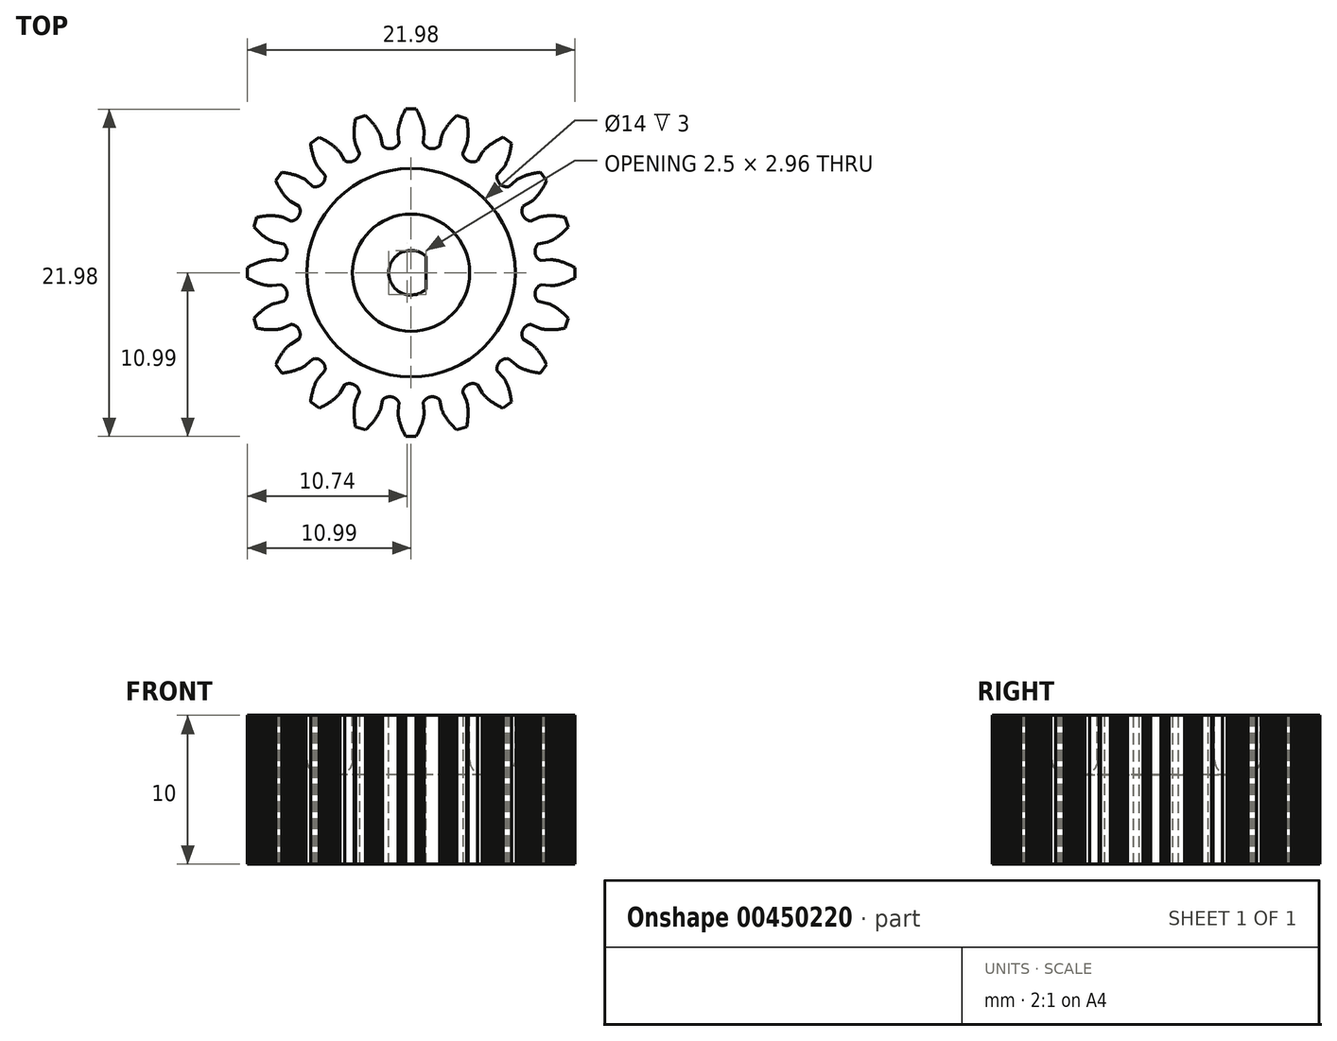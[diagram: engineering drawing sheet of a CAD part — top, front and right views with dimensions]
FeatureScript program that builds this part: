
annotation { "Feature Type Name" : "Feature", "Feature Type Description" : "" }
export const myFeature = defineFeature(function(context is Context, id is Id, definition is map)
    precondition{}
    {
        {
            var Q0;
            Q0=qCreatedBy(makeId("Top.planeOp"),FACE);
            var sketch = newSketch(context, id + "F0", { "sketchPlane" : qUnion([Q0])});
            skLineSegment(sketch, "E0", {"start": v(8.71, -0.82) * mm, "end": v(9.36, -0.88) * mm});
            skLineSegment(sketch, "E1", {"start": v(9.36, -0.88) * mm, "end": v(9.4, -0.88) * mm});
            skLineSegment(sketch, "E2", {"start": v(9.4, -0.88) * mm, "end": v(9.46, -0.88) * mm});
            skLineSegment(sketch, "E3", {"start": v(9.46, -0.88) * mm, "end": v(9.51, -0.87) * mm});
            skLineSegment(sketch, "E4", {"start": v(9.51, -0.87) * mm, "end": v(9.58, -0.87) * mm});
            skLineSegment(sketch, "E5", {"start": v(9.58, -0.87) * mm, "end": v(9.64, -0.86) * mm});
            skLineSegment(sketch, "E6", {"start": v(9.64, -0.86) * mm, "end": v(9.7, -0.85) * mm});
            skLineSegment(sketch, "E7", {"start": v(9.7, -0.85) * mm, "end": v(9.77, -0.83) * mm});
            skLineSegment(sketch, "E8", {"start": v(9.77, -0.83) * mm, "end": v(9.84, -0.82) * mm});
            skLineSegment(sketch, "E9", {"start": v(9.84, -0.82) * mm, "end": v(9.9, -0.8) * mm});
            skLineSegment(sketch, "E10", {"start": v(9.9, -0.8) * mm, "end": v(9.95, -0.8) * mm});
            skLineSegment(sketch, "E11", {"start": v(9.95, -0.8) * mm, "end": v(10, -0.77) * mm});
            skLineSegment(sketch, "E12", {"start": v(10, -0.77) * mm, "end": v(10.07, -0.76) * mm});
            skLineSegment(sketch, "E13", {"start": v(10.07, -0.76) * mm, "end": v(10.13, -0.74) * mm});
            skLineSegment(sketch, "E14", {"start": v(10.13, -0.74) * mm, "end": v(10.2, -0.71) * mm});
            skLineSegment(sketch, "E15", {"start": v(10.2, -0.71) * mm, "end": v(10.26, -0.7) * mm});
            skLineSegment(sketch, "E16", {"start": v(10.26, -0.7) * mm, "end": v(10.33, -0.66) * mm});
            skLineSegment(sketch, "E17", {"start": v(10.33, -0.66) * mm, "end": v(10.4, -0.64) * mm});
            skLineSegment(sketch, "E18", {"start": v(10.4, -0.64) * mm, "end": v(10.48, -0.6) * mm});
            skLineSegment(sketch, "E19", {"start": v(10.48, -0.6) * mm, "end": v(10.55, -0.57) * mm});
            skLineSegment(sketch, "E20", {"start": v(10.55, -0.57) * mm, "end": v(10.63, -0.54) * mm});
            skLineSegment(sketch, "E21", {"start": v(10.63, -0.54) * mm, "end": v(10.71, -0.5) * mm});
            skLineSegment(sketch, "E22", {"start": v(10.71, -0.5) * mm, "end": v(10.8, -0.46) * mm});
            skLineSegment(sketch, "E23", {"start": v(10.8, -0.46) * mm, "end": v(10.88, -0.41) * mm});
            skLineSegment(sketch, "E24", {"start": v(10.88, -0.41) * mm, "end": v(11, -0.35) * mm});
            skLineSegment(sketch, "E25", {"start": v(11, -0.35) * mm, "end": v(11, 0.35) * mm});
            skLineSegment(sketch, "E26", {"start": v(11, 0.35) * mm, "end": v(10.88, 0.41) * mm});
            skLineSegment(sketch, "E27", {"start": v(10.88, 0.41) * mm, "end": v(10.8, 0.46) * mm});
            skLineSegment(sketch, "E28", {"start": v(10.8, 0.46) * mm, "end": v(10.71, 0.5) * mm});
            skLineSegment(sketch, "E29", {"start": v(10.71, 0.5) * mm, "end": v(10.63, 0.54) * mm});
            skLineSegment(sketch, "E30", {"start": v(10.63, 0.54) * mm, "end": v(10.55, 0.57) * mm});
            skLineSegment(sketch, "E31", {"start": v(10.55, 0.57) * mm, "end": v(10.48, 0.6) * mm});
            skLineSegment(sketch, "E32", {"start": v(10.48, 0.6) * mm, "end": v(10.4, 0.64) * mm});
            skLineSegment(sketch, "E33", {"start": v(10.4, 0.64) * mm, "end": v(10.33, 0.66) * mm});
            skLineSegment(sketch, "E34", {"start": v(10.33, 0.66) * mm, "end": v(10.26, 0.7) * mm});
            skLineSegment(sketch, "E35", {"start": v(10.26, 0.7) * mm, "end": v(10.2, 0.71) * mm});
            skLineSegment(sketch, "E36", {"start": v(10.2, 0.71) * mm, "end": v(10.13, 0.74) * mm});
            skLineSegment(sketch, "E37", {"start": v(10.13, 0.74) * mm, "end": v(10.07, 0.76) * mm});
            skLineSegment(sketch, "E38", {"start": v(10.07, 0.76) * mm, "end": v(10, 0.77) * mm});
            skLineSegment(sketch, "E39", {"start": v(10, 0.77) * mm, "end": v(9.95, 0.8) * mm});
            skLineSegment(sketch, "E40", {"start": v(9.95, 0.8) * mm, "end": v(9.9, 0.8) * mm});
            skLineSegment(sketch, "E41", {"start": v(9.9, 0.8) * mm, "end": v(9.84, 0.82) * mm});
            skLineSegment(sketch, "E42", {"start": v(9.84, 0.82) * mm, "end": v(9.77, 0.83) * mm});
            skLineSegment(sketch, "E43", {"start": v(9.77, 0.83) * mm, "end": v(9.7, 0.85) * mm});
            skLineSegment(sketch, "E44", {"start": v(9.7, 0.85) * mm, "end": v(9.64, 0.86) * mm});
            skLineSegment(sketch, "E45", {"start": v(9.64, 0.86) * mm, "end": v(9.58, 0.87) * mm});
            skLineSegment(sketch, "E46", {"start": v(9.58, 0.87) * mm, "end": v(9.51, 0.87) * mm});
            skLineSegment(sketch, "E47", {"start": v(9.51, 0.87) * mm, "end": v(9.46, 0.88) * mm});
            skLineSegment(sketch, "E48", {"start": v(9.46, 0.88) * mm, "end": v(9.4, 0.88) * mm});
            skLineSegment(sketch, "E49", {"start": v(9.4, 0.88) * mm, "end": v(9.36, 0.88) * mm});
            skLineSegment(sketch, "E50", {"start": v(9.36, 0.88) * mm, "end": v(8.71, 0.82) * mm});
            skArc(sketch, "E51", {"start": v(8.71, 0.82) * mm, "mid": v(8.34, 1.32) * mm, "end": v(8.54, 1.92) * mm});
            skLineSegment(sketch, "E52", {"start": v(8.54, 1.92) * mm, "end": v(9.17, 2.06) * mm});
            skLineSegment(sketch, "E53", {"start": v(9.17, 2.06) * mm, "end": v(9.22, 2.07) * mm});
            skLineSegment(sketch, "E54", {"start": v(9.22, 2.07) * mm, "end": v(9.27, 2.09) * mm});
            skLineSegment(sketch, "E55", {"start": v(9.27, 2.09) * mm, "end": v(9.32, 2.11) * mm});
            skLineSegment(sketch, "E56", {"start": v(9.32, 2.11) * mm, "end": v(9.38, 2.14) * mm});
            skLineSegment(sketch, "E57", {"start": v(9.38, 2.14) * mm, "end": v(9.43, 2.16) * mm});
            skLineSegment(sketch, "E58", {"start": v(9.43, 2.16) * mm, "end": v(9.48, 2.2) * mm});
            skLineSegment(sketch, "E59", {"start": v(9.48, 2.2) * mm, "end": v(9.55, 2.22) * mm});
            skLineSegment(sketch, "E60", {"start": v(9.55, 2.22) * mm, "end": v(9.61, 2.26) * mm});
            skLineSegment(sketch, "E61", {"start": v(9.61, 2.26) * mm, "end": v(9.66, 2.3) * mm});
            skLineSegment(sketch, "E62", {"start": v(9.66, 2.3) * mm, "end": v(9.7, 2.32) * mm});
            skLineSegment(sketch, "E63", {"start": v(9.7, 2.32) * mm, "end": v(9.76, 2.36) * mm});
            skLineSegment(sketch, "E64", {"start": v(9.76, 2.36) * mm, "end": v(9.8, 2.4) * mm});
            skLineSegment(sketch, "E65", {"start": v(9.8, 2.4) * mm, "end": v(9.86, 2.43) * mm});
            skLineSegment(sketch, "E66", {"start": v(9.86, 2.43) * mm, "end": v(9.92, 2.47) * mm});
            skLineSegment(sketch, "E67", {"start": v(9.92, 2.47) * mm, "end": v(9.97, 2.52) * mm});
            skLineSegment(sketch, "E68", {"start": v(9.97, 2.52) * mm, "end": v(10.03, 2.56) * mm});
            skLineSegment(sketch, "E69", {"start": v(10.03, 2.56) * mm, "end": v(10.1, 2.61) * mm});
            skLineSegment(sketch, "E70", {"start": v(10.1, 2.61) * mm, "end": v(10.15, 2.66) * mm});
            skLineSegment(sketch, "E71", {"start": v(10.15, 2.66) * mm, "end": v(10.21, 2.72) * mm});
            skLineSegment(sketch, "E72", {"start": v(10.21, 2.72) * mm, "end": v(10.28, 2.78) * mm});
            skLineSegment(sketch, "E73", {"start": v(10.28, 2.78) * mm, "end": v(10.34, 2.84) * mm});
            skLineSegment(sketch, "E74", {"start": v(10.34, 2.84) * mm, "end": v(10.4, 2.9) * mm});
            skLineSegment(sketch, "E75", {"start": v(10.4, 2.9) * mm, "end": v(10.47, 2.97) * mm});
            skLineSegment(sketch, "E76", {"start": v(10.47, 2.97) * mm, "end": v(10.56, 3.07) * mm});
            skLineSegment(sketch, "E77", {"start": v(10.56, 3.07) * mm, "end": v(10.35, 3.73) * mm});
            skLineSegment(sketch, "E78", {"start": v(10.35, 3.73) * mm, "end": v(10.22, 3.75) * mm});
            skLineSegment(sketch, "E79", {"start": v(10.22, 3.75) * mm, "end": v(10.12, 3.77) * mm});
            skLineSegment(sketch, "E80", {"start": v(10.12, 3.77) * mm, "end": v(10.03, 3.78) * mm});
            skLineSegment(sketch, "E81", {"start": v(10.03, 3.78) * mm, "end": v(9.95, 3.8) * mm});
            skLineSegment(sketch, "E82", {"start": v(9.95, 3.8) * mm, "end": v(9.86, 3.8) * mm});
            skLineSegment(sketch, "E83", {"start": v(9.86, 3.8) * mm, "end": v(9.78, 3.81) * mm});
            skLineSegment(sketch, "E84", {"start": v(9.78, 3.81) * mm, "end": v(9.7, 3.82) * mm});
            skLineSegment(sketch, "E85", {"start": v(9.7, 3.82) * mm, "end": v(9.62, 3.82) * mm});
            skLineSegment(sketch, "E86", {"start": v(9.62, 3.82) * mm, "end": v(9.55, 3.83) * mm});
            skLineSegment(sketch, "E87", {"start": v(9.55, 3.83) * mm, "end": v(9.48, 3.83) * mm});
            skLineSegment(sketch, "E88", {"start": v(9.48, 3.83) * mm, "end": v(9.4, 3.83) * mm});
            skLineSegment(sketch, "E89", {"start": v(9.4, 3.83) * mm, "end": v(9.34, 3.83) * mm});
            skLineSegment(sketch, "E90", {"start": v(9.34, 3.83) * mm, "end": v(9.28, 3.83) * mm});
            skLineSegment(sketch, "E91", {"start": v(9.28, 3.83) * mm, "end": v(9.22, 3.83) * mm});
            skLineSegment(sketch, "E92", {"start": v(9.22, 3.83) * mm, "end": v(9.16, 3.82) * mm});
            skLineSegment(sketch, "E93", {"start": v(9.16, 3.82) * mm, "end": v(9.1, 3.82) * mm});
            skLineSegment(sketch, "E94", {"start": v(9.1, 3.82) * mm, "end": v(9.03, 3.81) * mm});
            skLineSegment(sketch, "E95", {"start": v(9.03, 3.81) * mm, "end": v(8.96, 3.8) * mm});
            skLineSegment(sketch, "E96", {"start": v(8.96, 3.8) * mm, "end": v(8.9, 3.8) * mm});
            skLineSegment(sketch, "E97", {"start": v(8.9, 3.8) * mm, "end": v(8.84, 3.78) * mm});
            skLineSegment(sketch, "E98", {"start": v(8.84, 3.78) * mm, "end": v(8.78, 3.77) * mm});
            skLineSegment(sketch, "E99", {"start": v(8.78, 3.77) * mm, "end": v(8.73, 3.76) * mm});
            skLineSegment(sketch, "E100", {"start": v(8.73, 3.76) * mm, "end": v(8.68, 3.74) * mm});
            skLineSegment(sketch, "E101", {"start": v(8.68, 3.74) * mm, "end": v(8.63, 3.73) * mm});
            skLineSegment(sketch, "E102", {"start": v(8.63, 3.73) * mm, "end": v(8.03, 3.47) * mm});
            skArc(sketch, "E103", {"start": v(8.03, 3.47) * mm, "mid": v(7.52, 3.83) * mm, "end": v(7.53, 4.46) * mm});
            skLineSegment(sketch, "E104", {"start": v(7.53, 4.46) * mm, "end": v(8.08, 4.79) * mm});
            skLineSegment(sketch, "E105", {"start": v(8.08, 4.79) * mm, "end": v(8.13, 4.82) * mm});
            skLineSegment(sketch, "E106", {"start": v(8.13, 4.82) * mm, "end": v(8.17, 4.85) * mm});
            skLineSegment(sketch, "E107", {"start": v(8.17, 4.85) * mm, "end": v(8.2, 4.89) * mm});
            skLineSegment(sketch, "E108", {"start": v(8.2, 4.89) * mm, "end": v(8.26, 4.93) * mm});
            skLineSegment(sketch, "E109", {"start": v(8.26, 4.93) * mm, "end": v(8.3, 4.97) * mm});
            skLineSegment(sketch, "E110", {"start": v(8.3, 4.97) * mm, "end": v(8.34, 5.01) * mm});
            skLineSegment(sketch, "E111", {"start": v(8.34, 5.01) * mm, "end": v(8.4, 5.07) * mm});
            skLineSegment(sketch, "E112", {"start": v(8.4, 5.07) * mm, "end": v(8.44, 5.12) * mm});
            skLineSegment(sketch, "E113", {"start": v(8.44, 5.12) * mm, "end": v(8.48, 5.16) * mm});
            skLineSegment(sketch, "E114", {"start": v(8.48, 5.16) * mm, "end": v(8.51, 5.2) * mm});
            skLineSegment(sketch, "E115", {"start": v(8.51, 5.2) * mm, "end": v(8.55, 5.26) * mm});
            skLineSegment(sketch, "E116", {"start": v(8.55, 5.26) * mm, "end": v(8.59, 5.3) * mm});
            skLineSegment(sketch, "E117", {"start": v(8.59, 5.3) * mm, "end": v(8.63, 5.36) * mm});
            skLineSegment(sketch, "E118", {"start": v(8.63, 5.36) * mm, "end": v(8.67, 5.41) * mm});
            skLineSegment(sketch, "E119", {"start": v(8.67, 5.41) * mm, "end": v(8.7, 5.47) * mm});
            skLineSegment(sketch, "E120", {"start": v(8.7, 5.47) * mm, "end": v(8.75, 5.54) * mm});
            skLineSegment(sketch, "E121", {"start": v(8.75, 5.54) * mm, "end": v(8.8, 5.6) * mm});
            skLineSegment(sketch, "E122", {"start": v(8.8, 5.6) * mm, "end": v(8.83, 5.67) * mm});
            skLineSegment(sketch, "E123", {"start": v(8.83, 5.67) * mm, "end": v(8.87, 5.74) * mm});
            skLineSegment(sketch, "E124", {"start": v(8.87, 5.74) * mm, "end": v(8.92, 5.82) * mm});
            skLineSegment(sketch, "E125", {"start": v(8.92, 5.82) * mm, "end": v(8.96, 5.9) * mm});
            skLineSegment(sketch, "E126", {"start": v(8.96, 5.9) * mm, "end": v(9, 5.98) * mm});
            skLineSegment(sketch, "E127", {"start": v(9, 5.98) * mm, "end": v(9.04, 6.06) * mm});
            skLineSegment(sketch, "E128", {"start": v(9.04, 6.06) * mm, "end": v(9.1, 6.18) * mm});
            skLineSegment(sketch, "E129", {"start": v(9.1, 6.18) * mm, "end": v(8.7, 6.74) * mm});
            skLineSegment(sketch, "E130", {"start": v(8.7, 6.74) * mm, "end": v(8.56, 6.73) * mm});
            skLineSegment(sketch, "E131", {"start": v(8.56, 6.73) * mm, "end": v(8.46, 6.71) * mm});
            skLineSegment(sketch, "E132", {"start": v(8.46, 6.71) * mm, "end": v(8.37, 6.7) * mm});
            skLineSegment(sketch, "E133", {"start": v(8.37, 6.7) * mm, "end": v(8.29, 6.68) * mm});
            skLineSegment(sketch, "E134", {"start": v(8.29, 6.68) * mm, "end": v(8.2, 6.67) * mm});
            skLineSegment(sketch, "E135", {"start": v(8.2, 6.67) * mm, "end": v(8.12, 6.65) * mm});
            skLineSegment(sketch, "E136", {"start": v(8.12, 6.65) * mm, "end": v(8.04, 6.63) * mm});
            skLineSegment(sketch, "E137", {"start": v(8.04, 6.63) * mm, "end": v(7.97, 6.61) * mm});
            skLineSegment(sketch, "E138", {"start": v(7.97, 6.61) * mm, "end": v(7.9, 6.6) * mm});
            skLineSegment(sketch, "E139", {"start": v(7.9, 6.6) * mm, "end": v(7.83, 6.57) * mm});
            skLineSegment(sketch, "E140", {"start": v(7.83, 6.57) * mm, "end": v(7.76, 6.55) * mm});
            skLineSegment(sketch, "E141", {"start": v(7.76, 6.55) * mm, "end": v(7.7, 6.53) * mm});
            skLineSegment(sketch, "E142", {"start": v(7.7, 6.53) * mm, "end": v(7.64, 6.5) * mm});
            skLineSegment(sketch, "E143", {"start": v(7.64, 6.5) * mm, "end": v(7.58, 6.49) * mm});
            skLineSegment(sketch, "E144", {"start": v(7.58, 6.49) * mm, "end": v(7.53, 6.47) * mm});
            skLineSegment(sketch, "E145", {"start": v(7.53, 6.47) * mm, "end": v(7.48, 6.45) * mm});
            skLineSegment(sketch, "E146", {"start": v(7.48, 6.45) * mm, "end": v(7.41, 6.42) * mm});
            skLineSegment(sketch, "E147", {"start": v(7.41, 6.42) * mm, "end": v(7.35, 6.39) * mm});
            skLineSegment(sketch, "E148", {"start": v(7.35, 6.39) * mm, "end": v(7.3, 6.36) * mm});
            skLineSegment(sketch, "E149", {"start": v(7.3, 6.36) * mm, "end": v(7.24, 6.33) * mm});
            skLineSegment(sketch, "E150", {"start": v(7.24, 6.33) * mm, "end": v(7.18, 6.3) * mm});
            skLineSegment(sketch, "E151", {"start": v(7.18, 6.3) * mm, "end": v(7.14, 6.27) * mm});
            skLineSegment(sketch, "E152", {"start": v(7.14, 6.27) * mm, "end": v(7.1, 6.24) * mm});
            skLineSegment(sketch, "E153", {"start": v(7.1, 6.24) * mm, "end": v(7.05, 6.2) * mm});
            skLineSegment(sketch, "E154", {"start": v(7.05, 6.2) * mm, "end": v(6.57, 5.78) * mm});
            skArc(sketch, "E155", {"start": v(6.57, 5.78) * mm, "mid": v(5.97, 5.97) * mm, "end": v(5.78, 6.57) * mm});
            skLineSegment(sketch, "E156", {"start": v(5.78, 6.57) * mm, "end": v(6.2, 7.05) * mm});
            skLineSegment(sketch, "E157", {"start": v(6.2, 7.05) * mm, "end": v(6.24, 7.1) * mm});
            skLineSegment(sketch, "E158", {"start": v(6.24, 7.1) * mm, "end": v(6.27, 7.14) * mm});
            skLineSegment(sketch, "E159", {"start": v(6.27, 7.14) * mm, "end": v(6.3, 7.18) * mm});
            skLineSegment(sketch, "E160", {"start": v(6.3, 7.18) * mm, "end": v(6.33, 7.24) * mm});
            skLineSegment(sketch, "E161", {"start": v(6.33, 7.24) * mm, "end": v(6.36, 7.3) * mm});
            skLineSegment(sketch, "E162", {"start": v(6.36, 7.3) * mm, "end": v(6.39, 7.35) * mm});
            skLineSegment(sketch, "E163", {"start": v(6.39, 7.35) * mm, "end": v(6.42, 7.41) * mm});
            skLineSegment(sketch, "E164", {"start": v(6.42, 7.41) * mm, "end": v(6.45, 7.48) * mm});
            skLineSegment(sketch, "E165", {"start": v(6.45, 7.48) * mm, "end": v(6.47, 7.53) * mm});
            skLineSegment(sketch, "E166", {"start": v(6.47, 7.53) * mm, "end": v(6.49, 7.58) * mm});
            skLineSegment(sketch, "E167", {"start": v(6.49, 7.58) * mm, "end": v(6.5, 7.64) * mm});
            skLineSegment(sketch, "E168", {"start": v(6.5, 7.64) * mm, "end": v(6.53, 7.7) * mm});
            skLineSegment(sketch, "E169", {"start": v(6.53, 7.7) * mm, "end": v(6.55, 7.76) * mm});
            skLineSegment(sketch, "E170", {"start": v(6.55, 7.76) * mm, "end": v(6.57, 7.83) * mm});
            skLineSegment(sketch, "E171", {"start": v(6.57, 7.83) * mm, "end": v(6.6, 7.9) * mm});
            skLineSegment(sketch, "E172", {"start": v(6.6, 7.9) * mm, "end": v(6.61, 7.97) * mm});
            skLineSegment(sketch, "E173", {"start": v(6.61, 7.97) * mm, "end": v(6.63, 8.04) * mm});
            skLineSegment(sketch, "E174", {"start": v(6.63, 8.04) * mm, "end": v(6.65, 8.12) * mm});
            skLineSegment(sketch, "E175", {"start": v(6.65, 8.12) * mm, "end": v(6.67, 8.2) * mm});
            skLineSegment(sketch, "E176", {"start": v(6.67, 8.2) * mm, "end": v(6.68, 8.29) * mm});
            skLineSegment(sketch, "E177", {"start": v(6.68, 8.29) * mm, "end": v(6.7, 8.37) * mm});
            skLineSegment(sketch, "E178", {"start": v(6.7, 8.37) * mm, "end": v(6.71, 8.46) * mm});
            skLineSegment(sketch, "E179", {"start": v(6.71, 8.46) * mm, "end": v(6.73, 8.56) * mm});
            skLineSegment(sketch, "E180", {"start": v(6.73, 8.56) * mm, "end": v(6.74, 8.7) * mm});
            skLineSegment(sketch, "E181", {"start": v(6.74, 8.7) * mm, "end": v(6.18, 9.1) * mm});
            skLineSegment(sketch, "E182", {"start": v(6.18, 9.1) * mm, "end": v(6.06, 9.04) * mm});
            skLineSegment(sketch, "E183", {"start": v(6.06, 9.04) * mm, "end": v(5.98, 9) * mm});
            skLineSegment(sketch, "E184", {"start": v(5.98, 9) * mm, "end": v(5.9, 8.96) * mm});
            skLineSegment(sketch, "E185", {"start": v(5.9, 8.96) * mm, "end": v(5.82, 8.92) * mm});
            skLineSegment(sketch, "E186", {"start": v(5.82, 8.92) * mm, "end": v(5.74, 8.87) * mm});
            skLineSegment(sketch, "E187", {"start": v(5.74, 8.87) * mm, "end": v(5.67, 8.83) * mm});
            skLineSegment(sketch, "E188", {"start": v(5.67, 8.83) * mm, "end": v(5.6, 8.8) * mm});
            skLineSegment(sketch, "E189", {"start": v(5.6, 8.8) * mm, "end": v(5.54, 8.75) * mm});
            skLineSegment(sketch, "E190", {"start": v(5.54, 8.75) * mm, "end": v(5.47, 8.7) * mm});
            skLineSegment(sketch, "E191", {"start": v(5.47, 8.7) * mm, "end": v(5.41, 8.67) * mm});
            skLineSegment(sketch, "E192", {"start": v(5.41, 8.67) * mm, "end": v(5.36, 8.63) * mm});
            skLineSegment(sketch, "E193", {"start": v(5.36, 8.63) * mm, "end": v(5.3, 8.59) * mm});
            skLineSegment(sketch, "E194", {"start": v(5.3, 8.59) * mm, "end": v(5.26, 8.55) * mm});
            skLineSegment(sketch, "E195", {"start": v(5.26, 8.55) * mm, "end": v(5.2, 8.51) * mm});
            skLineSegment(sketch, "E196", {"start": v(5.2, 8.51) * mm, "end": v(5.16, 8.48) * mm});
            skLineSegment(sketch, "E197", {"start": v(5.16, 8.48) * mm, "end": v(5.12, 8.44) * mm});
            skLineSegment(sketch, "E198", {"start": v(5.12, 8.44) * mm, "end": v(5.07, 8.4) * mm});
            skLineSegment(sketch, "E199", {"start": v(5.07, 8.4) * mm, "end": v(5.01, 8.34) * mm});
            skLineSegment(sketch, "E200", {"start": v(5.01, 8.34) * mm, "end": v(4.97, 8.3) * mm});
            skLineSegment(sketch, "E201", {"start": v(4.97, 8.3) * mm, "end": v(4.93, 8.26) * mm});
            skLineSegment(sketch, "E202", {"start": v(4.93, 8.26) * mm, "end": v(4.89, 8.2) * mm});
            skLineSegment(sketch, "E203", {"start": v(4.89, 8.2) * mm, "end": v(4.85, 8.17) * mm});
            skLineSegment(sketch, "E204", {"start": v(4.85, 8.17) * mm, "end": v(4.82, 8.13) * mm});
            skLineSegment(sketch, "E205", {"start": v(4.82, 8.13) * mm, "end": v(4.79, 8.08) * mm});
            skLineSegment(sketch, "E206", {"start": v(4.79, 8.08) * mm, "end": v(4.46, 7.53) * mm});
            skArc(sketch, "E207", {"start": v(4.46, 7.53) * mm, "mid": v(3.83, 7.52) * mm, "end": v(3.47, 8.03) * mm});
            skLineSegment(sketch, "E208", {"start": v(3.47, 8.03) * mm, "end": v(3.73, 8.63) * mm});
            skLineSegment(sketch, "E209", {"start": v(3.73, 8.63) * mm, "end": v(3.74, 8.68) * mm});
            skLineSegment(sketch, "E210", {"start": v(3.74, 8.68) * mm, "end": v(3.76, 8.73) * mm});
            skLineSegment(sketch, "E211", {"start": v(3.76, 8.73) * mm, "end": v(3.77, 8.78) * mm});
            skLineSegment(sketch, "E212", {"start": v(3.77, 8.78) * mm, "end": v(3.78, 8.84) * mm});
            skLineSegment(sketch, "E213", {"start": v(3.78, 8.84) * mm, "end": v(3.8, 8.9) * mm});
            skLineSegment(sketch, "E214", {"start": v(3.8, 8.9) * mm, "end": v(3.8, 8.96) * mm});
            skLineSegment(sketch, "E215", {"start": v(3.8, 8.96) * mm, "end": v(3.81, 9.03) * mm});
            skLineSegment(sketch, "E216", {"start": v(3.81, 9.03) * mm, "end": v(3.82, 9.1) * mm});
            skLineSegment(sketch, "E217", {"start": v(3.82, 9.1) * mm, "end": v(3.82, 9.16) * mm});
            skLineSegment(sketch, "E218", {"start": v(3.82, 9.16) * mm, "end": v(3.83, 9.22) * mm});
            skLineSegment(sketch, "E219", {"start": v(3.83, 9.22) * mm, "end": v(3.83, 9.28) * mm});
            skLineSegment(sketch, "E220", {"start": v(3.83, 9.28) * mm, "end": v(3.83, 9.34) * mm});
            skLineSegment(sketch, "E221", {"start": v(3.83, 9.34) * mm, "end": v(3.83, 9.4) * mm});
            skLineSegment(sketch, "E222", {"start": v(3.83, 9.4) * mm, "end": v(3.83, 9.48) * mm});
            skLineSegment(sketch, "E223", {"start": v(3.83, 9.48) * mm, "end": v(3.83, 9.55) * mm});
            skLineSegment(sketch, "E224", {"start": v(3.83, 9.55) * mm, "end": v(3.82, 9.62) * mm});
            skLineSegment(sketch, "E225", {"start": v(3.82, 9.62) * mm, "end": v(3.82, 9.7) * mm});
            skLineSegment(sketch, "E226", {"start": v(3.82, 9.7) * mm, "end": v(3.81, 9.78) * mm});
            skLineSegment(sketch, "E227", {"start": v(3.81, 9.78) * mm, "end": v(3.8, 9.86) * mm});
            skLineSegment(sketch, "E228", {"start": v(3.8, 9.86) * mm, "end": v(3.8, 9.95) * mm});
            skLineSegment(sketch, "E229", {"start": v(3.8, 9.95) * mm, "end": v(3.78, 10.03) * mm});
            skLineSegment(sketch, "E230", {"start": v(3.78, 10.03) * mm, "end": v(3.77, 10.12) * mm});
            skLineSegment(sketch, "E231", {"start": v(3.77, 10.12) * mm, "end": v(3.75, 10.22) * mm});
            skLineSegment(sketch, "E232", {"start": v(3.75, 10.22) * mm, "end": v(3.73, 10.35) * mm});
            skLineSegment(sketch, "E233", {"start": v(3.73, 10.35) * mm, "end": v(3.07, 10.56) * mm});
            skLineSegment(sketch, "E234", {"start": v(3.07, 10.56) * mm, "end": v(2.97, 10.47) * mm});
            skLineSegment(sketch, "E235", {"start": v(2.97, 10.47) * mm, "end": v(2.9, 10.4) * mm});
            skLineSegment(sketch, "E236", {"start": v(2.9, 10.4) * mm, "end": v(2.84, 10.34) * mm});
            skLineSegment(sketch, "E237", {"start": v(2.84, 10.34) * mm, "end": v(2.78, 10.28) * mm});
            skLineSegment(sketch, "E238", {"start": v(2.78, 10.28) * mm, "end": v(2.72, 10.21) * mm});
            skLineSegment(sketch, "E239", {"start": v(2.72, 10.21) * mm, "end": v(2.66, 10.15) * mm});
            skLineSegment(sketch, "E240", {"start": v(2.66, 10.15) * mm, "end": v(2.61, 10.1) * mm});
            skLineSegment(sketch, "E241", {"start": v(2.61, 10.1) * mm, "end": v(2.56, 10.03) * mm});
            skLineSegment(sketch, "E242", {"start": v(2.56, 10.03) * mm, "end": v(2.52, 9.97) * mm});
            skLineSegment(sketch, "E243", {"start": v(2.52, 9.97) * mm, "end": v(2.47, 9.92) * mm});
            skLineSegment(sketch, "E244", {"start": v(2.47, 9.92) * mm, "end": v(2.43, 9.86) * mm});
            skLineSegment(sketch, "E245", {"start": v(2.43, 9.86) * mm, "end": v(2.4, 9.8) * mm});
            skLineSegment(sketch, "E246", {"start": v(2.4, 9.8) * mm, "end": v(2.36, 9.76) * mm});
            skLineSegment(sketch, "E247", {"start": v(2.36, 9.76) * mm, "end": v(2.32, 9.7) * mm});
            skLineSegment(sketch, "E248", {"start": v(2.32, 9.7) * mm, "end": v(2.3, 9.66) * mm});
            skLineSegment(sketch, "E249", {"start": v(2.3, 9.66) * mm, "end": v(2.26, 9.61) * mm});
            skLineSegment(sketch, "E250", {"start": v(2.26, 9.61) * mm, "end": v(2.22, 9.55) * mm});
            skLineSegment(sketch, "E251", {"start": v(2.22, 9.55) * mm, "end": v(2.2, 9.48) * mm});
            skLineSegment(sketch, "E252", {"start": v(2.2, 9.48) * mm, "end": v(2.16, 9.43) * mm});
            skLineSegment(sketch, "E253", {"start": v(2.16, 9.43) * mm, "end": v(2.14, 9.38) * mm});
            skLineSegment(sketch, "E254", {"start": v(2.14, 9.38) * mm, "end": v(2.11, 9.32) * mm});
            skLineSegment(sketch, "E255", {"start": v(2.11, 9.32) * mm, "end": v(2.09, 9.27) * mm});
            skLineSegment(sketch, "E256", {"start": v(2.09, 9.27) * mm, "end": v(2.07, 9.22) * mm});
            skLineSegment(sketch, "E257", {"start": v(2.07, 9.22) * mm, "end": v(2.06, 9.17) * mm});
            skLineSegment(sketch, "E258", {"start": v(2.06, 9.17) * mm, "end": v(1.92, 8.54) * mm});
            skArc(sketch, "E259", {"start": v(1.92, 8.54) * mm, "mid": v(1.32, 8.34) * mm, "end": v(0.82, 8.71) * mm});
            skLineSegment(sketch, "E260", {"start": v(0.82, 8.71) * mm, "end": v(0.88, 9.36) * mm});
            skLineSegment(sketch, "E261", {"start": v(0.88, 9.36) * mm, "end": v(0.88, 9.4) * mm});
            skLineSegment(sketch, "E262", {"start": v(0.88, 9.4) * mm, "end": v(0.88, 9.46) * mm});
            skLineSegment(sketch, "E263", {"start": v(0.88, 9.46) * mm, "end": v(0.87, 9.51) * mm});
            skLineSegment(sketch, "E264", {"start": v(0.87, 9.51) * mm, "end": v(0.87, 9.58) * mm});
            skLineSegment(sketch, "E265", {"start": v(0.87, 9.58) * mm, "end": v(0.86, 9.64) * mm});
            skLineSegment(sketch, "E266", {"start": v(0.86, 9.64) * mm, "end": v(0.85, 9.7) * mm});
            skLineSegment(sketch, "E267", {"start": v(0.85, 9.7) * mm, "end": v(0.83, 9.77) * mm});
            skLineSegment(sketch, "E268", {"start": v(0.83, 9.77) * mm, "end": v(0.82, 9.84) * mm});
            skLineSegment(sketch, "E269", {"start": v(0.82, 9.84) * mm, "end": v(0.8, 9.9) * mm});
            skLineSegment(sketch, "E270", {"start": v(0.8, 9.9) * mm, "end": v(0.8, 9.95) * mm});
            skLineSegment(sketch, "E271", {"start": v(0.8, 9.95) * mm, "end": v(0.77, 10) * mm});
            skLineSegment(sketch, "E272", {"start": v(0.77, 10) * mm, "end": v(0.76, 10.07) * mm});
            skLineSegment(sketch, "E273", {"start": v(0.76, 10.07) * mm, "end": v(0.74, 10.13) * mm});
            skLineSegment(sketch, "E274", {"start": v(0.74, 10.13) * mm, "end": v(0.71, 10.2) * mm});
            skLineSegment(sketch, "E275", {"start": v(0.71, 10.2) * mm, "end": v(0.7, 10.26) * mm});
            skLineSegment(sketch, "E276", {"start": v(0.7, 10.26) * mm, "end": v(0.66, 10.33) * mm});
            skLineSegment(sketch, "E277", {"start": v(0.66, 10.33) * mm, "end": v(0.64, 10.4) * mm});
            skLineSegment(sketch, "E278", {"start": v(0.64, 10.4) * mm, "end": v(0.6, 10.48) * mm});
            skLineSegment(sketch, "E279", {"start": v(0.6, 10.48) * mm, "end": v(0.57, 10.55) * mm});
            skLineSegment(sketch, "E280", {"start": v(0.57, 10.55) * mm, "end": v(0.54, 10.63) * mm});
            skLineSegment(sketch, "E281", {"start": v(0.54, 10.63) * mm, "end": v(0.5, 10.71) * mm});
            skLineSegment(sketch, "E282", {"start": v(0.5, 10.71) * mm, "end": v(0.46, 10.8) * mm});
            skLineSegment(sketch, "E283", {"start": v(0.46, 10.8) * mm, "end": v(0.41, 10.88) * mm});
            skLineSegment(sketch, "E284", {"start": v(0.41, 10.88) * mm, "end": v(0.35, 11) * mm});
            skLineSegment(sketch, "E285", {"start": v(0.35, 11) * mm, "end": v(-0.35, 11) * mm});
            skLineSegment(sketch, "E286", {"start": v(-0.35, 11) * mm, "end": v(-0.41, 10.88) * mm});
            skLineSegment(sketch, "E287", {"start": v(-0.41, 10.88) * mm, "end": v(-0.46, 10.8) * mm});
            skLineSegment(sketch, "E288", {"start": v(-0.46, 10.8) * mm, "end": v(-0.5, 10.71) * mm});
            skLineSegment(sketch, "E289", {"start": v(-0.5, 10.71) * mm, "end": v(-0.54, 10.63) * mm});
            skLineSegment(sketch, "E290", {"start": v(-0.54, 10.63) * mm, "end": v(-0.57, 10.55) * mm});
            skLineSegment(sketch, "E291", {"start": v(-0.57, 10.55) * mm, "end": v(-0.6, 10.48) * mm});
            skLineSegment(sketch, "E292", {"start": v(-0.6, 10.48) * mm, "end": v(-0.64, 10.4) * mm});
            skLineSegment(sketch, "E293", {"start": v(-0.64, 10.4) * mm, "end": v(-0.66, 10.33) * mm});
            skLineSegment(sketch, "E294", {"start": v(-0.66, 10.33) * mm, "end": v(-0.7, 10.26) * mm});
            skLineSegment(sketch, "E295", {"start": v(-0.7, 10.26) * mm, "end": v(-0.71, 10.2) * mm});
            skLineSegment(sketch, "E296", {"start": v(-0.71, 10.2) * mm, "end": v(-0.74, 10.13) * mm});
            skLineSegment(sketch, "E297", {"start": v(-0.74, 10.13) * mm, "end": v(-0.76, 10.07) * mm});
            skLineSegment(sketch, "E298", {"start": v(-0.76, 10.07) * mm, "end": v(-0.77, 10) * mm});
            skLineSegment(sketch, "E299", {"start": v(-0.77, 10) * mm, "end": v(-0.8, 9.95) * mm});
            skLineSegment(sketch, "E300", {"start": v(-0.8, 9.95) * mm, "end": v(-0.8, 9.9) * mm});
            skLineSegment(sketch, "E301", {"start": v(-0.8, 9.9) * mm, "end": v(-0.82, 9.84) * mm});
            skLineSegment(sketch, "E302", {"start": v(-0.82, 9.84) * mm, "end": v(-0.83, 9.77) * mm});
            skLineSegment(sketch, "E303", {"start": v(-0.83, 9.77) * mm, "end": v(-0.85, 9.7) * mm});
            skLineSegment(sketch, "E304", {"start": v(-0.85, 9.7) * mm, "end": v(-0.86, 9.64) * mm});
            skLineSegment(sketch, "E305", {"start": v(-0.86, 9.64) * mm, "end": v(-0.87, 9.58) * mm});
            skLineSegment(sketch, "E306", {"start": v(-0.87, 9.58) * mm, "end": v(-0.87, 9.51) * mm});
            skLineSegment(sketch, "E307", {"start": v(-0.87, 9.51) * mm, "end": v(-0.88, 9.46) * mm});
            skLineSegment(sketch, "E308", {"start": v(-0.88, 9.46) * mm, "end": v(-0.88, 9.4) * mm});
            skLineSegment(sketch, "E309", {"start": v(-0.88, 9.4) * mm, "end": v(-0.88, 9.36) * mm});
            skLineSegment(sketch, "E310", {"start": v(-0.88, 9.36) * mm, "end": v(-0.82, 8.71) * mm});
            skArc(sketch, "E311", {"start": v(-0.82, 8.71) * mm, "mid": v(-1.32, 8.34) * mm, "end": v(-1.92, 8.54) * mm});
            skLineSegment(sketch, "E312", {"start": v(-1.92, 8.54) * mm, "end": v(-2.06, 9.17) * mm});
            skLineSegment(sketch, "E313", {"start": v(-2.06, 9.17) * mm, "end": v(-2.07, 9.22) * mm});
            skLineSegment(sketch, "E314", {"start": v(-2.07, 9.22) * mm, "end": v(-2.09, 9.27) * mm});
            skLineSegment(sketch, "E315", {"start": v(-2.09, 9.27) * mm, "end": v(-2.11, 9.32) * mm});
            skLineSegment(sketch, "E316", {"start": v(-2.11, 9.32) * mm, "end": v(-2.14, 9.38) * mm});
            skLineSegment(sketch, "E317", {"start": v(-2.14, 9.38) * mm, "end": v(-2.16, 9.43) * mm});
            skLineSegment(sketch, "E318", {"start": v(-2.16, 9.43) * mm, "end": v(-2.2, 9.48) * mm});
            skLineSegment(sketch, "E319", {"start": v(-2.2, 9.48) * mm, "end": v(-2.22, 9.55) * mm});
            skLineSegment(sketch, "E320", {"start": v(-2.22, 9.55) * mm, "end": v(-2.26, 9.61) * mm});
            skLineSegment(sketch, "E321", {"start": v(-2.26, 9.61) * mm, "end": v(-2.3, 9.66) * mm});
            skLineSegment(sketch, "E322", {"start": v(-2.3, 9.66) * mm, "end": v(-2.32, 9.7) * mm});
            skLineSegment(sketch, "E323", {"start": v(-2.32, 9.7) * mm, "end": v(-2.36, 9.76) * mm});
            skLineSegment(sketch, "E324", {"start": v(-2.36, 9.76) * mm, "end": v(-2.4, 9.8) * mm});
            skLineSegment(sketch, "E325", {"start": v(-2.4, 9.8) * mm, "end": v(-2.43, 9.86) * mm});
            skLineSegment(sketch, "E326", {"start": v(-2.43, 9.86) * mm, "end": v(-2.47, 9.92) * mm});
            skLineSegment(sketch, "E327", {"start": v(-2.47, 9.92) * mm, "end": v(-2.52, 9.97) * mm});
            skLineSegment(sketch, "E328", {"start": v(-2.52, 9.97) * mm, "end": v(-2.56, 10.03) * mm});
            skLineSegment(sketch, "E329", {"start": v(-2.56, 10.03) * mm, "end": v(-2.61, 10.1) * mm});
            skLineSegment(sketch, "E330", {"start": v(-2.61, 10.1) * mm, "end": v(-2.66, 10.15) * mm});
            skLineSegment(sketch, "E331", {"start": v(-2.66, 10.15) * mm, "end": v(-2.72, 10.21) * mm});
            skLineSegment(sketch, "E332", {"start": v(-2.72, 10.21) * mm, "end": v(-2.78, 10.28) * mm});
            skLineSegment(sketch, "E333", {"start": v(-2.78, 10.28) * mm, "end": v(-2.84, 10.34) * mm});
            skLineSegment(sketch, "E334", {"start": v(-2.84, 10.34) * mm, "end": v(-2.9, 10.4) * mm});
            skLineSegment(sketch, "E335", {"start": v(-2.9, 10.4) * mm, "end": v(-2.97, 10.47) * mm});
            skLineSegment(sketch, "E336", {"start": v(-2.97, 10.47) * mm, "end": v(-3.07, 10.56) * mm});
            skLineSegment(sketch, "E337", {"start": v(-3.07, 10.56) * mm, "end": v(-3.73, 10.35) * mm});
            skLineSegment(sketch, "E338", {"start": v(-3.73, 10.35) * mm, "end": v(-3.75, 10.22) * mm});
            skLineSegment(sketch, "E339", {"start": v(-3.75, 10.22) * mm, "end": v(-3.77, 10.12) * mm});
            skLineSegment(sketch, "E340", {"start": v(-3.77, 10.12) * mm, "end": v(-3.78, 10.03) * mm});
            skLineSegment(sketch, "E341", {"start": v(-3.78, 10.03) * mm, "end": v(-3.8, 9.95) * mm});
            skLineSegment(sketch, "E342", {"start": v(-3.8, 9.95) * mm, "end": v(-3.8, 9.86) * mm});
            skLineSegment(sketch, "E343", {"start": v(-3.8, 9.86) * mm, "end": v(-3.81, 9.78) * mm});
            skLineSegment(sketch, "E344", {"start": v(-3.81, 9.78) * mm, "end": v(-3.82, 9.7) * mm});
            skLineSegment(sketch, "E345", {"start": v(-3.82, 9.7) * mm, "end": v(-3.82, 9.62) * mm});
            skLineSegment(sketch, "E346", {"start": v(-3.82, 9.62) * mm, "end": v(-3.83, 9.55) * mm});
            skLineSegment(sketch, "E347", {"start": v(-3.83, 9.55) * mm, "end": v(-3.83, 9.48) * mm});
            skLineSegment(sketch, "E348", {"start": v(-3.83, 9.48) * mm, "end": v(-3.83, 9.4) * mm});
            skLineSegment(sketch, "E349", {"start": v(-3.83, 9.4) * mm, "end": v(-3.83, 9.34) * mm});
            skLineSegment(sketch, "E350", {"start": v(-3.83, 9.34) * mm, "end": v(-3.83, 9.28) * mm});
            skLineSegment(sketch, "E351", {"start": v(-3.83, 9.28) * mm, "end": v(-3.83, 9.22) * mm});
            skLineSegment(sketch, "E352", {"start": v(-3.83, 9.22) * mm, "end": v(-3.82, 9.16) * mm});
            skLineSegment(sketch, "E353", {"start": v(-3.82, 9.16) * mm, "end": v(-3.82, 9.1) * mm});
            skLineSegment(sketch, "E354", {"start": v(-3.82, 9.1) * mm, "end": v(-3.81, 9.03) * mm});
            skLineSegment(sketch, "E355", {"start": v(-3.81, 9.03) * mm, "end": v(-3.8, 8.96) * mm});
            skLineSegment(sketch, "E356", {"start": v(-3.8, 8.96) * mm, "end": v(-3.8, 8.9) * mm});
            skLineSegment(sketch, "E357", {"start": v(-3.8, 8.9) * mm, "end": v(-3.78, 8.84) * mm});
            skLineSegment(sketch, "E358", {"start": v(-3.78, 8.84) * mm, "end": v(-3.77, 8.78) * mm});
            skLineSegment(sketch, "E359", {"start": v(-3.77, 8.78) * mm, "end": v(-3.76, 8.73) * mm});
            skLineSegment(sketch, "E360", {"start": v(-3.76, 8.73) * mm, "end": v(-3.74, 8.68) * mm});
            skLineSegment(sketch, "E361", {"start": v(-3.74, 8.68) * mm, "end": v(-3.73, 8.63) * mm});
            skLineSegment(sketch, "E362", {"start": v(-3.73, 8.63) * mm, "end": v(-3.47, 8.03) * mm});
            skArc(sketch, "E363", {"start": v(-3.47, 8.03) * mm, "mid": v(-3.83, 7.52) * mm, "end": v(-4.46, 7.53) * mm});
            skLineSegment(sketch, "E364", {"start": v(-4.46, 7.53) * mm, "end": v(-4.79, 8.08) * mm});
            skLineSegment(sketch, "E365", {"start": v(-4.79, 8.08) * mm, "end": v(-4.82, 8.13) * mm});
            skLineSegment(sketch, "E366", {"start": v(-4.82, 8.13) * mm, "end": v(-4.85, 8.17) * mm});
            skLineSegment(sketch, "E367", {"start": v(-4.85, 8.17) * mm, "end": v(-4.89, 8.2) * mm});
            skLineSegment(sketch, "E368", {"start": v(-4.89, 8.2) * mm, "end": v(-4.93, 8.26) * mm});
            skLineSegment(sketch, "E369", {"start": v(-4.93, 8.26) * mm, "end": v(-4.97, 8.3) * mm});
            skLineSegment(sketch, "E370", {"start": v(-4.97, 8.3) * mm, "end": v(-5.01, 8.34) * mm});
            skLineSegment(sketch, "E371", {"start": v(-5.01, 8.34) * mm, "end": v(-5.07, 8.4) * mm});
            skLineSegment(sketch, "E372", {"start": v(-5.07, 8.4) * mm, "end": v(-5.12, 8.44) * mm});
            skLineSegment(sketch, "E373", {"start": v(-5.12, 8.44) * mm, "end": v(-5.16, 8.48) * mm});
            skLineSegment(sketch, "E374", {"start": v(-5.16, 8.48) * mm, "end": v(-5.2, 8.51) * mm});
            skLineSegment(sketch, "E375", {"start": v(-5.2, 8.51) * mm, "end": v(-5.26, 8.55) * mm});
            skLineSegment(sketch, "E376", {"start": v(-5.26, 8.55) * mm, "end": v(-5.3, 8.59) * mm});
            skLineSegment(sketch, "E377", {"start": v(-5.3, 8.59) * mm, "end": v(-5.36, 8.63) * mm});
            skLineSegment(sketch, "E378", {"start": v(-5.36, 8.63) * mm, "end": v(-5.41, 8.67) * mm});
            skLineSegment(sketch, "E379", {"start": v(-5.41, 8.67) * mm, "end": v(-5.47, 8.7) * mm});
            skLineSegment(sketch, "E380", {"start": v(-5.47, 8.7) * mm, "end": v(-5.54, 8.75) * mm});
            skLineSegment(sketch, "E381", {"start": v(-5.54, 8.75) * mm, "end": v(-5.6, 8.8) * mm});
            skLineSegment(sketch, "E382", {"start": v(-5.6, 8.8) * mm, "end": v(-5.67, 8.83) * mm});
            skLineSegment(sketch, "E383", {"start": v(-5.67, 8.83) * mm, "end": v(-5.74, 8.87) * mm});
            skLineSegment(sketch, "E384", {"start": v(-5.74, 8.87) * mm, "end": v(-5.82, 8.92) * mm});
            skLineSegment(sketch, "E385", {"start": v(-5.82, 8.92) * mm, "end": v(-5.9, 8.96) * mm});
            skLineSegment(sketch, "E386", {"start": v(-5.9, 8.96) * mm, "end": v(-5.98, 9) * mm});
            skLineSegment(sketch, "E387", {"start": v(-5.98, 9) * mm, "end": v(-6.06, 9.04) * mm});
            skLineSegment(sketch, "E388", {"start": v(-6.06, 9.04) * mm, "end": v(-6.18, 9.1) * mm});
            skLineSegment(sketch, "E389", {"start": v(-6.18, 9.1) * mm, "end": v(-6.74, 8.7) * mm});
            skLineSegment(sketch, "E390", {"start": v(-6.74, 8.7) * mm, "end": v(-6.73, 8.56) * mm});
            skLineSegment(sketch, "E391", {"start": v(-6.73, 8.56) * mm, "end": v(-6.71, 8.46) * mm});
            skLineSegment(sketch, "E392", {"start": v(-6.71, 8.46) * mm, "end": v(-6.7, 8.37) * mm});
            skLineSegment(sketch, "E393", {"start": v(-6.7, 8.37) * mm, "end": v(-6.68, 8.29) * mm});
            skLineSegment(sketch, "E394", {"start": v(-6.68, 8.29) * mm, "end": v(-6.67, 8.2) * mm});
            skLineSegment(sketch, "E395", {"start": v(-6.67, 8.2) * mm, "end": v(-6.65, 8.12) * mm});
            skLineSegment(sketch, "E396", {"start": v(-6.65, 8.12) * mm, "end": v(-6.63, 8.04) * mm});
            skLineSegment(sketch, "E397", {"start": v(-6.63, 8.04) * mm, "end": v(-6.61, 7.97) * mm});
            skLineSegment(sketch, "E398", {"start": v(-6.61, 7.97) * mm, "end": v(-6.6, 7.9) * mm});
            skLineSegment(sketch, "E399", {"start": v(-6.6, 7.9) * mm, "end": v(-6.57, 7.83) * mm});
            skLineSegment(sketch, "E400", {"start": v(-6.57, 7.83) * mm, "end": v(-6.55, 7.76) * mm});
            skLineSegment(sketch, "E401", {"start": v(-6.55, 7.76) * mm, "end": v(-6.53, 7.7) * mm});
            skLineSegment(sketch, "E402", {"start": v(-6.53, 7.7) * mm, "end": v(-6.5, 7.64) * mm});
            skLineSegment(sketch, "E403", {"start": v(-6.5, 7.64) * mm, "end": v(-6.49, 7.58) * mm});
            skLineSegment(sketch, "E404", {"start": v(-6.49, 7.58) * mm, "end": v(-6.47, 7.53) * mm});
            skLineSegment(sketch, "E405", {"start": v(-6.47, 7.53) * mm, "end": v(-6.45, 7.48) * mm});
            skLineSegment(sketch, "E406", {"start": v(-6.45, 7.48) * mm, "end": v(-6.42, 7.41) * mm});
            skLineSegment(sketch, "E407", {"start": v(-6.42, 7.41) * mm, "end": v(-6.39, 7.35) * mm});
            skLineSegment(sketch, "E408", {"start": v(-6.39, 7.35) * mm, "end": v(-6.36, 7.3) * mm});
            skLineSegment(sketch, "E409", {"start": v(-6.36, 7.3) * mm, "end": v(-6.33, 7.24) * mm});
            skLineSegment(sketch, "E410", {"start": v(-6.33, 7.24) * mm, "end": v(-6.3, 7.18) * mm});
            skLineSegment(sketch, "E411", {"start": v(-6.3, 7.18) * mm, "end": v(-6.27, 7.14) * mm});
            skLineSegment(sketch, "E412", {"start": v(-6.27, 7.14) * mm, "end": v(-6.24, 7.1) * mm});
            skLineSegment(sketch, "E413", {"start": v(-6.24, 7.1) * mm, "end": v(-6.2, 7.05) * mm});
            skLineSegment(sketch, "E414", {"start": v(-6.2, 7.05) * mm, "end": v(-5.78, 6.57) * mm});
            skArc(sketch, "E415", {"start": v(-5.78, 6.57) * mm, "mid": v(-5.97, 5.97) * mm, "end": v(-6.57, 5.78) * mm});
            skLineSegment(sketch, "E416", {"start": v(-6.57, 5.78) * mm, "end": v(-7.05, 6.2) * mm});
            skLineSegment(sketch, "E417", {"start": v(-7.05, 6.2) * mm, "end": v(-7.1, 6.24) * mm});
            skLineSegment(sketch, "E418", {"start": v(-7.1, 6.24) * mm, "end": v(-7.14, 6.27) * mm});
            skLineSegment(sketch, "E419", {"start": v(-7.14, 6.27) * mm, "end": v(-7.18, 6.3) * mm});
            skLineSegment(sketch, "E420", {"start": v(-7.18, 6.3) * mm, "end": v(-7.24, 6.33) * mm});
            skLineSegment(sketch, "E421", {"start": v(-7.24, 6.33) * mm, "end": v(-7.3, 6.36) * mm});
            skLineSegment(sketch, "E422", {"start": v(-7.3, 6.36) * mm, "end": v(-7.35, 6.39) * mm});
            skLineSegment(sketch, "E423", {"start": v(-7.35, 6.39) * mm, "end": v(-7.41, 6.42) * mm});
            skLineSegment(sketch, "E424", {"start": v(-7.41, 6.42) * mm, "end": v(-7.48, 6.45) * mm});
            skLineSegment(sketch, "E425", {"start": v(-7.48, 6.45) * mm, "end": v(-7.53, 6.47) * mm});
            skLineSegment(sketch, "E426", {"start": v(-7.53, 6.47) * mm, "end": v(-7.58, 6.49) * mm});
            skLineSegment(sketch, "E427", {"start": v(-7.58, 6.49) * mm, "end": v(-7.64, 6.5) * mm});
            skLineSegment(sketch, "E428", {"start": v(-7.64, 6.5) * mm, "end": v(-7.7, 6.53) * mm});
            skLineSegment(sketch, "E429", {"start": v(-7.7, 6.53) * mm, "end": v(-7.76, 6.55) * mm});
            skLineSegment(sketch, "E430", {"start": v(-7.76, 6.55) * mm, "end": v(-7.83, 6.57) * mm});
            skLineSegment(sketch, "E431", {"start": v(-7.83, 6.57) * mm, "end": v(-7.9, 6.6) * mm});
            skLineSegment(sketch, "E432", {"start": v(-7.9, 6.6) * mm, "end": v(-7.97, 6.61) * mm});
            skLineSegment(sketch, "E433", {"start": v(-7.97, 6.61) * mm, "end": v(-8.04, 6.63) * mm});
            skLineSegment(sketch, "E434", {"start": v(-8.04, 6.63) * mm, "end": v(-8.12, 6.65) * mm});
            skLineSegment(sketch, "E435", {"start": v(-8.12, 6.65) * mm, "end": v(-8.2, 6.67) * mm});
            skLineSegment(sketch, "E436", {"start": v(-8.2, 6.67) * mm, "end": v(-8.29, 6.68) * mm});
            skLineSegment(sketch, "E437", {"start": v(-8.29, 6.68) * mm, "end": v(-8.37, 6.7) * mm});
            skLineSegment(sketch, "E438", {"start": v(-8.37, 6.7) * mm, "end": v(-8.46, 6.71) * mm});
            skLineSegment(sketch, "E439", {"start": v(-8.46, 6.71) * mm, "end": v(-8.56, 6.73) * mm});
            skLineSegment(sketch, "E440", {"start": v(-8.56, 6.73) * mm, "end": v(-8.7, 6.74) * mm});
            skLineSegment(sketch, "E441", {"start": v(-8.7, 6.74) * mm, "end": v(-9.1, 6.18) * mm});
            skLineSegment(sketch, "E442", {"start": v(-9.1, 6.18) * mm, "end": v(-9.04, 6.06) * mm});
            skLineSegment(sketch, "E443", {"start": v(-9.04, 6.06) * mm, "end": v(-9, 5.98) * mm});
            skLineSegment(sketch, "E444", {"start": v(-9, 5.98) * mm, "end": v(-8.96, 5.9) * mm});
            skLineSegment(sketch, "E445", {"start": v(-8.96, 5.9) * mm, "end": v(-8.92, 5.82) * mm});
            skLineSegment(sketch, "E446", {"start": v(-8.92, 5.82) * mm, "end": v(-8.87, 5.74) * mm});
            skLineSegment(sketch, "E447", {"start": v(-8.87, 5.74) * mm, "end": v(-8.83, 5.67) * mm});
            skLineSegment(sketch, "E448", {"start": v(-8.83, 5.67) * mm, "end": v(-8.8, 5.6) * mm});
            skLineSegment(sketch, "E449", {"start": v(-8.8, 5.6) * mm, "end": v(-8.75, 5.54) * mm});
            skLineSegment(sketch, "E450", {"start": v(-8.75, 5.54) * mm, "end": v(-8.7, 5.47) * mm});
            skLineSegment(sketch, "E451", {"start": v(-8.7, 5.47) * mm, "end": v(-8.67, 5.41) * mm});
            skLineSegment(sketch, "E452", {"start": v(-8.67, 5.41) * mm, "end": v(-8.63, 5.36) * mm});
            skLineSegment(sketch, "E453", {"start": v(-8.63, 5.36) * mm, "end": v(-8.59, 5.3) * mm});
            skLineSegment(sketch, "E454", {"start": v(-8.59, 5.3) * mm, "end": v(-8.55, 5.26) * mm});
            skLineSegment(sketch, "E455", {"start": v(-8.55, 5.26) * mm, "end": v(-8.51, 5.2) * mm});
            skLineSegment(sketch, "E456", {"start": v(-8.51, 5.2) * mm, "end": v(-8.48, 5.16) * mm});
            skLineSegment(sketch, "E457", {"start": v(-8.48, 5.16) * mm, "end": v(-8.44, 5.12) * mm});
            skLineSegment(sketch, "E458", {"start": v(-8.44, 5.12) * mm, "end": v(-8.4, 5.07) * mm});
            skLineSegment(sketch, "E459", {"start": v(-8.4, 5.07) * mm, "end": v(-8.34, 5.01) * mm});
            skLineSegment(sketch, "E460", {"start": v(-8.34, 5.01) * mm, "end": v(-8.3, 4.97) * mm});
            skLineSegment(sketch, "E461", {"start": v(-8.3, 4.97) * mm, "end": v(-8.26, 4.93) * mm});
            skLineSegment(sketch, "E462", {"start": v(-8.26, 4.93) * mm, "end": v(-8.2, 4.89) * mm});
            skLineSegment(sketch, "E463", {"start": v(-8.2, 4.89) * mm, "end": v(-8.17, 4.85) * mm});
            skLineSegment(sketch, "E464", {"start": v(-8.17, 4.85) * mm, "end": v(-8.13, 4.82) * mm});
            skLineSegment(sketch, "E465", {"start": v(-8.13, 4.82) * mm, "end": v(-8.08, 4.79) * mm});
            skLineSegment(sketch, "E466", {"start": v(-8.08, 4.79) * mm, "end": v(-7.53, 4.46) * mm});
            skArc(sketch, "E467", {"start": v(-7.53, 4.46) * mm, "mid": v(-7.52, 3.83) * mm, "end": v(-8.03, 3.47) * mm});
            skLineSegment(sketch, "E468", {"start": v(-8.03, 3.47) * mm, "end": v(-8.63, 3.73) * mm});
            skLineSegment(sketch, "E469", {"start": v(-8.63, 3.73) * mm, "end": v(-8.68, 3.74) * mm});
            skLineSegment(sketch, "E470", {"start": v(-8.68, 3.74) * mm, "end": v(-8.73, 3.76) * mm});
            skLineSegment(sketch, "E471", {"start": v(-8.73, 3.76) * mm, "end": v(-8.78, 3.77) * mm});
            skLineSegment(sketch, "E472", {"start": v(-8.78, 3.77) * mm, "end": v(-8.84, 3.78) * mm});
            skLineSegment(sketch, "E473", {"start": v(-8.84, 3.78) * mm, "end": v(-8.9, 3.8) * mm});
            skLineSegment(sketch, "E474", {"start": v(-8.9, 3.8) * mm, "end": v(-8.96, 3.8) * mm});
            skLineSegment(sketch, "E475", {"start": v(-8.96, 3.8) * mm, "end": v(-9.03, 3.81) * mm});
            skLineSegment(sketch, "E476", {"start": v(-9.03, 3.81) * mm, "end": v(-9.1, 3.82) * mm});
            skLineSegment(sketch, "E477", {"start": v(-9.1, 3.82) * mm, "end": v(-9.16, 3.82) * mm});
            skLineSegment(sketch, "E478", {"start": v(-9.16, 3.82) * mm, "end": v(-9.22, 3.83) * mm});
            skLineSegment(sketch, "E479", {"start": v(-9.22, 3.83) * mm, "end": v(-9.28, 3.83) * mm});
            skLineSegment(sketch, "E480", {"start": v(-9.28, 3.83) * mm, "end": v(-9.34, 3.83) * mm});
            skLineSegment(sketch, "E481", {"start": v(-9.34, 3.83) * mm, "end": v(-9.4, 3.83) * mm});
            skLineSegment(sketch, "E482", {"start": v(-9.4, 3.83) * mm, "end": v(-9.48, 3.83) * mm});
            skLineSegment(sketch, "E483", {"start": v(-9.48, 3.83) * mm, "end": v(-9.55, 3.83) * mm});
            skLineSegment(sketch, "E484", {"start": v(-9.55, 3.83) * mm, "end": v(-9.62, 3.82) * mm});
            skLineSegment(sketch, "E485", {"start": v(-9.62, 3.82) * mm, "end": v(-9.7, 3.82) * mm});
            skLineSegment(sketch, "E486", {"start": v(-9.7, 3.82) * mm, "end": v(-9.78, 3.81) * mm});
            skLineSegment(sketch, "E487", {"start": v(-9.78, 3.81) * mm, "end": v(-9.86, 3.8) * mm});
            skLineSegment(sketch, "E488", {"start": v(-9.86, 3.8) * mm, "end": v(-9.95, 3.8) * mm});
            skLineSegment(sketch, "E489", {"start": v(-9.95, 3.8) * mm, "end": v(-10.03, 3.78) * mm});
            skLineSegment(sketch, "E490", {"start": v(-10.03, 3.78) * mm, "end": v(-10.12, 3.77) * mm});
            skLineSegment(sketch, "E491", {"start": v(-10.12, 3.77) * mm, "end": v(-10.22, 3.75) * mm});
            skLineSegment(sketch, "E492", {"start": v(-10.22, 3.75) * mm, "end": v(-10.35, 3.73) * mm});
            skLineSegment(sketch, "E493", {"start": v(-10.35, 3.73) * mm, "end": v(-10.56, 3.07) * mm});
            skLineSegment(sketch, "E494", {"start": v(-10.56, 3.07) * mm, "end": v(-10.47, 2.97) * mm});
            skLineSegment(sketch, "E495", {"start": v(-10.47, 2.97) * mm, "end": v(-10.4, 2.9) * mm});
            skLineSegment(sketch, "E496", {"start": v(-10.4, 2.9) * mm, "end": v(-10.34, 2.84) * mm});
            skLineSegment(sketch, "E497", {"start": v(-10.34, 2.84) * mm, "end": v(-10.28, 2.78) * mm});
            skLineSegment(sketch, "E498", {"start": v(-10.28, 2.78) * mm, "end": v(-10.21, 2.72) * mm});
            skLineSegment(sketch, "E499", {"start": v(-10.21, 2.72) * mm, "end": v(-10.15, 2.66) * mm});
            skLineSegment(sketch, "E500", {"start": v(-10.15, 2.66) * mm, "end": v(-10.1, 2.61) * mm});
            skLineSegment(sketch, "E501", {"start": v(-10.1, 2.61) * mm, "end": v(-10.03, 2.56) * mm});
            skLineSegment(sketch, "E502", {"start": v(-10.03, 2.56) * mm, "end": v(-9.97, 2.52) * mm});
            skLineSegment(sketch, "E503", {"start": v(-9.97, 2.52) * mm, "end": v(-9.92, 2.47) * mm});
            skLineSegment(sketch, "E504", {"start": v(-9.92, 2.47) * mm, "end": v(-9.86, 2.43) * mm});
            skLineSegment(sketch, "E505", {"start": v(-9.86, 2.43) * mm, "end": v(-9.8, 2.4) * mm});
            skLineSegment(sketch, "E506", {"start": v(-9.8, 2.4) * mm, "end": v(-9.76, 2.36) * mm});
            skLineSegment(sketch, "E507", {"start": v(-9.76, 2.36) * mm, "end": v(-9.7, 2.32) * mm});
            skLineSegment(sketch, "E508", {"start": v(-9.7, 2.32) * mm, "end": v(-9.66, 2.3) * mm});
            skLineSegment(sketch, "E509", {"start": v(-9.66, 2.3) * mm, "end": v(-9.61, 2.26) * mm});
            skLineSegment(sketch, "E510", {"start": v(-9.61, 2.26) * mm, "end": v(-9.55, 2.22) * mm});
            skLineSegment(sketch, "E511", {"start": v(-9.55, 2.22) * mm, "end": v(-9.48, 2.2) * mm});
            skLineSegment(sketch, "E512", {"start": v(-9.48, 2.2) * mm, "end": v(-9.43, 2.16) * mm});
            skLineSegment(sketch, "E513", {"start": v(-9.43, 2.16) * mm, "end": v(-9.38, 2.14) * mm});
            skLineSegment(sketch, "E514", {"start": v(-9.38, 2.14) * mm, "end": v(-9.32, 2.11) * mm});
            skLineSegment(sketch, "E515", {"start": v(-9.32, 2.11) * mm, "end": v(-9.27, 2.09) * mm});
            skLineSegment(sketch, "E516", {"start": v(-9.27, 2.09) * mm, "end": v(-9.22, 2.07) * mm});
            skLineSegment(sketch, "E517", {"start": v(-9.22, 2.07) * mm, "end": v(-9.17, 2.06) * mm});
            skLineSegment(sketch, "E518", {"start": v(-9.17, 2.06) * mm, "end": v(-8.54, 1.92) * mm});
            skArc(sketch, "E519", {"start": v(-8.54, 1.92) * mm, "mid": v(-8.34, 1.32) * mm, "end": v(-8.71, 0.82) * mm});
            skLineSegment(sketch, "E520", {"start": v(-8.71, 0.82) * mm, "end": v(-9.36, 0.88) * mm});
            skLineSegment(sketch, "E521", {"start": v(-9.36, 0.88) * mm, "end": v(-9.4, 0.88) * mm});
            skLineSegment(sketch, "E522", {"start": v(-9.4, 0.88) * mm, "end": v(-9.46, 0.88) * mm});
            skLineSegment(sketch, "E523", {"start": v(-9.46, 0.88) * mm, "end": v(-9.51, 0.87) * mm});
            skLineSegment(sketch, "E524", {"start": v(-9.51, 0.87) * mm, "end": v(-9.58, 0.87) * mm});
            skLineSegment(sketch, "E525", {"start": v(-9.58, 0.87) * mm, "end": v(-9.64, 0.86) * mm});
            skLineSegment(sketch, "E526", {"start": v(-9.64, 0.86) * mm, "end": v(-9.7, 0.85) * mm});
            skLineSegment(sketch, "E527", {"start": v(-9.7, 0.85) * mm, "end": v(-9.77, 0.83) * mm});
            skLineSegment(sketch, "E528", {"start": v(-9.77, 0.83) * mm, "end": v(-9.84, 0.82) * mm});
            skLineSegment(sketch, "E529", {"start": v(-9.84, 0.82) * mm, "end": v(-9.9, 0.8) * mm});
            skLineSegment(sketch, "E530", {"start": v(-9.9, 0.8) * mm, "end": v(-9.95, 0.8) * mm});
            skLineSegment(sketch, "E531", {"start": v(-9.95, 0.8) * mm, "end": v(-10, 0.77) * mm});
            skLineSegment(sketch, "E532", {"start": v(-10, 0.77) * mm, "end": v(-10.07, 0.76) * mm});
            skLineSegment(sketch, "E533", {"start": v(-10.07, 0.76) * mm, "end": v(-10.13, 0.74) * mm});
            skLineSegment(sketch, "E534", {"start": v(-10.13, 0.74) * mm, "end": v(-10.2, 0.71) * mm});
            skLineSegment(sketch, "E535", {"start": v(-10.2, 0.71) * mm, "end": v(-10.26, 0.7) * mm});
            skLineSegment(sketch, "E536", {"start": v(-10.26, 0.7) * mm, "end": v(-10.33, 0.66) * mm});
            skLineSegment(sketch, "E537", {"start": v(-10.33, 0.66) * mm, "end": v(-10.4, 0.64) * mm});
            skLineSegment(sketch, "E538", {"start": v(-10.4, 0.64) * mm, "end": v(-10.48, 0.6) * mm});
            skLineSegment(sketch, "E539", {"start": v(-10.48, 0.6) * mm, "end": v(-10.55, 0.57) * mm});
            skLineSegment(sketch, "E540", {"start": v(-10.55, 0.57) * mm, "end": v(-10.63, 0.54) * mm});
            skLineSegment(sketch, "E541", {"start": v(-10.63, 0.54) * mm, "end": v(-10.71, 0.5) * mm});
            skLineSegment(sketch, "E542", {"start": v(-10.71, 0.5) * mm, "end": v(-10.8, 0.46) * mm});
            skLineSegment(sketch, "E543", {"start": v(-10.8, 0.46) * mm, "end": v(-10.88, 0.41) * mm});
            skLineSegment(sketch, "E544", {"start": v(-10.88, 0.41) * mm, "end": v(-11, 0.35) * mm});
            skLineSegment(sketch, "E545", {"start": v(-11, 0.35) * mm, "end": v(-11, -0.35) * mm});
            skLineSegment(sketch, "E546", {"start": v(-11, -0.35) * mm, "end": v(-10.88, -0.41) * mm});
            skLineSegment(sketch, "E547", {"start": v(-10.88, -0.41) * mm, "end": v(-10.8, -0.46) * mm});
            skLineSegment(sketch, "E548", {"start": v(-10.8, -0.46) * mm, "end": v(-10.71, -0.5) * mm});
            skLineSegment(sketch, "E549", {"start": v(-10.71, -0.5) * mm, "end": v(-10.63, -0.54) * mm});
            skLineSegment(sketch, "E550", {"start": v(-10.63, -0.54) * mm, "end": v(-10.55, -0.57) * mm});
            skLineSegment(sketch, "E551", {"start": v(-10.55, -0.57) * mm, "end": v(-10.48, -0.6) * mm});
            skLineSegment(sketch, "E552", {"start": v(-10.48, -0.6) * mm, "end": v(-10.4, -0.64) * mm});
            skLineSegment(sketch, "E553", {"start": v(-10.4, -0.64) * mm, "end": v(-10.33, -0.66) * mm});
            skLineSegment(sketch, "E554", {"start": v(-10.33, -0.66) * mm, "end": v(-10.26, -0.7) * mm});
            skLineSegment(sketch, "E555", {"start": v(-10.26, -0.7) * mm, "end": v(-10.2, -0.71) * mm});
            skLineSegment(sketch, "E556", {"start": v(-10.2, -0.71) * mm, "end": v(-10.13, -0.74) * mm});
            skLineSegment(sketch, "E557", {"start": v(-10.13, -0.74) * mm, "end": v(-10.07, -0.76) * mm});
            skLineSegment(sketch, "E558", {"start": v(-10.07, -0.76) * mm, "end": v(-10, -0.77) * mm});
            skLineSegment(sketch, "E559", {"start": v(-10, -0.77) * mm, "end": v(-9.95, -0.8) * mm});
            skLineSegment(sketch, "E560", {"start": v(-9.95, -0.8) * mm, "end": v(-9.9, -0.8) * mm});
            skLineSegment(sketch, "E561", {"start": v(-9.9, -0.8) * mm, "end": v(-9.84, -0.82) * mm});
            skLineSegment(sketch, "E562", {"start": v(-9.84, -0.82) * mm, "end": v(-9.77, -0.83) * mm});
            skLineSegment(sketch, "E563", {"start": v(-9.77, -0.83) * mm, "end": v(-9.7, -0.85) * mm});
            skLineSegment(sketch, "E564", {"start": v(-9.7, -0.85) * mm, "end": v(-9.64, -0.86) * mm});
            skLineSegment(sketch, "E565", {"start": v(-9.64, -0.86) * mm, "end": v(-9.58, -0.87) * mm});
            skLineSegment(sketch, "E566", {"start": v(-9.58, -0.87) * mm, "end": v(-9.51, -0.87) * mm});
            skLineSegment(sketch, "E567", {"start": v(-9.51, -0.87) * mm, "end": v(-9.46, -0.88) * mm});
            skLineSegment(sketch, "E568", {"start": v(-9.46, -0.88) * mm, "end": v(-9.4, -0.88) * mm});
            skLineSegment(sketch, "E569", {"start": v(-9.4, -0.88) * mm, "end": v(-9.36, -0.88) * mm});
            skLineSegment(sketch, "E570", {"start": v(-9.36, -0.88) * mm, "end": v(-8.71, -0.82) * mm});
            skArc(sketch, "E571", {"start": v(-8.71, -0.82) * mm, "mid": v(-8.34, -1.32) * mm, "end": v(-8.54, -1.92) * mm});
            skLineSegment(sketch, "E572", {"start": v(-8.54, -1.92) * mm, "end": v(-9.17, -2.06) * mm});
            skLineSegment(sketch, "E573", {"start": v(-9.17, -2.06) * mm, "end": v(-9.22, -2.07) * mm});
            skLineSegment(sketch, "E574", {"start": v(-9.22, -2.07) * mm, "end": v(-9.27, -2.09) * mm});
            skLineSegment(sketch, "E575", {"start": v(-9.27, -2.09) * mm, "end": v(-9.32, -2.11) * mm});
            skLineSegment(sketch, "E576", {"start": v(-9.32, -2.11) * mm, "end": v(-9.38, -2.14) * mm});
            skLineSegment(sketch, "E577", {"start": v(-9.38, -2.14) * mm, "end": v(-9.43, -2.16) * mm});
            skLineSegment(sketch, "E578", {"start": v(-9.43, -2.16) * mm, "end": v(-9.48, -2.2) * mm});
            skLineSegment(sketch, "E579", {"start": v(-9.48, -2.2) * mm, "end": v(-9.55, -2.22) * mm});
            skLineSegment(sketch, "E580", {"start": v(-9.55, -2.22) * mm, "end": v(-9.61, -2.26) * mm});
            skLineSegment(sketch, "E581", {"start": v(-9.61, -2.26) * mm, "end": v(-9.66, -2.3) * mm});
            skLineSegment(sketch, "E582", {"start": v(-9.66, -2.3) * mm, "end": v(-9.7, -2.32) * mm});
            skLineSegment(sketch, "E583", {"start": v(-9.7, -2.32) * mm, "end": v(-9.76, -2.36) * mm});
            skLineSegment(sketch, "E584", {"start": v(-9.76, -2.36) * mm, "end": v(-9.8, -2.4) * mm});
            skLineSegment(sketch, "E585", {"start": v(-9.8, -2.4) * mm, "end": v(-9.86, -2.43) * mm});
            skLineSegment(sketch, "E586", {"start": v(-9.86, -2.43) * mm, "end": v(-9.92, -2.47) * mm});
            skLineSegment(sketch, "E587", {"start": v(-9.92, -2.47) * mm, "end": v(-9.97, -2.52) * mm});
            skLineSegment(sketch, "E588", {"start": v(-9.97, -2.52) * mm, "end": v(-10.03, -2.56) * mm});
            skLineSegment(sketch, "E589", {"start": v(-10.03, -2.56) * mm, "end": v(-10.1, -2.61) * mm});
            skLineSegment(sketch, "E590", {"start": v(-10.1, -2.61) * mm, "end": v(-10.15, -2.66) * mm});
            skLineSegment(sketch, "E591", {"start": v(-10.15, -2.66) * mm, "end": v(-10.21, -2.72) * mm});
            skLineSegment(sketch, "E592", {"start": v(-10.21, -2.72) * mm, "end": v(-10.28, -2.78) * mm});
            skLineSegment(sketch, "E593", {"start": v(-10.28, -2.78) * mm, "end": v(-10.34, -2.84) * mm});
            skLineSegment(sketch, "E594", {"start": v(-10.34, -2.84) * mm, "end": v(-10.4, -2.9) * mm});
            skLineSegment(sketch, "E595", {"start": v(-10.4, -2.9) * mm, "end": v(-10.47, -2.97) * mm});
            skLineSegment(sketch, "E596", {"start": v(-10.47, -2.97) * mm, "end": v(-10.56, -3.07) * mm});
            skLineSegment(sketch, "E597", {"start": v(-10.56, -3.07) * mm, "end": v(-10.35, -3.73) * mm});
            skLineSegment(sketch, "E598", {"start": v(-10.35, -3.73) * mm, "end": v(-10.22, -3.75) * mm});
            skLineSegment(sketch, "E599", {"start": v(-10.22, -3.75) * mm, "end": v(-10.12, -3.77) * mm});
            skLineSegment(sketch, "E600", {"start": v(-10.12, -3.77) * mm, "end": v(-10.03, -3.78) * mm});
            skLineSegment(sketch, "E601", {"start": v(-10.03, -3.78) * mm, "end": v(-9.95, -3.8) * mm});
            skLineSegment(sketch, "E602", {"start": v(-9.95, -3.8) * mm, "end": v(-9.86, -3.8) * mm});
            skLineSegment(sketch, "E603", {"start": v(-9.86, -3.8) * mm, "end": v(-9.78, -3.81) * mm});
            skLineSegment(sketch, "E604", {"start": v(-9.78, -3.81) * mm, "end": v(-9.7, -3.82) * mm});
            skLineSegment(sketch, "E605", {"start": v(-9.7, -3.82) * mm, "end": v(-9.62, -3.82) * mm});
            skLineSegment(sketch, "E606", {"start": v(-9.62, -3.82) * mm, "end": v(-9.55, -3.83) * mm});
            skLineSegment(sketch, "E607", {"start": v(-9.55, -3.83) * mm, "end": v(-9.48, -3.83) * mm});
            skLineSegment(sketch, "E608", {"start": v(-9.48, -3.83) * mm, "end": v(-9.4, -3.83) * mm});
            skLineSegment(sketch, "E609", {"start": v(-9.4, -3.83) * mm, "end": v(-9.34, -3.83) * mm});
            skLineSegment(sketch, "E610", {"start": v(-9.34, -3.83) * mm, "end": v(-9.28, -3.83) * mm});
            skLineSegment(sketch, "E611", {"start": v(-9.28, -3.83) * mm, "end": v(-9.22, -3.83) * mm});
            skLineSegment(sketch, "E612", {"start": v(-9.22, -3.83) * mm, "end": v(-9.16, -3.82) * mm});
            skLineSegment(sketch, "E613", {"start": v(-9.16, -3.82) * mm, "end": v(-9.1, -3.82) * mm});
            skLineSegment(sketch, "E614", {"start": v(-9.1, -3.82) * mm, "end": v(-9.03, -3.81) * mm});
            skLineSegment(sketch, "E615", {"start": v(-9.03, -3.81) * mm, "end": v(-8.96, -3.8) * mm});
            skLineSegment(sketch, "E616", {"start": v(-8.96, -3.8) * mm, "end": v(-8.9, -3.8) * mm});
            skLineSegment(sketch, "E617", {"start": v(-8.9, -3.8) * mm, "end": v(-8.84, -3.78) * mm});
            skLineSegment(sketch, "E618", {"start": v(-8.84, -3.78) * mm, "end": v(-8.78, -3.77) * mm});
            skLineSegment(sketch, "E619", {"start": v(-8.78, -3.77) * mm, "end": v(-8.73, -3.76) * mm});
            skLineSegment(sketch, "E620", {"start": v(-8.73, -3.76) * mm, "end": v(-8.68, -3.74) * mm});
            skLineSegment(sketch, "E621", {"start": v(-8.68, -3.74) * mm, "end": v(-8.63, -3.73) * mm});
            skLineSegment(sketch, "E622", {"start": v(-8.63, -3.73) * mm, "end": v(-8.03, -3.47) * mm});
            skArc(sketch, "E623", {"start": v(-8.03, -3.47) * mm, "mid": v(-7.52, -3.83) * mm, "end": v(-7.53, -4.46) * mm});
            skLineSegment(sketch, "E624", {"start": v(-7.53, -4.46) * mm, "end": v(-8.08, -4.79) * mm});
            skLineSegment(sketch, "E625", {"start": v(-8.08, -4.79) * mm, "end": v(-8.13, -4.82) * mm});
            skLineSegment(sketch, "E626", {"start": v(-8.13, -4.82) * mm, "end": v(-8.17, -4.85) * mm});
            skLineSegment(sketch, "E627", {"start": v(-8.17, -4.85) * mm, "end": v(-8.2, -4.89) * mm});
            skLineSegment(sketch, "E628", {"start": v(-8.2, -4.89) * mm, "end": v(-8.26, -4.93) * mm});
            skLineSegment(sketch, "E629", {"start": v(-8.26, -4.93) * mm, "end": v(-8.3, -4.97) * mm});
            skLineSegment(sketch, "E630", {"start": v(-8.3, -4.97) * mm, "end": v(-8.34, -5.01) * mm});
            skLineSegment(sketch, "E631", {"start": v(-8.34, -5.01) * mm, "end": v(-8.4, -5.07) * mm});
            skLineSegment(sketch, "E632", {"start": v(-8.4, -5.07) * mm, "end": v(-8.44, -5.12) * mm});
            skLineSegment(sketch, "E633", {"start": v(-8.44, -5.12) * mm, "end": v(-8.48, -5.16) * mm});
            skLineSegment(sketch, "E634", {"start": v(-8.48, -5.16) * mm, "end": v(-8.51, -5.2) * mm});
            skLineSegment(sketch, "E635", {"start": v(-8.51, -5.2) * mm, "end": v(-8.55, -5.26) * mm});
            skLineSegment(sketch, "E636", {"start": v(-8.55, -5.26) * mm, "end": v(-8.59, -5.3) * mm});
            skLineSegment(sketch, "E637", {"start": v(-8.59, -5.3) * mm, "end": v(-8.63, -5.36) * mm});
            skLineSegment(sketch, "E638", {"start": v(-8.63, -5.36) * mm, "end": v(-8.67, -5.41) * mm});
            skLineSegment(sketch, "E639", {"start": v(-8.67, -5.41) * mm, "end": v(-8.7, -5.47) * mm});
            skLineSegment(sketch, "E640", {"start": v(-8.7, -5.47) * mm, "end": v(-8.75, -5.54) * mm});
            skLineSegment(sketch, "E641", {"start": v(-8.75, -5.54) * mm, "end": v(-8.8, -5.6) * mm});
            skLineSegment(sketch, "E642", {"start": v(-8.8, -5.6) * mm, "end": v(-8.83, -5.67) * mm});
            skLineSegment(sketch, "E643", {"start": v(-8.83, -5.67) * mm, "end": v(-8.87, -5.74) * mm});
            skLineSegment(sketch, "E644", {"start": v(-8.87, -5.74) * mm, "end": v(-8.92, -5.82) * mm});
            skLineSegment(sketch, "E645", {"start": v(-8.92, -5.82) * mm, "end": v(-8.96, -5.9) * mm});
            skLineSegment(sketch, "E646", {"start": v(-8.96, -5.9) * mm, "end": v(-9, -5.98) * mm});
            skLineSegment(sketch, "E647", {"start": v(-9, -5.98) * mm, "end": v(-9.04, -6.06) * mm});
            skLineSegment(sketch, "E648", {"start": v(-9.04, -6.06) * mm, "end": v(-9.1, -6.18) * mm});
            skLineSegment(sketch, "E649", {"start": v(-9.1, -6.18) * mm, "end": v(-8.7, -6.74) * mm});
            skLineSegment(sketch, "E650", {"start": v(-8.7, -6.74) * mm, "end": v(-8.56, -6.73) * mm});
            skLineSegment(sketch, "E651", {"start": v(-8.56, -6.73) * mm, "end": v(-8.46, -6.71) * mm});
            skLineSegment(sketch, "E652", {"start": v(-8.46, -6.71) * mm, "end": v(-8.37, -6.7) * mm});
            skLineSegment(sketch, "E653", {"start": v(-8.37, -6.7) * mm, "end": v(-8.29, -6.68) * mm});
            skLineSegment(sketch, "E654", {"start": v(-8.29, -6.68) * mm, "end": v(-8.2, -6.67) * mm});
            skLineSegment(sketch, "E655", {"start": v(-8.2, -6.67) * mm, "end": v(-8.12, -6.65) * mm});
            skLineSegment(sketch, "E656", {"start": v(-8.12, -6.65) * mm, "end": v(-8.04, -6.63) * mm});
            skLineSegment(sketch, "E657", {"start": v(-8.04, -6.63) * mm, "end": v(-7.97, -6.61) * mm});
            skLineSegment(sketch, "E658", {"start": v(-7.97, -6.61) * mm, "end": v(-7.9, -6.6) * mm});
            skLineSegment(sketch, "E659", {"start": v(-7.9, -6.6) * mm, "end": v(-7.83, -6.57) * mm});
            skLineSegment(sketch, "E660", {"start": v(-7.83, -6.57) * mm, "end": v(-7.76, -6.55) * mm});
            skLineSegment(sketch, "E661", {"start": v(-7.76, -6.55) * mm, "end": v(-7.7, -6.53) * mm});
            skLineSegment(sketch, "E662", {"start": v(-7.7, -6.53) * mm, "end": v(-7.64, -6.5) * mm});
            skLineSegment(sketch, "E663", {"start": v(-7.64, -6.5) * mm, "end": v(-7.58, -6.49) * mm});
            skLineSegment(sketch, "E664", {"start": v(-7.58, -6.49) * mm, "end": v(-7.53, -6.47) * mm});
            skLineSegment(sketch, "E665", {"start": v(-7.53, -6.47) * mm, "end": v(-7.48, -6.45) * mm});
            skLineSegment(sketch, "E666", {"start": v(-7.48, -6.45) * mm, "end": v(-7.41, -6.42) * mm});
            skLineSegment(sketch, "E667", {"start": v(-7.41, -6.42) * mm, "end": v(-7.35, -6.39) * mm});
            skLineSegment(sketch, "E668", {"start": v(-7.35, -6.39) * mm, "end": v(-7.3, -6.36) * mm});
            skLineSegment(sketch, "E669", {"start": v(-7.3, -6.36) * mm, "end": v(-7.24, -6.33) * mm});
            skLineSegment(sketch, "E670", {"start": v(-7.24, -6.33) * mm, "end": v(-7.18, -6.3) * mm});
            skLineSegment(sketch, "E671", {"start": v(-7.18, -6.3) * mm, "end": v(-7.14, -6.27) * mm});
            skLineSegment(sketch, "E672", {"start": v(-7.14, -6.27) * mm, "end": v(-7.1, -6.24) * mm});
            skLineSegment(sketch, "E673", {"start": v(-7.1, -6.24) * mm, "end": v(-7.05, -6.2) * mm});
            skLineSegment(sketch, "E674", {"start": v(-7.05, -6.2) * mm, "end": v(-6.57, -5.78) * mm});
            skArc(sketch, "E675", {"start": v(-6.57, -5.78) * mm, "mid": v(-5.97, -5.97) * mm, "end": v(-5.78, -6.57) * mm});
            skLineSegment(sketch, "E676", {"start": v(-5.78, -6.57) * mm, "end": v(-6.2, -7.05) * mm});
            skLineSegment(sketch, "E677", {"start": v(-6.2, -7.05) * mm, "end": v(-6.24, -7.1) * mm});
            skLineSegment(sketch, "E678", {"start": v(-6.24, -7.1) * mm, "end": v(-6.27, -7.14) * mm});
            skLineSegment(sketch, "E679", {"start": v(-6.27, -7.14) * mm, "end": v(-6.3, -7.18) * mm});
            skLineSegment(sketch, "E680", {"start": v(-6.3, -7.18) * mm, "end": v(-6.33, -7.24) * mm});
            skLineSegment(sketch, "E681", {"start": v(-6.33, -7.24) * mm, "end": v(-6.36, -7.3) * mm});
            skLineSegment(sketch, "E682", {"start": v(-6.36, -7.3) * mm, "end": v(-6.39, -7.35) * mm});
            skLineSegment(sketch, "E683", {"start": v(-6.39, -7.35) * mm, "end": v(-6.42, -7.41) * mm});
            skLineSegment(sketch, "E684", {"start": v(-6.42, -7.41) * mm, "end": v(-6.45, -7.48) * mm});
            skLineSegment(sketch, "E685", {"start": v(-6.45, -7.48) * mm, "end": v(-6.47, -7.53) * mm});
            skLineSegment(sketch, "E686", {"start": v(-6.47, -7.53) * mm, "end": v(-6.49, -7.58) * mm});
            skLineSegment(sketch, "E687", {"start": v(-6.49, -7.58) * mm, "end": v(-6.5, -7.64) * mm});
            skLineSegment(sketch, "E688", {"start": v(-6.5, -7.64) * mm, "end": v(-6.53, -7.7) * mm});
            skLineSegment(sketch, "E689", {"start": v(-6.53, -7.7) * mm, "end": v(-6.55, -7.76) * mm});
            skLineSegment(sketch, "E690", {"start": v(-6.55, -7.76) * mm, "end": v(-6.57, -7.83) * mm});
            skLineSegment(sketch, "E691", {"start": v(-6.57, -7.83) * mm, "end": v(-6.6, -7.9) * mm});
            skLineSegment(sketch, "E692", {"start": v(-6.6, -7.9) * mm, "end": v(-6.61, -7.97) * mm});
            skLineSegment(sketch, "E693", {"start": v(-6.61, -7.97) * mm, "end": v(-6.63, -8.04) * mm});
            skLineSegment(sketch, "E694", {"start": v(-6.63, -8.04) * mm, "end": v(-6.65, -8.12) * mm});
            skLineSegment(sketch, "E695", {"start": v(-6.65, -8.12) * mm, "end": v(-6.67, -8.2) * mm});
            skLineSegment(sketch, "E696", {"start": v(-6.67, -8.2) * mm, "end": v(-6.68, -8.29) * mm});
            skLineSegment(sketch, "E697", {"start": v(-6.68, -8.29) * mm, "end": v(-6.7, -8.37) * mm});
            skLineSegment(sketch, "E698", {"start": v(-6.7, -8.37) * mm, "end": v(-6.71, -8.46) * mm});
            skLineSegment(sketch, "E699", {"start": v(-6.71, -8.46) * mm, "end": v(-6.73, -8.56) * mm});
            skLineSegment(sketch, "E700", {"start": v(-6.73, -8.56) * mm, "end": v(-6.74, -8.7) * mm});
            skLineSegment(sketch, "E701", {"start": v(-6.74, -8.7) * mm, "end": v(-6.18, -9.1) * mm});
            skLineSegment(sketch, "E702", {"start": v(-6.18, -9.1) * mm, "end": v(-6.06, -9.04) * mm});
            skLineSegment(sketch, "E703", {"start": v(-6.06, -9.04) * mm, "end": v(-5.98, -9) * mm});
            skLineSegment(sketch, "E704", {"start": v(-5.98, -9) * mm, "end": v(-5.9, -8.96) * mm});
            skLineSegment(sketch, "E705", {"start": v(-5.9, -8.96) * mm, "end": v(-5.82, -8.92) * mm});
            skLineSegment(sketch, "E706", {"start": v(-5.82, -8.92) * mm, "end": v(-5.74, -8.87) * mm});
            skLineSegment(sketch, "E707", {"start": v(-5.74, -8.87) * mm, "end": v(-5.67, -8.83) * mm});
            skLineSegment(sketch, "E708", {"start": v(-5.67, -8.83) * mm, "end": v(-5.6, -8.8) * mm});
            skLineSegment(sketch, "E709", {"start": v(-5.6, -8.8) * mm, "end": v(-5.54, -8.75) * mm});
            skLineSegment(sketch, "E710", {"start": v(-5.54, -8.75) * mm, "end": v(-5.47, -8.7) * mm});
            skLineSegment(sketch, "E711", {"start": v(-5.47, -8.7) * mm, "end": v(-5.41, -8.67) * mm});
            skLineSegment(sketch, "E712", {"start": v(-5.41, -8.67) * mm, "end": v(-5.36, -8.63) * mm});
            skLineSegment(sketch, "E713", {"start": v(-5.36, -8.63) * mm, "end": v(-5.3, -8.59) * mm});
            skLineSegment(sketch, "E714", {"start": v(-5.3, -8.59) * mm, "end": v(-5.26, -8.55) * mm});
            skLineSegment(sketch, "E715", {"start": v(-5.26, -8.55) * mm, "end": v(-5.2, -8.51) * mm});
            skLineSegment(sketch, "E716", {"start": v(-5.2, -8.51) * mm, "end": v(-5.16, -8.48) * mm});
            skLineSegment(sketch, "E717", {"start": v(-5.16, -8.48) * mm, "end": v(-5.12, -8.44) * mm});
            skLineSegment(sketch, "E718", {"start": v(-5.12, -8.44) * mm, "end": v(-5.07, -8.4) * mm});
            skLineSegment(sketch, "E719", {"start": v(-5.07, -8.4) * mm, "end": v(-5.01, -8.34) * mm});
            skLineSegment(sketch, "E720", {"start": v(-5.01, -8.34) * mm, "end": v(-4.97, -8.3) * mm});
            skLineSegment(sketch, "E721", {"start": v(-4.97, -8.3) * mm, "end": v(-4.93, -8.26) * mm});
            skLineSegment(sketch, "E722", {"start": v(-4.93, -8.26) * mm, "end": v(-4.89, -8.2) * mm});
            skLineSegment(sketch, "E723", {"start": v(-4.89, -8.2) * mm, "end": v(-4.85, -8.17) * mm});
            skLineSegment(sketch, "E724", {"start": v(-4.85, -8.17) * mm, "end": v(-4.82, -8.13) * mm});
            skLineSegment(sketch, "E725", {"start": v(-4.82, -8.13) * mm, "end": v(-4.79, -8.08) * mm});
            skLineSegment(sketch, "E726", {"start": v(-4.79, -8.08) * mm, "end": v(-4.46, -7.53) * mm});
            skArc(sketch, "E727", {"start": v(-4.46, -7.53) * mm, "mid": v(-3.83, -7.52) * mm, "end": v(-3.47, -8.03) * mm});
            skLineSegment(sketch, "E728", {"start": v(-3.47, -8.03) * mm, "end": v(-3.73, -8.63) * mm});
            skLineSegment(sketch, "E729", {"start": v(-3.73, -8.63) * mm, "end": v(-3.74, -8.68) * mm});
            skLineSegment(sketch, "E730", {"start": v(-3.74, -8.68) * mm, "end": v(-3.76, -8.73) * mm});
            skLineSegment(sketch, "E731", {"start": v(-3.76, -8.73) * mm, "end": v(-3.77, -8.78) * mm});
            skLineSegment(sketch, "E732", {"start": v(-3.77, -8.78) * mm, "end": v(-3.78, -8.84) * mm});
            skLineSegment(sketch, "E733", {"start": v(-3.78, -8.84) * mm, "end": v(-3.8, -8.9) * mm});
            skLineSegment(sketch, "E734", {"start": v(-3.8, -8.9) * mm, "end": v(-3.8, -8.96) * mm});
            skLineSegment(sketch, "E735", {"start": v(-3.8, -8.96) * mm, "end": v(-3.81, -9.03) * mm});
            skLineSegment(sketch, "E736", {"start": v(-3.81, -9.03) * mm, "end": v(-3.82, -9.1) * mm});
            skLineSegment(sketch, "E737", {"start": v(-3.82, -9.1) * mm, "end": v(-3.82, -9.16) * mm});
            skLineSegment(sketch, "E738", {"start": v(-3.82, -9.16) * mm, "end": v(-3.83, -9.22) * mm});
            skLineSegment(sketch, "E739", {"start": v(-3.83, -9.22) * mm, "end": v(-3.83, -9.28) * mm});
            skLineSegment(sketch, "E740", {"start": v(-3.83, -9.28) * mm, "end": v(-3.83, -9.34) * mm});
            skLineSegment(sketch, "E741", {"start": v(-3.83, -9.34) * mm, "end": v(-3.83, -9.4) * mm});
            skLineSegment(sketch, "E742", {"start": v(-3.83, -9.4) * mm, "end": v(-3.83, -9.48) * mm});
            skLineSegment(sketch, "E743", {"start": v(-3.83, -9.48) * mm, "end": v(-3.83, -9.55) * mm});
            skLineSegment(sketch, "E744", {"start": v(-3.83, -9.55) * mm, "end": v(-3.82, -9.62) * mm});
            skLineSegment(sketch, "E745", {"start": v(-3.82, -9.62) * mm, "end": v(-3.82, -9.7) * mm});
            skLineSegment(sketch, "E746", {"start": v(-3.82, -9.7) * mm, "end": v(-3.81, -9.78) * mm});
            skLineSegment(sketch, "E747", {"start": v(-3.81, -9.78) * mm, "end": v(-3.8, -9.86) * mm});
            skLineSegment(sketch, "E748", {"start": v(-3.8, -9.86) * mm, "end": v(-3.8, -9.95) * mm});
            skLineSegment(sketch, "E749", {"start": v(-3.8, -9.95) * mm, "end": v(-3.78, -10.03) * mm});
            skLineSegment(sketch, "E750", {"start": v(-3.78, -10.03) * mm, "end": v(-3.77, -10.12) * mm});
            skLineSegment(sketch, "E751", {"start": v(-3.77, -10.12) * mm, "end": v(-3.75, -10.22) * mm});
            skLineSegment(sketch, "E752", {"start": v(-3.75, -10.22) * mm, "end": v(-3.73, -10.35) * mm});
            skLineSegment(sketch, "E753", {"start": v(-3.73, -10.35) * mm, "end": v(-3.07, -10.56) * mm});
            skLineSegment(sketch, "E754", {"start": v(-3.07, -10.56) * mm, "end": v(-2.97, -10.47) * mm});
            skLineSegment(sketch, "E755", {"start": v(-2.97, -10.47) * mm, "end": v(-2.9, -10.4) * mm});
            skLineSegment(sketch, "E756", {"start": v(-2.9, -10.4) * mm, "end": v(-2.84, -10.34) * mm});
            skLineSegment(sketch, "E757", {"start": v(-2.84, -10.34) * mm, "end": v(-2.78, -10.28) * mm});
            skLineSegment(sketch, "E758", {"start": v(-2.78, -10.28) * mm, "end": v(-2.72, -10.21) * mm});
            skLineSegment(sketch, "E759", {"start": v(-2.72, -10.21) * mm, "end": v(-2.66, -10.15) * mm});
            skLineSegment(sketch, "E760", {"start": v(-2.66, -10.15) * mm, "end": v(-2.61, -10.1) * mm});
            skLineSegment(sketch, "E761", {"start": v(-2.61, -10.1) * mm, "end": v(-2.56, -10.03) * mm});
            skLineSegment(sketch, "E762", {"start": v(-2.56, -10.03) * mm, "end": v(-2.52, -9.97) * mm});
            skLineSegment(sketch, "E763", {"start": v(-2.52, -9.97) * mm, "end": v(-2.47, -9.92) * mm});
            skLineSegment(sketch, "E764", {"start": v(-2.47, -9.92) * mm, "end": v(-2.43, -9.86) * mm});
            skLineSegment(sketch, "E765", {"start": v(-2.43, -9.86) * mm, "end": v(-2.4, -9.8) * mm});
            skLineSegment(sketch, "E766", {"start": v(-2.4, -9.8) * mm, "end": v(-2.36, -9.76) * mm});
            skLineSegment(sketch, "E767", {"start": v(-2.36, -9.76) * mm, "end": v(-2.32, -9.7) * mm});
            skLineSegment(sketch, "E768", {"start": v(-2.32, -9.7) * mm, "end": v(-2.3, -9.66) * mm});
            skLineSegment(sketch, "E769", {"start": v(-2.3, -9.66) * mm, "end": v(-2.26, -9.61) * mm});
            skLineSegment(sketch, "E770", {"start": v(-2.26, -9.61) * mm, "end": v(-2.22, -9.55) * mm});
            skLineSegment(sketch, "E771", {"start": v(-2.22, -9.55) * mm, "end": v(-2.2, -9.48) * mm});
            skLineSegment(sketch, "E772", {"start": v(-2.2, -9.48) * mm, "end": v(-2.16, -9.43) * mm});
            skLineSegment(sketch, "E773", {"start": v(-2.16, -9.43) * mm, "end": v(-2.14, -9.38) * mm});
            skLineSegment(sketch, "E774", {"start": v(-2.14, -9.38) * mm, "end": v(-2.11, -9.32) * mm});
            skLineSegment(sketch, "E775", {"start": v(-2.11, -9.32) * mm, "end": v(-2.09, -9.27) * mm});
            skLineSegment(sketch, "E776", {"start": v(-2.09, -9.27) * mm, "end": v(-2.07, -9.22) * mm});
            skLineSegment(sketch, "E777", {"start": v(-2.07, -9.22) * mm, "end": v(-2.06, -9.17) * mm});
            skLineSegment(sketch, "E778", {"start": v(-2.06, -9.17) * mm, "end": v(-1.92, -8.54) * mm});
            skArc(sketch, "E779", {"start": v(-1.92, -8.54) * mm, "mid": v(-1.32, -8.34) * mm, "end": v(-0.82, -8.71) * mm});
            skLineSegment(sketch, "E780", {"start": v(-0.82, -8.71) * mm, "end": v(-0.88, -9.36) * mm});
            skLineSegment(sketch, "E781", {"start": v(-0.88, -9.36) * mm, "end": v(-0.88, -9.4) * mm});
            skLineSegment(sketch, "E782", {"start": v(-0.88, -9.4) * mm, "end": v(-0.88, -9.46) * mm});
            skLineSegment(sketch, "E783", {"start": v(-0.88, -9.46) * mm, "end": v(-0.87, -9.51) * mm});
            skLineSegment(sketch, "E784", {"start": v(-0.87, -9.51) * mm, "end": v(-0.87, -9.58) * mm});
            skLineSegment(sketch, "E785", {"start": v(-0.87, -9.58) * mm, "end": v(-0.86, -9.64) * mm});
            skLineSegment(sketch, "E786", {"start": v(-0.86, -9.64) * mm, "end": v(-0.85, -9.7) * mm});
            skLineSegment(sketch, "E787", {"start": v(-0.85, -9.7) * mm, "end": v(-0.83, -9.77) * mm});
            skLineSegment(sketch, "E788", {"start": v(-0.83, -9.77) * mm, "end": v(-0.82, -9.84) * mm});
            skLineSegment(sketch, "E789", {"start": v(-0.82, -9.84) * mm, "end": v(-0.8, -9.9) * mm});
            skLineSegment(sketch, "E790", {"start": v(-0.8, -9.9) * mm, "end": v(-0.8, -9.95) * mm});
            skLineSegment(sketch, "E791", {"start": v(-0.8, -9.95) * mm, "end": v(-0.77, -10) * mm});
            skLineSegment(sketch, "E792", {"start": v(-0.77, -10) * mm, "end": v(-0.76, -10.07) * mm});
            skLineSegment(sketch, "E793", {"start": v(-0.76, -10.07) * mm, "end": v(-0.74, -10.13) * mm});
            skLineSegment(sketch, "E794", {"start": v(-0.74, -10.13) * mm, "end": v(-0.71, -10.2) * mm});
            skLineSegment(sketch, "E795", {"start": v(-0.71, -10.2) * mm, "end": v(-0.7, -10.26) * mm});
            skLineSegment(sketch, "E796", {"start": v(-0.7, -10.26) * mm, "end": v(-0.66, -10.33) * mm});
            skLineSegment(sketch, "E797", {"start": v(-0.66, -10.33) * mm, "end": v(-0.64, -10.4) * mm});
            skLineSegment(sketch, "E798", {"start": v(-0.64, -10.4) * mm, "end": v(-0.6, -10.48) * mm});
            skLineSegment(sketch, "E799", {"start": v(-0.6, -10.48) * mm, "end": v(-0.57, -10.55) * mm});
            skLineSegment(sketch, "E800", {"start": v(-0.57, -10.55) * mm, "end": v(-0.54, -10.63) * mm});
            skLineSegment(sketch, "E801", {"start": v(-0.54, -10.63) * mm, "end": v(-0.5, -10.71) * mm});
            skLineSegment(sketch, "E802", {"start": v(-0.5, -10.71) * mm, "end": v(-0.46, -10.8) * mm});
            skLineSegment(sketch, "E803", {"start": v(-0.46, -10.8) * mm, "end": v(-0.41, -10.88) * mm});
            skLineSegment(sketch, "E804", {"start": v(-0.41, -10.88) * mm, "end": v(-0.35, -11) * mm});
            skLineSegment(sketch, "E805", {"start": v(-0.35, -11) * mm, "end": v(0.35, -11) * mm});
            skLineSegment(sketch, "E806", {"start": v(0.35, -11) * mm, "end": v(0.41, -10.88) * mm});
            skLineSegment(sketch, "E807", {"start": v(0.41, -10.88) * mm, "end": v(0.46, -10.8) * mm});
            skLineSegment(sketch, "E808", {"start": v(0.46, -10.8) * mm, "end": v(0.5, -10.71) * mm});
            skLineSegment(sketch, "E809", {"start": v(0.5, -10.71) * mm, "end": v(0.54, -10.63) * mm});
            skLineSegment(sketch, "E810", {"start": v(0.54, -10.63) * mm, "end": v(0.57, -10.55) * mm});
            skLineSegment(sketch, "E811", {"start": v(0.57, -10.55) * mm, "end": v(0.6, -10.48) * mm});
            skLineSegment(sketch, "E812", {"start": v(0.6, -10.48) * mm, "end": v(0.64, -10.4) * mm});
            skLineSegment(sketch, "E813", {"start": v(0.64, -10.4) * mm, "end": v(0.66, -10.33) * mm});
            skLineSegment(sketch, "E814", {"start": v(0.66, -10.33) * mm, "end": v(0.7, -10.26) * mm});
            skLineSegment(sketch, "E815", {"start": v(0.7, -10.26) * mm, "end": v(0.71, -10.2) * mm});
            skLineSegment(sketch, "E816", {"start": v(0.71, -10.2) * mm, "end": v(0.74, -10.13) * mm});
            skLineSegment(sketch, "E817", {"start": v(0.74, -10.13) * mm, "end": v(0.76, -10.07) * mm});
            skLineSegment(sketch, "E818", {"start": v(0.76, -10.07) * mm, "end": v(0.77, -10) * mm});
            skLineSegment(sketch, "E819", {"start": v(0.77, -10) * mm, "end": v(0.8, -9.95) * mm});
            skLineSegment(sketch, "E820", {"start": v(0.8, -9.95) * mm, "end": v(0.8, -9.9) * mm});
            skLineSegment(sketch, "E821", {"start": v(0.8, -9.9) * mm, "end": v(0.82, -9.84) * mm});
            skLineSegment(sketch, "E822", {"start": v(0.82, -9.84) * mm, "end": v(0.83, -9.77) * mm});
            skLineSegment(sketch, "E823", {"start": v(0.83, -9.77) * mm, "end": v(0.85, -9.7) * mm});
            skLineSegment(sketch, "E824", {"start": v(0.85, -9.7) * mm, "end": v(0.86, -9.64) * mm});
            skLineSegment(sketch, "E825", {"start": v(0.86, -9.64) * mm, "end": v(0.87, -9.58) * mm});
            skLineSegment(sketch, "E826", {"start": v(0.87, -9.58) * mm, "end": v(0.87, -9.51) * mm});
            skLineSegment(sketch, "E827", {"start": v(0.87, -9.51) * mm, "end": v(0.88, -9.46) * mm});
            skLineSegment(sketch, "E828", {"start": v(0.88, -9.46) * mm, "end": v(0.88, -9.4) * mm});
            skLineSegment(sketch, "E829", {"start": v(0.88, -9.4) * mm, "end": v(0.88, -9.36) * mm});
            skLineSegment(sketch, "E830", {"start": v(0.88, -9.36) * mm, "end": v(0.82, -8.71) * mm});
            skArc(sketch, "E831", {"start": v(0.82, -8.71) * mm, "mid": v(1.32, -8.34) * mm, "end": v(1.92, -8.54) * mm});
            skLineSegment(sketch, "E832", {"start": v(1.92, -8.54) * mm, "end": v(2.06, -9.17) * mm});
            skLineSegment(sketch, "E833", {"start": v(2.06, -9.17) * mm, "end": v(2.07, -9.22) * mm});
            skLineSegment(sketch, "E834", {"start": v(2.07, -9.22) * mm, "end": v(2.09, -9.27) * mm});
            skLineSegment(sketch, "E835", {"start": v(2.09, -9.27) * mm, "end": v(2.11, -9.32) * mm});
            skLineSegment(sketch, "E836", {"start": v(2.11, -9.32) * mm, "end": v(2.14, -9.38) * mm});
            skLineSegment(sketch, "E837", {"start": v(2.14, -9.38) * mm, "end": v(2.16, -9.43) * mm});
            skLineSegment(sketch, "E838", {"start": v(2.16, -9.43) * mm, "end": v(2.2, -9.48) * mm});
            skLineSegment(sketch, "E839", {"start": v(2.2, -9.48) * mm, "end": v(2.22, -9.55) * mm});
            skLineSegment(sketch, "E840", {"start": v(2.22, -9.55) * mm, "end": v(2.26, -9.61) * mm});
            skLineSegment(sketch, "E841", {"start": v(2.26, -9.61) * mm, "end": v(2.3, -9.66) * mm});
            skLineSegment(sketch, "E842", {"start": v(2.3, -9.66) * mm, "end": v(2.32, -9.7) * mm});
            skLineSegment(sketch, "E843", {"start": v(2.32, -9.7) * mm, "end": v(2.36, -9.76) * mm});
            skLineSegment(sketch, "E844", {"start": v(2.36, -9.76) * mm, "end": v(2.4, -9.8) * mm});
            skLineSegment(sketch, "E845", {"start": v(2.4, -9.8) * mm, "end": v(2.43, -9.86) * mm});
            skLineSegment(sketch, "E846", {"start": v(2.43, -9.86) * mm, "end": v(2.47, -9.92) * mm});
            skLineSegment(sketch, "E847", {"start": v(2.47, -9.92) * mm, "end": v(2.52, -9.97) * mm});
            skLineSegment(sketch, "E848", {"start": v(2.52, -9.97) * mm, "end": v(2.56, -10.03) * mm});
            skLineSegment(sketch, "E849", {"start": v(2.56, -10.03) * mm, "end": v(2.61, -10.1) * mm});
            skLineSegment(sketch, "E850", {"start": v(2.61, -10.1) * mm, "end": v(2.66, -10.15) * mm});
            skLineSegment(sketch, "E851", {"start": v(2.66, -10.15) * mm, "end": v(2.72, -10.21) * mm});
            skLineSegment(sketch, "E852", {"start": v(2.72, -10.21) * mm, "end": v(2.78, -10.28) * mm});
            skLineSegment(sketch, "E853", {"start": v(2.78, -10.28) * mm, "end": v(2.84, -10.34) * mm});
            skLineSegment(sketch, "E854", {"start": v(2.84, -10.34) * mm, "end": v(2.9, -10.4) * mm});
            skLineSegment(sketch, "E855", {"start": v(2.9, -10.4) * mm, "end": v(2.97, -10.47) * mm});
            skLineSegment(sketch, "E856", {"start": v(2.97, -10.47) * mm, "end": v(3.07, -10.56) * mm});
            skLineSegment(sketch, "E857", {"start": v(3.07, -10.56) * mm, "end": v(3.73, -10.35) * mm});
            skLineSegment(sketch, "E858", {"start": v(3.73, -10.35) * mm, "end": v(3.75, -10.22) * mm});
            skLineSegment(sketch, "E859", {"start": v(3.75, -10.22) * mm, "end": v(3.77, -10.12) * mm});
            skLineSegment(sketch, "E860", {"start": v(3.77, -10.12) * mm, "end": v(3.78, -10.03) * mm});
            skLineSegment(sketch, "E861", {"start": v(3.78, -10.03) * mm, "end": v(3.8, -9.95) * mm});
            skLineSegment(sketch, "E862", {"start": v(3.8, -9.95) * mm, "end": v(3.8, -9.86) * mm});
            skLineSegment(sketch, "E863", {"start": v(3.8, -9.86) * mm, "end": v(3.81, -9.78) * mm});
            skLineSegment(sketch, "E864", {"start": v(3.81, -9.78) * mm, "end": v(3.82, -9.7) * mm});
            skLineSegment(sketch, "E865", {"start": v(3.82, -9.7) * mm, "end": v(3.82, -9.62) * mm});
            skLineSegment(sketch, "E866", {"start": v(3.82, -9.62) * mm, "end": v(3.83, -9.55) * mm});
            skLineSegment(sketch, "E867", {"start": v(3.83, -9.55) * mm, "end": v(3.83, -9.48) * mm});
            skLineSegment(sketch, "E868", {"start": v(3.83, -9.48) * mm, "end": v(3.83, -9.4) * mm});
            skLineSegment(sketch, "E869", {"start": v(3.83, -9.4) * mm, "end": v(3.83, -9.34) * mm});
            skLineSegment(sketch, "E870", {"start": v(3.83, -9.34) * mm, "end": v(3.83, -9.28) * mm});
            skLineSegment(sketch, "E871", {"start": v(3.83, -9.28) * mm, "end": v(3.83, -9.22) * mm});
            skLineSegment(sketch, "E872", {"start": v(3.83, -9.22) * mm, "end": v(3.82, -9.16) * mm});
            skLineSegment(sketch, "E873", {"start": v(3.82, -9.16) * mm, "end": v(3.82, -9.1) * mm});
            skLineSegment(sketch, "E874", {"start": v(3.82, -9.1) * mm, "end": v(3.81, -9.03) * mm});
            skLineSegment(sketch, "E875", {"start": v(3.81, -9.03) * mm, "end": v(3.8, -8.96) * mm});
            skLineSegment(sketch, "E876", {"start": v(3.8, -8.96) * mm, "end": v(3.8, -8.9) * mm});
            skLineSegment(sketch, "E877", {"start": v(3.8, -8.9) * mm, "end": v(3.78, -8.84) * mm});
            skLineSegment(sketch, "E878", {"start": v(3.78, -8.84) * mm, "end": v(3.77, -8.78) * mm});
            skLineSegment(sketch, "E879", {"start": v(3.77, -8.78) * mm, "end": v(3.76, -8.73) * mm});
            skLineSegment(sketch, "E880", {"start": v(3.76, -8.73) * mm, "end": v(3.74, -8.68) * mm});
            skLineSegment(sketch, "E881", {"start": v(3.74, -8.68) * mm, "end": v(3.73, -8.63) * mm});
            skLineSegment(sketch, "E882", {"start": v(3.73, -8.63) * mm, "end": v(3.47, -8.03) * mm});
            skArc(sketch, "E883", {"start": v(3.47, -8.03) * mm, "mid": v(3.83, -7.52) * mm, "end": v(4.46, -7.53) * mm});
            skLineSegment(sketch, "E884", {"start": v(4.46, -7.53) * mm, "end": v(4.79, -8.08) * mm});
            skLineSegment(sketch, "E885", {"start": v(4.79, -8.08) * mm, "end": v(4.82, -8.13) * mm});
            skLineSegment(sketch, "E886", {"start": v(4.82, -8.13) * mm, "end": v(4.85, -8.17) * mm});
            skLineSegment(sketch, "E887", {"start": v(4.85, -8.17) * mm, "end": v(4.89, -8.2) * mm});
            skLineSegment(sketch, "E888", {"start": v(4.89, -8.2) * mm, "end": v(4.93, -8.26) * mm});
            skLineSegment(sketch, "E889", {"start": v(4.93, -8.26) * mm, "end": v(4.97, -8.3) * mm});
            skLineSegment(sketch, "E890", {"start": v(4.97, -8.3) * mm, "end": v(5.01, -8.34) * mm});
            skLineSegment(sketch, "E891", {"start": v(5.01, -8.34) * mm, "end": v(5.07, -8.4) * mm});
            skLineSegment(sketch, "E892", {"start": v(5.07, -8.4) * mm, "end": v(5.12, -8.44) * mm});
            skLineSegment(sketch, "E893", {"start": v(5.12, -8.44) * mm, "end": v(5.16, -8.48) * mm});
            skLineSegment(sketch, "E894", {"start": v(5.16, -8.48) * mm, "end": v(5.2, -8.51) * mm});
            skLineSegment(sketch, "E895", {"start": v(5.2, -8.51) * mm, "end": v(5.26, -8.55) * mm});
            skLineSegment(sketch, "E896", {"start": v(5.26, -8.55) * mm, "end": v(5.3, -8.59) * mm});
            skLineSegment(sketch, "E897", {"start": v(5.3, -8.59) * mm, "end": v(5.36, -8.63) * mm});
            skLineSegment(sketch, "E898", {"start": v(5.36, -8.63) * mm, "end": v(5.41, -8.67) * mm});
            skLineSegment(sketch, "E899", {"start": v(5.41, -8.67) * mm, "end": v(5.47, -8.7) * mm});
            skLineSegment(sketch, "E900", {"start": v(5.47, -8.7) * mm, "end": v(5.54, -8.75) * mm});
            skLineSegment(sketch, "E901", {"start": v(5.54, -8.75) * mm, "end": v(5.6, -8.8) * mm});
            skLineSegment(sketch, "E902", {"start": v(5.6, -8.8) * mm, "end": v(5.67, -8.83) * mm});
            skLineSegment(sketch, "E903", {"start": v(5.67, -8.83) * mm, "end": v(5.74, -8.87) * mm});
            skLineSegment(sketch, "E904", {"start": v(5.74, -8.87) * mm, "end": v(5.82, -8.92) * mm});
            skLineSegment(sketch, "E905", {"start": v(5.82, -8.92) * mm, "end": v(5.9, -8.96) * mm});
            skLineSegment(sketch, "E906", {"start": v(5.9, -8.96) * mm, "end": v(5.98, -9) * mm});
            skLineSegment(sketch, "E907", {"start": v(5.98, -9) * mm, "end": v(6.06, -9.04) * mm});
            skLineSegment(sketch, "E908", {"start": v(6.06, -9.04) * mm, "end": v(6.18, -9.1) * mm});
            skLineSegment(sketch, "E909", {"start": v(6.18, -9.1) * mm, "end": v(6.74, -8.7) * mm});
            skLineSegment(sketch, "E910", {"start": v(6.74, -8.7) * mm, "end": v(6.73, -8.56) * mm});
            skLineSegment(sketch, "E911", {"start": v(6.73, -8.56) * mm, "end": v(6.71, -8.46) * mm});
            skLineSegment(sketch, "E912", {"start": v(6.71, -8.46) * mm, "end": v(6.7, -8.37) * mm});
            skLineSegment(sketch, "E913", {"start": v(6.7, -8.37) * mm, "end": v(6.68, -8.29) * mm});
            skLineSegment(sketch, "E914", {"start": v(6.68, -8.29) * mm, "end": v(6.67, -8.2) * mm});
            skLineSegment(sketch, "E915", {"start": v(6.67, -8.2) * mm, "end": v(6.65, -8.12) * mm});
            skLineSegment(sketch, "E916", {"start": v(6.65, -8.12) * mm, "end": v(6.63, -8.04) * mm});
            skLineSegment(sketch, "E917", {"start": v(6.63, -8.04) * mm, "end": v(6.61, -7.97) * mm});
            skLineSegment(sketch, "E918", {"start": v(6.61, -7.97) * mm, "end": v(6.6, -7.9) * mm});
            skLineSegment(sketch, "E919", {"start": v(6.6, -7.9) * mm, "end": v(6.57, -7.83) * mm});
            skLineSegment(sketch, "E920", {"start": v(6.57, -7.83) * mm, "end": v(6.55, -7.76) * mm});
            skLineSegment(sketch, "E921", {"start": v(6.55, -7.76) * mm, "end": v(6.53, -7.7) * mm});
            skLineSegment(sketch, "E922", {"start": v(6.53, -7.7) * mm, "end": v(6.5, -7.64) * mm});
            skLineSegment(sketch, "E923", {"start": v(6.5, -7.64) * mm, "end": v(6.49, -7.58) * mm});
            skLineSegment(sketch, "E924", {"start": v(6.49, -7.58) * mm, "end": v(6.47, -7.53) * mm});
            skLineSegment(sketch, "E925", {"start": v(6.47, -7.53) * mm, "end": v(6.45, -7.48) * mm});
            skLineSegment(sketch, "E926", {"start": v(6.45, -7.48) * mm, "end": v(6.42, -7.41) * mm});
            skLineSegment(sketch, "E927", {"start": v(6.42, -7.41) * mm, "end": v(6.39, -7.35) * mm});
            skLineSegment(sketch, "E928", {"start": v(6.39, -7.35) * mm, "end": v(6.36, -7.3) * mm});
            skLineSegment(sketch, "E929", {"start": v(6.36, -7.3) * mm, "end": v(6.33, -7.24) * mm});
            skLineSegment(sketch, "E930", {"start": v(6.33, -7.24) * mm, "end": v(6.3, -7.18) * mm});
            skLineSegment(sketch, "E931", {"start": v(6.3, -7.18) * mm, "end": v(6.27, -7.14) * mm});
            skLineSegment(sketch, "E932", {"start": v(6.27, -7.14) * mm, "end": v(6.24, -7.1) * mm});
            skLineSegment(sketch, "E933", {"start": v(6.24, -7.1) * mm, "end": v(6.2, -7.05) * mm});
            skLineSegment(sketch, "E934", {"start": v(6.2, -7.05) * mm, "end": v(5.78, -6.57) * mm});
            skArc(sketch, "E935", {"start": v(5.78, -6.57) * mm, "mid": v(5.97, -5.97) * mm, "end": v(6.57, -5.78) * mm});
            skLineSegment(sketch, "E936", {"start": v(6.57, -5.78) * mm, "end": v(7.05, -6.2) * mm});
            skLineSegment(sketch, "E937", {"start": v(7.05, -6.2) * mm, "end": v(7.1, -6.24) * mm});
            skLineSegment(sketch, "E938", {"start": v(7.1, -6.24) * mm, "end": v(7.14, -6.27) * mm});
            skLineSegment(sketch, "E939", {"start": v(7.14, -6.27) * mm, "end": v(7.18, -6.3) * mm});
            skLineSegment(sketch, "E940", {"start": v(7.18, -6.3) * mm, "end": v(7.24, -6.33) * mm});
            skLineSegment(sketch, "E941", {"start": v(7.24, -6.33) * mm, "end": v(7.3, -6.36) * mm});
            skLineSegment(sketch, "E942", {"start": v(7.3, -6.36) * mm, "end": v(7.35, -6.39) * mm});
            skLineSegment(sketch, "E943", {"start": v(7.35, -6.39) * mm, "end": v(7.41, -6.42) * mm});
            skLineSegment(sketch, "E944", {"start": v(7.41, -6.42) * mm, "end": v(7.48, -6.45) * mm});
            skLineSegment(sketch, "E945", {"start": v(7.48, -6.45) * mm, "end": v(7.53, -6.47) * mm});
            skLineSegment(sketch, "E946", {"start": v(7.53, -6.47) * mm, "end": v(7.58, -6.49) * mm});
            skLineSegment(sketch, "E947", {"start": v(7.58, -6.49) * mm, "end": v(7.64, -6.5) * mm});
            skLineSegment(sketch, "E948", {"start": v(7.64, -6.5) * mm, "end": v(7.7, -6.53) * mm});
            skLineSegment(sketch, "E949", {"start": v(7.7, -6.53) * mm, "end": v(7.76, -6.55) * mm});
            skLineSegment(sketch, "E950", {"start": v(7.76, -6.55) * mm, "end": v(7.83, -6.57) * mm});
            skLineSegment(sketch, "E951", {"start": v(7.83, -6.57) * mm, "end": v(7.9, -6.6) * mm});
            skLineSegment(sketch, "E952", {"start": v(7.9, -6.6) * mm, "end": v(7.97, -6.61) * mm});
            skLineSegment(sketch, "E953", {"start": v(7.97, -6.61) * mm, "end": v(8.04, -6.63) * mm});
            skLineSegment(sketch, "E954", {"start": v(8.04, -6.63) * mm, "end": v(8.12, -6.65) * mm});
            skLineSegment(sketch, "E955", {"start": v(8.12, -6.65) * mm, "end": v(8.2, -6.67) * mm});
            skLineSegment(sketch, "E956", {"start": v(8.2, -6.67) * mm, "end": v(8.29, -6.68) * mm});
            skLineSegment(sketch, "E957", {"start": v(8.29, -6.68) * mm, "end": v(8.37, -6.7) * mm});
            skLineSegment(sketch, "E958", {"start": v(8.37, -6.7) * mm, "end": v(8.46, -6.71) * mm});
            skLineSegment(sketch, "E959", {"start": v(8.46, -6.71) * mm, "end": v(8.56, -6.73) * mm});
            skLineSegment(sketch, "E960", {"start": v(8.56, -6.73) * mm, "end": v(8.7, -6.74) * mm});
            skLineSegment(sketch, "E961", {"start": v(8.7, -6.74) * mm, "end": v(9.1, -6.18) * mm});
            skLineSegment(sketch, "E962", {"start": v(9.1, -6.18) * mm, "end": v(9.04, -6.06) * mm});
            skLineSegment(sketch, "E963", {"start": v(9.04, -6.06) * mm, "end": v(9, -5.98) * mm});
            skLineSegment(sketch, "E964", {"start": v(9, -5.98) * mm, "end": v(8.96, -5.9) * mm});
            skLineSegment(sketch, "E965", {"start": v(8.96, -5.9) * mm, "end": v(8.92, -5.82) * mm});
            skLineSegment(sketch, "E966", {"start": v(8.92, -5.82) * mm, "end": v(8.87, -5.74) * mm});
            skLineSegment(sketch, "E967", {"start": v(8.87, -5.74) * mm, "end": v(8.83, -5.67) * mm});
            skLineSegment(sketch, "E968", {"start": v(8.83, -5.67) * mm, "end": v(8.8, -5.6) * mm});
            skLineSegment(sketch, "E969", {"start": v(8.8, -5.6) * mm, "end": v(8.75, -5.54) * mm});
            skLineSegment(sketch, "E970", {"start": v(8.75, -5.54) * mm, "end": v(8.7, -5.47) * mm});
            skLineSegment(sketch, "E971", {"start": v(8.7, -5.47) * mm, "end": v(8.67, -5.41) * mm});
            skLineSegment(sketch, "E972", {"start": v(8.67, -5.41) * mm, "end": v(8.63, -5.36) * mm});
            skLineSegment(sketch, "E973", {"start": v(8.63, -5.36) * mm, "end": v(8.59, -5.3) * mm});
            skLineSegment(sketch, "E974", {"start": v(8.59, -5.3) * mm, "end": v(8.55, -5.26) * mm});
            skLineSegment(sketch, "E975", {"start": v(8.55, -5.26) * mm, "end": v(8.51, -5.2) * mm});
            skLineSegment(sketch, "E976", {"start": v(8.51, -5.2) * mm, "end": v(8.48, -5.16) * mm});
            skLineSegment(sketch, "E977", {"start": v(8.48, -5.16) * mm, "end": v(8.44, -5.12) * mm});
            skLineSegment(sketch, "E978", {"start": v(8.44, -5.12) * mm, "end": v(8.4, -5.07) * mm});
            skLineSegment(sketch, "E979", {"start": v(8.4, -5.07) * mm, "end": v(8.34, -5.01) * mm});
            skLineSegment(sketch, "E980", {"start": v(8.34, -5.01) * mm, "end": v(8.3, -4.97) * mm});
            skLineSegment(sketch, "E981", {"start": v(8.3, -4.97) * mm, "end": v(8.26, -4.93) * mm});
            skLineSegment(sketch, "E982", {"start": v(8.26, -4.93) * mm, "end": v(8.2, -4.89) * mm});
            skLineSegment(sketch, "E983", {"start": v(8.2, -4.89) * mm, "end": v(8.17, -4.85) * mm});
            skLineSegment(sketch, "E984", {"start": v(8.17, -4.85) * mm, "end": v(8.13, -4.82) * mm});
            skLineSegment(sketch, "E985", {"start": v(8.13, -4.82) * mm, "end": v(8.08, -4.79) * mm});
            skLineSegment(sketch, "E986", {"start": v(8.08, -4.79) * mm, "end": v(7.53, -4.46) * mm});
            skArc(sketch, "E987", {"start": v(7.53, -4.46) * mm, "mid": v(7.52, -3.83) * mm, "end": v(8.03, -3.47) * mm});
            skLineSegment(sketch, "E988", {"start": v(8.03, -3.47) * mm, "end": v(8.63, -3.73) * mm});
            skLineSegment(sketch, "E989", {"start": v(8.63, -3.73) * mm, "end": v(8.68, -3.74) * mm});
            skLineSegment(sketch, "E990", {"start": v(8.68, -3.74) * mm, "end": v(8.73, -3.76) * mm});
            skLineSegment(sketch, "E991", {"start": v(8.73, -3.76) * mm, "end": v(8.78, -3.77) * mm});
            skLineSegment(sketch, "E992", {"start": v(8.78, -3.77) * mm, "end": v(8.84, -3.78) * mm});
            skLineSegment(sketch, "E993", {"start": v(8.84, -3.78) * mm, "end": v(8.9, -3.8) * mm});
            skLineSegment(sketch, "E994", {"start": v(8.9, -3.8) * mm, "end": v(8.96, -3.8) * mm});
            skLineSegment(sketch, "E995", {"start": v(8.96, -3.8) * mm, "end": v(9.03, -3.81) * mm});
            skLineSegment(sketch, "E996", {"start": v(9.03, -3.81) * mm, "end": v(9.1, -3.82) * mm});
            skLineSegment(sketch, "E997", {"start": v(9.1, -3.82) * mm, "end": v(9.16, -3.82) * mm});
            skLineSegment(sketch, "E998", {"start": v(9.16, -3.82) * mm, "end": v(9.22, -3.83) * mm});
            skLineSegment(sketch, "E999", {"start": v(9.22, -3.83) * mm, "end": v(9.28, -3.83) * mm});
            skLineSegment(sketch, "E1000", {"start": v(9.28, -3.83) * mm, "end": v(9.34, -3.83) * mm});
            skLineSegment(sketch, "E1001", {"start": v(9.34, -3.83) * mm, "end": v(9.4, -3.83) * mm});
            skLineSegment(sketch, "E1002", {"start": v(9.4, -3.83) * mm, "end": v(9.48, -3.83) * mm});
            skLineSegment(sketch, "E1003", {"start": v(9.48, -3.83) * mm, "end": v(9.55, -3.83) * mm});
            skLineSegment(sketch, "E1004", {"start": v(9.55, -3.83) * mm, "end": v(9.62, -3.82) * mm});
            skLineSegment(sketch, "E1005", {"start": v(9.62, -3.82) * mm, "end": v(9.7, -3.82) * mm});
            skLineSegment(sketch, "E1006", {"start": v(9.7, -3.82) * mm, "end": v(9.78, -3.81) * mm});
            skLineSegment(sketch, "E1007", {"start": v(9.78, -3.81) * mm, "end": v(9.86, -3.8) * mm});
            skLineSegment(sketch, "E1008", {"start": v(9.86, -3.8) * mm, "end": v(9.95, -3.8) * mm});
            skLineSegment(sketch, "E1009", {"start": v(9.95, -3.8) * mm, "end": v(10.03, -3.78) * mm});
            skLineSegment(sketch, "E1010", {"start": v(10.03, -3.78) * mm, "end": v(10.12, -3.77) * mm});
            skLineSegment(sketch, "E1011", {"start": v(10.12, -3.77) * mm, "end": v(10.22, -3.75) * mm});
            skLineSegment(sketch, "E1012", {"start": v(10.22, -3.75) * mm, "end": v(10.35, -3.73) * mm});
            skLineSegment(sketch, "E1013", {"start": v(10.35, -3.73) * mm, "end": v(10.56, -3.07) * mm});
            skLineSegment(sketch, "E1014", {"start": v(10.56, -3.07) * mm, "end": v(10.47, -2.97) * mm});
            skLineSegment(sketch, "E1015", {"start": v(10.47, -2.97) * mm, "end": v(10.4, -2.9) * mm});
            skLineSegment(sketch, "E1016", {"start": v(10.4, -2.9) * mm, "end": v(10.34, -2.84) * mm});
            skLineSegment(sketch, "E1017", {"start": v(10.34, -2.84) * mm, "end": v(10.28, -2.78) * mm});
            skLineSegment(sketch, "E1018", {"start": v(10.28, -2.78) * mm, "end": v(10.21, -2.72) * mm});
            skLineSegment(sketch, "E1019", {"start": v(10.21, -2.72) * mm, "end": v(10.15, -2.66) * mm});
            skLineSegment(sketch, "E1020", {"start": v(10.15, -2.66) * mm, "end": v(10.1, -2.61) * mm});
            skLineSegment(sketch, "E1021", {"start": v(10.1, -2.61) * mm, "end": v(10.03, -2.56) * mm});
            skLineSegment(sketch, "E1022", {"start": v(10.03, -2.56) * mm, "end": v(9.97, -2.52) * mm});
            skLineSegment(sketch, "E1023", {"start": v(9.97, -2.52) * mm, "end": v(9.92, -2.47) * mm});
            skLineSegment(sketch, "E1024", {"start": v(9.92, -2.47) * mm, "end": v(9.86, -2.43) * mm});
            skLineSegment(sketch, "E1025", {"start": v(9.86, -2.43) * mm, "end": v(9.8, -2.4) * mm});
            skLineSegment(sketch, "E1026", {"start": v(9.8, -2.4) * mm, "end": v(9.76, -2.36) * mm});
            skLineSegment(sketch, "E1027", {"start": v(9.76, -2.36) * mm, "end": v(9.7, -2.32) * mm});
            skLineSegment(sketch, "E1028", {"start": v(9.7, -2.32) * mm, "end": v(9.66, -2.3) * mm});
            skLineSegment(sketch, "E1029", {"start": v(9.66, -2.3) * mm, "end": v(9.61, -2.26) * mm});
            skLineSegment(sketch, "E1030", {"start": v(9.61, -2.26) * mm, "end": v(9.55, -2.22) * mm});
            skLineSegment(sketch, "E1031", {"start": v(9.55, -2.22) * mm, "end": v(9.48, -2.2) * mm});
            skLineSegment(sketch, "E1032", {"start": v(9.48, -2.2) * mm, "end": v(9.43, -2.16) * mm});
            skLineSegment(sketch, "E1033", {"start": v(9.43, -2.16) * mm, "end": v(9.38, -2.14) * mm});
            skLineSegment(sketch, "E1034", {"start": v(9.38, -2.14) * mm, "end": v(9.32, -2.11) * mm});
            skLineSegment(sketch, "E1035", {"start": v(9.32, -2.11) * mm, "end": v(9.27, -2.09) * mm});
            skLineSegment(sketch, "E1036", {"start": v(9.27, -2.09) * mm, "end": v(9.22, -2.07) * mm});
            skLineSegment(sketch, "E1037", {"start": v(9.22, -2.07) * mm, "end": v(9.17, -2.06) * mm});
            skLineSegment(sketch, "E1038", {"start": v(9.17, -2.06) * mm, "end": v(8.54, -1.92) * mm});
            skArc(sketch, "E1039", {"start": v(8.54, -1.92) * mm, "mid": v(8.34, -1.32) * mm, "end": v(8.71, -0.82) * mm});
            skCircle(sketch, "E1040", {"center": v(0, 0) * mm, "radius": 0.5 * mm});
            skSolve(sketch);
        }
        {
            var Q0;
            Q0 = qSketchRegion(id + "F0", true);
            var Q1;
            Q1=makeQuery(id+"F0.imprint","IMPRINT",FACE,{"disambiguationData":[TD([[makeQuery(id+"F0.imprint","IMPRINT",EDGE,{"derivedFrom":sQuery(id+"F0.wireOp",EDGE,"E0")}),1.0]])]});
            extrude(context, id + "F1", {"entities" : qUnion([Q0, Q1]), "depth" : 25 * mm});
        }
        {
            var Q0;
            Q0=makeQuery(id+"F1.opExtrude","CAP_FACE",FACE,{"disambiguationData":[OSD([sQuery(id+"F0.wireOp",EDGE,"E0"),sQuery(id+"F0.wireOp",EDGE,"E1"),sQuery(id+"F0.wireOp",EDGE,"E2"),sQuery(id+"F0.wireOp",EDGE,"E3"),sQuery(id+"F0.wireOp",EDGE,"E4"),sQuery(id+"F0.wireOp",EDGE,"E5"),sQuery(id+"F0.wireOp",EDGE,"E6"),sQuery(id+"F0.wireOp",EDGE,"E7"),sQuery(id+"F0.wireOp",EDGE,"E8"),sQuery(id+"F0.wireOp",EDGE,"E9"),sQuery(id+"F0.wireOp",EDGE,"E10"),sQuery(id+"F0.wireOp",EDGE,"E11"),sQuery(id+"F0.wireOp",EDGE,"E12"),sQuery(id+"F0.wireOp",EDGE,"E13"),sQuery(id+"F0.wireOp",EDGE,"E14"),sQuery(id+"F0.wireOp",EDGE,"E15"),sQuery(id+"F0.wireOp",EDGE,"E16"),sQuery(id+"F0.wireOp",EDGE,"E17"),sQuery(id+"F0.wireOp",EDGE,"E18"),sQuery(id+"F0.wireOp",EDGE,"E19"),sQuery(id+"F0.wireOp",EDGE,"E20"),sQuery(id+"F0.wireOp",EDGE,"E21"),sQuery(id+"F0.wireOp",EDGE,"E22"),sQuery(id+"F0.wireOp",EDGE,"E23"),sQuery(id+"F0.wireOp",EDGE,"E24"),sQuery(id+"F0.wireOp",EDGE,"E25"),sQuery(id+"F0.wireOp",EDGE,"E26"),sQuery(id+"F0.wireOp",EDGE,"E27"),sQuery(id+"F0.wireOp",EDGE,"E28"),sQuery(id+"F0.wireOp",EDGE,"E29"),sQuery(id+"F0.wireOp",EDGE,"E30"),sQuery(id+"F0.wireOp",EDGE,"E31"),sQuery(id+"F0.wireOp",EDGE,"E32"),sQuery(id+"F0.wireOp",EDGE,"E33"),sQuery(id+"F0.wireOp",EDGE,"E34"),sQuery(id+"F0.wireOp",EDGE,"E35"),sQuery(id+"F0.wireOp",EDGE,"E36"),sQuery(id+"F0.wireOp",EDGE,"E37"),sQuery(id+"F0.wireOp",EDGE,"E38"),sQuery(id+"F0.wireOp",EDGE,"E39"),sQuery(id+"F0.wireOp",EDGE,"E40"),sQuery(id+"F0.wireOp",EDGE,"E41"),sQuery(id+"F0.wireOp",EDGE,"E42"),sQuery(id+"F0.wireOp",EDGE,"E43"),sQuery(id+"F0.wireOp",EDGE,"E44"),sQuery(id+"F0.wireOp",EDGE,"E45"),sQuery(id+"F0.wireOp",EDGE,"E46"),sQuery(id+"F0.wireOp",EDGE,"E47"),sQuery(id+"F0.wireOp",EDGE,"E48"),sQuery(id+"F0.wireOp",EDGE,"E49"),sQuery(id+"F0.wireOp",EDGE,"E50"),sQuery(id+"F0.wireOp",EDGE,"E51"),sQuery(id+"F0.wireOp",EDGE,"E52"),sQuery(id+"F0.wireOp",EDGE,"E53"),sQuery(id+"F0.wireOp",EDGE,"E54"),sQuery(id+"F0.wireOp",EDGE,"E55"),sQuery(id+"F0.wireOp",EDGE,"E56"),sQuery(id+"F0.wireOp",EDGE,"E57"),sQuery(id+"F0.wireOp",EDGE,"E58"),sQuery(id+"F0.wireOp",EDGE,"E59"),sQuery(id+"F0.wireOp",EDGE,"E60"),sQuery(id+"F0.wireOp",EDGE,"E61"),sQuery(id+"F0.wireOp",EDGE,"E62"),sQuery(id+"F0.wireOp",EDGE,"E63"),sQuery(id+"F0.wireOp",EDGE,"E64"),sQuery(id+"F0.wireOp",EDGE,"E65"),sQuery(id+"F0.wireOp",EDGE,"E66"),sQuery(id+"F0.wireOp",EDGE,"E67"),sQuery(id+"F0.wireOp",EDGE,"E68"),sQuery(id+"F0.wireOp",EDGE,"E69"),sQuery(id+"F0.wireOp",EDGE,"E70"),sQuery(id+"F0.wireOp",EDGE,"E71"),sQuery(id+"F0.wireOp",EDGE,"E72"),sQuery(id+"F0.wireOp",EDGE,"E73"),sQuery(id+"F0.wireOp",EDGE,"E74"),sQuery(id+"F0.wireOp",EDGE,"E75"),sQuery(id+"F0.wireOp",EDGE,"E76"),sQuery(id+"F0.wireOp",EDGE,"E77"),sQuery(id+"F0.wireOp",EDGE,"E78"),sQuery(id+"F0.wireOp",EDGE,"E79"),sQuery(id+"F0.wireOp",EDGE,"E80"),sQuery(id+"F0.wireOp",EDGE,"E81"),sQuery(id+"F0.wireOp",EDGE,"E82"),sQuery(id+"F0.wireOp",EDGE,"E83"),sQuery(id+"F0.wireOp",EDGE,"E84"),sQuery(id+"F0.wireOp",EDGE,"E85"),sQuery(id+"F0.wireOp",EDGE,"E86"),sQuery(id+"F0.wireOp",EDGE,"E87"),sQuery(id+"F0.wireOp",EDGE,"E88"),sQuery(id+"F0.wireOp",EDGE,"E89"),sQuery(id+"F0.wireOp",EDGE,"E90"),sQuery(id+"F0.wireOp",EDGE,"E91"),sQuery(id+"F0.wireOp",EDGE,"E92"),sQuery(id+"F0.wireOp",EDGE,"E93"),sQuery(id+"F0.wireOp",EDGE,"E94"),sQuery(id+"F0.wireOp",EDGE,"E95"),sQuery(id+"F0.wireOp",EDGE,"E96"),sQuery(id+"F0.wireOp",EDGE,"E97"),sQuery(id+"F0.wireOp",EDGE,"E98"),sQuery(id+"F0.wireOp",EDGE,"E99"),sQuery(id+"F0.wireOp",EDGE,"E100"),sQuery(id+"F0.wireOp",EDGE,"E101"),sQuery(id+"F0.wireOp",EDGE,"E102"),sQuery(id+"F0.wireOp",EDGE,"E103"),sQuery(id+"F0.wireOp",EDGE,"E104"),sQuery(id+"F0.wireOp",EDGE,"E105"),sQuery(id+"F0.wireOp",EDGE,"E106"),sQuery(id+"F0.wireOp",EDGE,"E107"),sQuery(id+"F0.wireOp",EDGE,"E108"),sQuery(id+"F0.wireOp",EDGE,"E109"),sQuery(id+"F0.wireOp",EDGE,"E110"),sQuery(id+"F0.wireOp",EDGE,"E111"),sQuery(id+"F0.wireOp",EDGE,"E112"),sQuery(id+"F0.wireOp",EDGE,"E113"),sQuery(id+"F0.wireOp",EDGE,"E114"),sQuery(id+"F0.wireOp",EDGE,"E115"),sQuery(id+"F0.wireOp",EDGE,"E116"),sQuery(id+"F0.wireOp",EDGE,"E117"),sQuery(id+"F0.wireOp",EDGE,"E118"),sQuery(id+"F0.wireOp",EDGE,"E119"),sQuery(id+"F0.wireOp",EDGE,"E120"),sQuery(id+"F0.wireOp",EDGE,"E121"),sQuery(id+"F0.wireOp",EDGE,"E122"),sQuery(id+"F0.wireOp",EDGE,"E123"),sQuery(id+"F0.wireOp",EDGE,"E124"),sQuery(id+"F0.wireOp",EDGE,"E125"),sQuery(id+"F0.wireOp",EDGE,"E126"),sQuery(id+"F0.wireOp",EDGE,"E127"),sQuery(id+"F0.wireOp",EDGE,"E128"),sQuery(id+"F0.wireOp",EDGE,"E129"),sQuery(id+"F0.wireOp",EDGE,"E130"),sQuery(id+"F0.wireOp",EDGE,"E131"),sQuery(id+"F0.wireOp",EDGE,"E132"),sQuery(id+"F0.wireOp",EDGE,"E133"),sQuery(id+"F0.wireOp",EDGE,"E134"),sQuery(id+"F0.wireOp",EDGE,"E135"),sQuery(id+"F0.wireOp",EDGE,"E136"),sQuery(id+"F0.wireOp",EDGE,"E137"),sQuery(id+"F0.wireOp",EDGE,"E138"),sQuery(id+"F0.wireOp",EDGE,"E139"),sQuery(id+"F0.wireOp",EDGE,"E140"),sQuery(id+"F0.wireOp",EDGE,"E141"),sQuery(id+"F0.wireOp",EDGE,"E142"),sQuery(id+"F0.wireOp",EDGE,"E143"),sQuery(id+"F0.wireOp",EDGE,"E144"),sQuery(id+"F0.wireOp",EDGE,"E145"),sQuery(id+"F0.wireOp",EDGE,"E146"),sQuery(id+"F0.wireOp",EDGE,"E147"),sQuery(id+"F0.wireOp",EDGE,"E148"),sQuery(id+"F0.wireOp",EDGE,"E149"),sQuery(id+"F0.wireOp",EDGE,"E150"),sQuery(id+"F0.wireOp",EDGE,"E151"),sQuery(id+"F0.wireOp",EDGE,"E152"),sQuery(id+"F0.wireOp",EDGE,"E153"),sQuery(id+"F0.wireOp",EDGE,"E154"),sQuery(id+"F0.wireOp",EDGE,"E155"),sQuery(id+"F0.wireOp",EDGE,"E156"),sQuery(id+"F0.wireOp",EDGE,"E157"),sQuery(id+"F0.wireOp",EDGE,"E158"),sQuery(id+"F0.wireOp",EDGE,"E159"),sQuery(id+"F0.wireOp",EDGE,"E160"),sQuery(id+"F0.wireOp",EDGE,"E161"),sQuery(id+"F0.wireOp",EDGE,"E162"),sQuery(id+"F0.wireOp",EDGE,"E163"),sQuery(id+"F0.wireOp",EDGE,"E164"),sQuery(id+"F0.wireOp",EDGE,"E165"),sQuery(id+"F0.wireOp",EDGE,"E166"),sQuery(id+"F0.wireOp",EDGE,"E167"),sQuery(id+"F0.wireOp",EDGE,"E168"),sQuery(id+"F0.wireOp",EDGE,"E169"),sQuery(id+"F0.wireOp",EDGE,"E170"),sQuery(id+"F0.wireOp",EDGE,"E171"),sQuery(id+"F0.wireOp",EDGE,"E172"),sQuery(id+"F0.wireOp",EDGE,"E173"),sQuery(id+"F0.wireOp",EDGE,"E174"),sQuery(id+"F0.wireOp",EDGE,"E175"),sQuery(id+"F0.wireOp",EDGE,"E176"),sQuery(id+"F0.wireOp",EDGE,"E177"),sQuery(id+"F0.wireOp",EDGE,"E178"),sQuery(id+"F0.wireOp",EDGE,"E179"),sQuery(id+"F0.wireOp",EDGE,"E180"),sQuery(id+"F0.wireOp",EDGE,"E181"),sQuery(id+"F0.wireOp",EDGE,"E182"),sQuery(id+"F0.wireOp",EDGE,"E183"),sQuery(id+"F0.wireOp",EDGE,"E184"),sQuery(id+"F0.wireOp",EDGE,"E185"),sQuery(id+"F0.wireOp",EDGE,"E186"),sQuery(id+"F0.wireOp",EDGE,"E187"),sQuery(id+"F0.wireOp",EDGE,"E188"),sQuery(id+"F0.wireOp",EDGE,"E189"),sQuery(id+"F0.wireOp",EDGE,"E190"),sQuery(id+"F0.wireOp",EDGE,"E191"),sQuery(id+"F0.wireOp",EDGE,"E192"),sQuery(id+"F0.wireOp",EDGE,"E193"),sQuery(id+"F0.wireOp",EDGE,"E194"),sQuery(id+"F0.wireOp",EDGE,"E195"),sQuery(id+"F0.wireOp",EDGE,"E196"),sQuery(id+"F0.wireOp",EDGE,"E197"),sQuery(id+"F0.wireOp",EDGE,"E198"),sQuery(id+"F0.wireOp",EDGE,"E199"),sQuery(id+"F0.wireOp",EDGE,"E200"),sQuery(id+"F0.wireOp",EDGE,"E201"),sQuery(id+"F0.wireOp",EDGE,"E202"),sQuery(id+"F0.wireOp",EDGE,"E203"),sQuery(id+"F0.wireOp",EDGE,"E204"),sQuery(id+"F0.wireOp",EDGE,"E205"),sQuery(id+"F0.wireOp",EDGE,"E206"),sQuery(id+"F0.wireOp",EDGE,"E207"),sQuery(id+"F0.wireOp",EDGE,"E208"),sQuery(id+"F0.wireOp",EDGE,"E209"),sQuery(id+"F0.wireOp",EDGE,"E210"),sQuery(id+"F0.wireOp",EDGE,"E211"),sQuery(id+"F0.wireOp",EDGE,"E212"),sQuery(id+"F0.wireOp",EDGE,"E213"),sQuery(id+"F0.wireOp",EDGE,"E214"),sQuery(id+"F0.wireOp",EDGE,"E215"),sQuery(id+"F0.wireOp",EDGE,"E216"),sQuery(id+"F0.wireOp",EDGE,"E217"),sQuery(id+"F0.wireOp",EDGE,"E218"),sQuery(id+"F0.wireOp",EDGE,"E219"),sQuery(id+"F0.wireOp",EDGE,"E220"),sQuery(id+"F0.wireOp",EDGE,"E221"),sQuery(id+"F0.wireOp",EDGE,"E222"),sQuery(id+"F0.wireOp",EDGE,"E223"),sQuery(id+"F0.wireOp",EDGE,"E224"),sQuery(id+"F0.wireOp",EDGE,"E225"),sQuery(id+"F0.wireOp",EDGE,"E226"),sQuery(id+"F0.wireOp",EDGE,"E227"),sQuery(id+"F0.wireOp",EDGE,"E228"),sQuery(id+"F0.wireOp",EDGE,"E229"),sQuery(id+"F0.wireOp",EDGE,"E230"),sQuery(id+"F0.wireOp",EDGE,"E231"),sQuery(id+"F0.wireOp",EDGE,"E232"),sQuery(id+"F0.wireOp",EDGE,"E233"),sQuery(id+"F0.wireOp",EDGE,"E234"),sQuery(id+"F0.wireOp",EDGE,"E235"),sQuery(id+"F0.wireOp",EDGE,"E236"),sQuery(id+"F0.wireOp",EDGE,"E237"),sQuery(id+"F0.wireOp",EDGE,"E238"),sQuery(id+"F0.wireOp",EDGE,"E239"),sQuery(id+"F0.wireOp",EDGE,"E240"),sQuery(id+"F0.wireOp",EDGE,"E241"),sQuery(id+"F0.wireOp",EDGE,"E242"),sQuery(id+"F0.wireOp",EDGE,"E243"),sQuery(id+"F0.wireOp",EDGE,"E244"),sQuery(id+"F0.wireOp",EDGE,"E245"),sQuery(id+"F0.wireOp",EDGE,"E246"),sQuery(id+"F0.wireOp",EDGE,"E247"),sQuery(id+"F0.wireOp",EDGE,"E248"),sQuery(id+"F0.wireOp",EDGE,"E249"),sQuery(id+"F0.wireOp",EDGE,"E250"),sQuery(id+"F0.wireOp",EDGE,"E251"),sQuery(id+"F0.wireOp",EDGE,"E252"),sQuery(id+"F0.wireOp",EDGE,"E253"),sQuery(id+"F0.wireOp",EDGE,"E254"),sQuery(id+"F0.wireOp",EDGE,"E255"),sQuery(id+"F0.wireOp",EDGE,"E256"),sQuery(id+"F0.wireOp",EDGE,"E257"),sQuery(id+"F0.wireOp",EDGE,"E258"),sQuery(id+"F0.wireOp",EDGE,"E259"),sQuery(id+"F0.wireOp",EDGE,"E260"),sQuery(id+"F0.wireOp",EDGE,"E261"),sQuery(id+"F0.wireOp",EDGE,"E262"),sQuery(id+"F0.wireOp",EDGE,"E263"),sQuery(id+"F0.wireOp",EDGE,"E264"),sQuery(id+"F0.wireOp",EDGE,"E265"),sQuery(id+"F0.wireOp",EDGE,"E266"),sQuery(id+"F0.wireOp",EDGE,"E267"),sQuery(id+"F0.wireOp",EDGE,"E268"),sQuery(id+"F0.wireOp",EDGE,"E269"),sQuery(id+"F0.wireOp",EDGE,"E270"),sQuery(id+"F0.wireOp",EDGE,"E271"),sQuery(id+"F0.wireOp",EDGE,"E272"),sQuery(id+"F0.wireOp",EDGE,"E273"),sQuery(id+"F0.wireOp",EDGE,"E274"),sQuery(id+"F0.wireOp",EDGE,"E275"),sQuery(id+"F0.wireOp",EDGE,"E276"),sQuery(id+"F0.wireOp",EDGE,"E277"),sQuery(id+"F0.wireOp",EDGE,"E278"),sQuery(id+"F0.wireOp",EDGE,"E279"),sQuery(id+"F0.wireOp",EDGE,"E280"),sQuery(id+"F0.wireOp",EDGE,"E281"),sQuery(id+"F0.wireOp",EDGE,"E282"),sQuery(id+"F0.wireOp",EDGE,"E283"),sQuery(id+"F0.wireOp",EDGE,"E284"),sQuery(id+"F0.wireOp",EDGE,"E285"),sQuery(id+"F0.wireOp",EDGE,"E286"),sQuery(id+"F0.wireOp",EDGE,"E287"),sQuery(id+"F0.wireOp",EDGE,"E288"),sQuery(id+"F0.wireOp",EDGE,"E289"),sQuery(id+"F0.wireOp",EDGE,"E290"),sQuery(id+"F0.wireOp",EDGE,"E291"),sQuery(id+"F0.wireOp",EDGE,"E292"),sQuery(id+"F0.wireOp",EDGE,"E293"),sQuery(id+"F0.wireOp",EDGE,"E294"),sQuery(id+"F0.wireOp",EDGE,"E295"),sQuery(id+"F0.wireOp",EDGE,"E296"),sQuery(id+"F0.wireOp",EDGE,"E297"),sQuery(id+"F0.wireOp",EDGE,"E298"),sQuery(id+"F0.wireOp",EDGE,"E299"),sQuery(id+"F0.wireOp",EDGE,"E300"),sQuery(id+"F0.wireOp",EDGE,"E301"),sQuery(id+"F0.wireOp",EDGE,"E302"),sQuery(id+"F0.wireOp",EDGE,"E303"),sQuery(id+"F0.wireOp",EDGE,"E304"),sQuery(id+"F0.wireOp",EDGE,"E305"),sQuery(id+"F0.wireOp",EDGE,"E306"),sQuery(id+"F0.wireOp",EDGE,"E307"),sQuery(id+"F0.wireOp",EDGE,"E308"),sQuery(id+"F0.wireOp",EDGE,"E309"),sQuery(id+"F0.wireOp",EDGE,"E310"),sQuery(id+"F0.wireOp",EDGE,"E311"),sQuery(id+"F0.wireOp",EDGE,"E312"),sQuery(id+"F0.wireOp",EDGE,"E313"),sQuery(id+"F0.wireOp",EDGE,"E314"),sQuery(id+"F0.wireOp",EDGE,"E315"),sQuery(id+"F0.wireOp",EDGE,"E316"),sQuery(id+"F0.wireOp",EDGE,"E317"),sQuery(id+"F0.wireOp",EDGE,"E318"),sQuery(id+"F0.wireOp",EDGE,"E319"),sQuery(id+"F0.wireOp",EDGE,"E320"),sQuery(id+"F0.wireOp",EDGE,"E321"),sQuery(id+"F0.wireOp",EDGE,"E322"),sQuery(id+"F0.wireOp",EDGE,"E323"),sQuery(id+"F0.wireOp",EDGE,"E324"),sQuery(id+"F0.wireOp",EDGE,"E325"),sQuery(id+"F0.wireOp",EDGE,"E326"),sQuery(id+"F0.wireOp",EDGE,"E327"),sQuery(id+"F0.wireOp",EDGE,"E328"),sQuery(id+"F0.wireOp",EDGE,"E329"),sQuery(id+"F0.wireOp",EDGE,"E330"),sQuery(id+"F0.wireOp",EDGE,"E331"),sQuery(id+"F0.wireOp",EDGE,"E332"),sQuery(id+"F0.wireOp",EDGE,"E333"),sQuery(id+"F0.wireOp",EDGE,"E334"),sQuery(id+"F0.wireOp",EDGE,"E335"),sQuery(id+"F0.wireOp",EDGE,"E336"),sQuery(id+"F0.wireOp",EDGE,"E337"),sQuery(id+"F0.wireOp",EDGE,"E338"),sQuery(id+"F0.wireOp",EDGE,"E339"),sQuery(id+"F0.wireOp",EDGE,"E340"),sQuery(id+"F0.wireOp",EDGE,"E341"),sQuery(id+"F0.wireOp",EDGE,"E342"),sQuery(id+"F0.wireOp",EDGE,"E343"),sQuery(id+"F0.wireOp",EDGE,"E344"),sQuery(id+"F0.wireOp",EDGE,"E345"),sQuery(id+"F0.wireOp",EDGE,"E346"),sQuery(id+"F0.wireOp",EDGE,"E347"),sQuery(id+"F0.wireOp",EDGE,"E348"),sQuery(id+"F0.wireOp",EDGE,"E349"),sQuery(id+"F0.wireOp",EDGE,"E350"),sQuery(id+"F0.wireOp",EDGE,"E351"),sQuery(id+"F0.wireOp",EDGE,"E352"),sQuery(id+"F0.wireOp",EDGE,"E353"),sQuery(id+"F0.wireOp",EDGE,"E354"),sQuery(id+"F0.wireOp",EDGE,"E355"),sQuery(id+"F0.wireOp",EDGE,"E356"),sQuery(id+"F0.wireOp",EDGE,"E357"),sQuery(id+"F0.wireOp",EDGE,"E358"),sQuery(id+"F0.wireOp",EDGE,"E359"),sQuery(id+"F0.wireOp",EDGE,"E360"),sQuery(id+"F0.wireOp",EDGE,"E361"),sQuery(id+"F0.wireOp",EDGE,"E362"),sQuery(id+"F0.wireOp",EDGE,"E363"),sQuery(id+"F0.wireOp",EDGE,"E364"),sQuery(id+"F0.wireOp",EDGE,"E365"),sQuery(id+"F0.wireOp",EDGE,"E366"),sQuery(id+"F0.wireOp",EDGE,"E367"),sQuery(id+"F0.wireOp",EDGE,"E368"),sQuery(id+"F0.wireOp",EDGE,"E369"),sQuery(id+"F0.wireOp",EDGE,"E370"),sQuery(id+"F0.wireOp",EDGE,"E371"),sQuery(id+"F0.wireOp",EDGE,"E372"),sQuery(id+"F0.wireOp",EDGE,"E373"),sQuery(id+"F0.wireOp",EDGE,"E374"),sQuery(id+"F0.wireOp",EDGE,"E375"),sQuery(id+"F0.wireOp",EDGE,"E376"),sQuery(id+"F0.wireOp",EDGE,"E377"),sQuery(id+"F0.wireOp",EDGE,"E378"),sQuery(id+"F0.wireOp",EDGE,"E379"),sQuery(id+"F0.wireOp",EDGE,"E380"),sQuery(id+"F0.wireOp",EDGE,"E381"),sQuery(id+"F0.wireOp",EDGE,"E382"),sQuery(id+"F0.wireOp",EDGE,"E383"),sQuery(id+"F0.wireOp",EDGE,"E384"),sQuery(id+"F0.wireOp",EDGE,"E385"),sQuery(id+"F0.wireOp",EDGE,"E386"),sQuery(id+"F0.wireOp",EDGE,"E387"),sQuery(id+"F0.wireOp",EDGE,"E388"),sQuery(id+"F0.wireOp",EDGE,"E389"),sQuery(id+"F0.wireOp",EDGE,"E390"),sQuery(id+"F0.wireOp",EDGE,"E391"),sQuery(id+"F0.wireOp",EDGE,"E392"),sQuery(id+"F0.wireOp",EDGE,"E393"),sQuery(id+"F0.wireOp",EDGE,"E394"),sQuery(id+"F0.wireOp",EDGE,"E395"),sQuery(id+"F0.wireOp",EDGE,"E396"),sQuery(id+"F0.wireOp",EDGE,"E397"),sQuery(id+"F0.wireOp",EDGE,"E398"),sQuery(id+"F0.wireOp",EDGE,"E399"),sQuery(id+"F0.wireOp",EDGE,"E400"),sQuery(id+"F0.wireOp",EDGE,"E401"),sQuery(id+"F0.wireOp",EDGE,"E402"),sQuery(id+"F0.wireOp",EDGE,"E403"),sQuery(id+"F0.wireOp",EDGE,"E404"),sQuery(id+"F0.wireOp",EDGE,"E405"),sQuery(id+"F0.wireOp",EDGE,"E406"),sQuery(id+"F0.wireOp",EDGE,"E407"),sQuery(id+"F0.wireOp",EDGE,"E408"),sQuery(id+"F0.wireOp",EDGE,"E409"),sQuery(id+"F0.wireOp",EDGE,"E410"),sQuery(id+"F0.wireOp",EDGE,"E411"),sQuery(id+"F0.wireOp",EDGE,"E412"),sQuery(id+"F0.wireOp",EDGE,"E413"),sQuery(id+"F0.wireOp",EDGE,"E414"),sQuery(id+"F0.wireOp",EDGE,"E415"),sQuery(id+"F0.wireOp",EDGE,"E416"),sQuery(id+"F0.wireOp",EDGE,"E417"),sQuery(id+"F0.wireOp",EDGE,"E418"),sQuery(id+"F0.wireOp",EDGE,"E419"),sQuery(id+"F0.wireOp",EDGE,"E420"),sQuery(id+"F0.wireOp",EDGE,"E421"),sQuery(id+"F0.wireOp",EDGE,"E422"),sQuery(id+"F0.wireOp",EDGE,"E423"),sQuery(id+"F0.wireOp",EDGE,"E424"),sQuery(id+"F0.wireOp",EDGE,"E425"),sQuery(id+"F0.wireOp",EDGE,"E426"),sQuery(id+"F0.wireOp",EDGE,"E427"),sQuery(id+"F0.wireOp",EDGE,"E428"),sQuery(id+"F0.wireOp",EDGE,"E429"),sQuery(id+"F0.wireOp",EDGE,"E430"),sQuery(id+"F0.wireOp",EDGE,"E431"),sQuery(id+"F0.wireOp",EDGE,"E432"),sQuery(id+"F0.wireOp",EDGE,"E433"),sQuery(id+"F0.wireOp",EDGE,"E434"),sQuery(id+"F0.wireOp",EDGE,"E435"),sQuery(id+"F0.wireOp",EDGE,"E436"),sQuery(id+"F0.wireOp",EDGE,"E437"),sQuery(id+"F0.wireOp",EDGE,"E438"),sQuery(id+"F0.wireOp",EDGE,"E439"),sQuery(id+"F0.wireOp",EDGE,"E440"),sQuery(id+"F0.wireOp",EDGE,"E441"),sQuery(id+"F0.wireOp",EDGE,"E442"),sQuery(id+"F0.wireOp",EDGE,"E443"),sQuery(id+"F0.wireOp",EDGE,"E444"),sQuery(id+"F0.wireOp",EDGE,"E445"),sQuery(id+"F0.wireOp",EDGE,"E446"),sQuery(id+"F0.wireOp",EDGE,"E447"),sQuery(id+"F0.wireOp",EDGE,"E448"),sQuery(id+"F0.wireOp",EDGE,"E449"),sQuery(id+"F0.wireOp",EDGE,"E450"),sQuery(id+"F0.wireOp",EDGE,"E451"),sQuery(id+"F0.wireOp",EDGE,"E452"),sQuery(id+"F0.wireOp",EDGE,"E453"),sQuery(id+"F0.wireOp",EDGE,"E454"),sQuery(id+"F0.wireOp",EDGE,"E455"),sQuery(id+"F0.wireOp",EDGE,"E456"),sQuery(id+"F0.wireOp",EDGE,"E457"),sQuery(id+"F0.wireOp",EDGE,"E458"),sQuery(id+"F0.wireOp",EDGE,"E459"),sQuery(id+"F0.wireOp",EDGE,"E460"),sQuery(id+"F0.wireOp",EDGE,"E461"),sQuery(id+"F0.wireOp",EDGE,"E462"),sQuery(id+"F0.wireOp",EDGE,"E463"),sQuery(id+"F0.wireOp",EDGE,"E464"),sQuery(id+"F0.wireOp",EDGE,"E465"),sQuery(id+"F0.wireOp",EDGE,"E466"),sQuery(id+"F0.wireOp",EDGE,"E467"),sQuery(id+"F0.wireOp",EDGE,"E468"),sQuery(id+"F0.wireOp",EDGE,"E469"),sQuery(id+"F0.wireOp",EDGE,"E470"),sQuery(id+"F0.wireOp",EDGE,"E471"),sQuery(id+"F0.wireOp",EDGE,"E472"),sQuery(id+"F0.wireOp",EDGE,"E473"),sQuery(id+"F0.wireOp",EDGE,"E474"),sQuery(id+"F0.wireOp",EDGE,"E475"),sQuery(id+"F0.wireOp",EDGE,"E476"),sQuery(id+"F0.wireOp",EDGE,"E477"),sQuery(id+"F0.wireOp",EDGE,"E478"),sQuery(id+"F0.wireOp",EDGE,"E479"),sQuery(id+"F0.wireOp",EDGE,"E480"),sQuery(id+"F0.wireOp",EDGE,"E481"),sQuery(id+"F0.wireOp",EDGE,"E482"),sQuery(id+"F0.wireOp",EDGE,"E483"),sQuery(id+"F0.wireOp",EDGE,"E484"),sQuery(id+"F0.wireOp",EDGE,"E485"),sQuery(id+"F0.wireOp",EDGE,"E486"),sQuery(id+"F0.wireOp",EDGE,"E487"),sQuery(id+"F0.wireOp",EDGE,"E488"),sQuery(id+"F0.wireOp",EDGE,"E489"),sQuery(id+"F0.wireOp",EDGE,"E490"),sQuery(id+"F0.wireOp",EDGE,"E491"),sQuery(id+"F0.wireOp",EDGE,"E492"),sQuery(id+"F0.wireOp",EDGE,"E493"),sQuery(id+"F0.wireOp",EDGE,"E494"),sQuery(id+"F0.wireOp",EDGE,"E495"),sQuery(id+"F0.wireOp",EDGE,"E496"),sQuery(id+"F0.wireOp",EDGE,"E497"),sQuery(id+"F0.wireOp",EDGE,"E498"),sQuery(id+"F0.wireOp",EDGE,"E499"),sQuery(id+"F0.wireOp",EDGE,"E500"),sQuery(id+"F0.wireOp",EDGE,"E501"),sQuery(id+"F0.wireOp",EDGE,"E502"),sQuery(id+"F0.wireOp",EDGE,"E503"),sQuery(id+"F0.wireOp",EDGE,"E504"),sQuery(id+"F0.wireOp",EDGE,"E505"),sQuery(id+"F0.wireOp",EDGE,"E506"),sQuery(id+"F0.wireOp",EDGE,"E507"),sQuery(id+"F0.wireOp",EDGE,"E508"),sQuery(id+"F0.wireOp",EDGE,"E509"),sQuery(id+"F0.wireOp",EDGE,"E510"),sQuery(id+"F0.wireOp",EDGE,"E511"),sQuery(id+"F0.wireOp",EDGE,"E512"),sQuery(id+"F0.wireOp",EDGE,"E513"),sQuery(id+"F0.wireOp",EDGE,"E514"),sQuery(id+"F0.wireOp",EDGE,"E515"),sQuery(id+"F0.wireOp",EDGE,"E516"),sQuery(id+"F0.wireOp",EDGE,"E517"),sQuery(id+"F0.wireOp",EDGE,"E518"),sQuery(id+"F0.wireOp",EDGE,"E519"),sQuery(id+"F0.wireOp",EDGE,"E520"),sQuery(id+"F0.wireOp",EDGE,"E521"),sQuery(id+"F0.wireOp",EDGE,"E522"),sQuery(id+"F0.wireOp",EDGE,"E523"),sQuery(id+"F0.wireOp",EDGE,"E524"),sQuery(id+"F0.wireOp",EDGE,"E525"),sQuery(id+"F0.wireOp",EDGE,"E526"),sQuery(id+"F0.wireOp",EDGE,"E527"),sQuery(id+"F0.wireOp",EDGE,"E528"),sQuery(id+"F0.wireOp",EDGE,"E529"),sQuery(id+"F0.wireOp",EDGE,"E530"),sQuery(id+"F0.wireOp",EDGE,"E531"),sQuery(id+"F0.wireOp",EDGE,"E532"),sQuery(id+"F0.wireOp",EDGE,"E533"),sQuery(id+"F0.wireOp",EDGE,"E534"),sQuery(id+"F0.wireOp",EDGE,"E535"),sQuery(id+"F0.wireOp",EDGE,"E536"),sQuery(id+"F0.wireOp",EDGE,"E537"),sQuery(id+"F0.wireOp",EDGE,"E538"),sQuery(id+"F0.wireOp",EDGE,"E539"),sQuery(id+"F0.wireOp",EDGE,"E540"),sQuery(id+"F0.wireOp",EDGE,"E541"),sQuery(id+"F0.wireOp",EDGE,"E542"),sQuery(id+"F0.wireOp",EDGE,"E543"),sQuery(id+"F0.wireOp",EDGE,"E544"),sQuery(id+"F0.wireOp",EDGE,"E545"),sQuery(id+"F0.wireOp",EDGE,"E546"),sQuery(id+"F0.wireOp",EDGE,"E547"),sQuery(id+"F0.wireOp",EDGE,"E548"),sQuery(id+"F0.wireOp",EDGE,"E549"),sQuery(id+"F0.wireOp",EDGE,"E550"),sQuery(id+"F0.wireOp",EDGE,"E551"),sQuery(id+"F0.wireOp",EDGE,"E552"),sQuery(id+"F0.wireOp",EDGE,"E553"),sQuery(id+"F0.wireOp",EDGE,"E554"),sQuery(id+"F0.wireOp",EDGE,"E555"),sQuery(id+"F0.wireOp",EDGE,"E556"),sQuery(id+"F0.wireOp",EDGE,"E557"),sQuery(id+"F0.wireOp",EDGE,"E558"),sQuery(id+"F0.wireOp",EDGE,"E559"),sQuery(id+"F0.wireOp",EDGE,"E560"),sQuery(id+"F0.wireOp",EDGE,"E561"),sQuery(id+"F0.wireOp",EDGE,"E562"),sQuery(id+"F0.wireOp",EDGE,"E563"),sQuery(id+"F0.wireOp",EDGE,"E564"),sQuery(id+"F0.wireOp",EDGE,"E565"),sQuery(id+"F0.wireOp",EDGE,"E566"),sQuery(id+"F0.wireOp",EDGE,"E567"),sQuery(id+"F0.wireOp",EDGE,"E568"),sQuery(id+"F0.wireOp",EDGE,"E569"),sQuery(id+"F0.wireOp",EDGE,"E570"),sQuery(id+"F0.wireOp",EDGE,"E571"),sQuery(id+"F0.wireOp",EDGE,"E572"),sQuery(id+"F0.wireOp",EDGE,"E573"),sQuery(id+"F0.wireOp",EDGE,"E574"),sQuery(id+"F0.wireOp",EDGE,"E575"),sQuery(id+"F0.wireOp",EDGE,"E576"),sQuery(id+"F0.wireOp",EDGE,"E577"),sQuery(id+"F0.wireOp",EDGE,"E578"),sQuery(id+"F0.wireOp",EDGE,"E579"),sQuery(id+"F0.wireOp",EDGE,"E580"),sQuery(id+"F0.wireOp",EDGE,"E581"),sQuery(id+"F0.wireOp",EDGE,"E582"),sQuery(id+"F0.wireOp",EDGE,"E583"),sQuery(id+"F0.wireOp",EDGE,"E584"),sQuery(id+"F0.wireOp",EDGE,"E585"),sQuery(id+"F0.wireOp",EDGE,"E586"),sQuery(id+"F0.wireOp",EDGE,"E587"),sQuery(id+"F0.wireOp",EDGE,"E588"),sQuery(id+"F0.wireOp",EDGE,"E589"),sQuery(id+"F0.wireOp",EDGE,"E590"),sQuery(id+"F0.wireOp",EDGE,"E591"),sQuery(id+"F0.wireOp",EDGE,"E592"),sQuery(id+"F0.wireOp",EDGE,"E593"),sQuery(id+"F0.wireOp",EDGE,"E594"),sQuery(id+"F0.wireOp",EDGE,"E595"),sQuery(id+"F0.wireOp",EDGE,"E596"),sQuery(id+"F0.wireOp",EDGE,"E597"),sQuery(id+"F0.wireOp",EDGE,"E598"),sQuery(id+"F0.wireOp",EDGE,"E599"),sQuery(id+"F0.wireOp",EDGE,"E600"),sQuery(id+"F0.wireOp",EDGE,"E601"),sQuery(id+"F0.wireOp",EDGE,"E602"),sQuery(id+"F0.wireOp",EDGE,"E603"),sQuery(id+"F0.wireOp",EDGE,"E604"),sQuery(id+"F0.wireOp",EDGE,"E605"),sQuery(id+"F0.wireOp",EDGE,"E606"),sQuery(id+"F0.wireOp",EDGE,"E607"),sQuery(id+"F0.wireOp",EDGE,"E608"),sQuery(id+"F0.wireOp",EDGE,"E609"),sQuery(id+"F0.wireOp",EDGE,"E610"),sQuery(id+"F0.wireOp",EDGE,"E611"),sQuery(id+"F0.wireOp",EDGE,"E612"),sQuery(id+"F0.wireOp",EDGE,"E613"),sQuery(id+"F0.wireOp",EDGE,"E614"),sQuery(id+"F0.wireOp",EDGE,"E615"),sQuery(id+"F0.wireOp",EDGE,"E616"),sQuery(id+"F0.wireOp",EDGE,"E617"),sQuery(id+"F0.wireOp",EDGE,"E618"),sQuery(id+"F0.wireOp",EDGE,"E619"),sQuery(id+"F0.wireOp",EDGE,"E620"),sQuery(id+"F0.wireOp",EDGE,"E621"),sQuery(id+"F0.wireOp",EDGE,"E622"),sQuery(id+"F0.wireOp",EDGE,"E623"),sQuery(id+"F0.wireOp",EDGE,"E624"),sQuery(id+"F0.wireOp",EDGE,"E625"),sQuery(id+"F0.wireOp",EDGE,"E626"),sQuery(id+"F0.wireOp",EDGE,"E627"),sQuery(id+"F0.wireOp",EDGE,"E628"),sQuery(id+"F0.wireOp",EDGE,"E629"),sQuery(id+"F0.wireOp",EDGE,"E630"),sQuery(id+"F0.wireOp",EDGE,"E631"),sQuery(id+"F0.wireOp",EDGE,"E632"),sQuery(id+"F0.wireOp",EDGE,"E633"),sQuery(id+"F0.wireOp",EDGE,"E634"),sQuery(id+"F0.wireOp",EDGE,"E635"),sQuery(id+"F0.wireOp",EDGE,"E636"),sQuery(id+"F0.wireOp",EDGE,"E637"),sQuery(id+"F0.wireOp",EDGE,"E638"),sQuery(id+"F0.wireOp",EDGE,"E639"),sQuery(id+"F0.wireOp",EDGE,"E640"),sQuery(id+"F0.wireOp",EDGE,"E641"),sQuery(id+"F0.wireOp",EDGE,"E642"),sQuery(id+"F0.wireOp",EDGE,"E643"),sQuery(id+"F0.wireOp",EDGE,"E644"),sQuery(id+"F0.wireOp",EDGE,"E645"),sQuery(id+"F0.wireOp",EDGE,"E646"),sQuery(id+"F0.wireOp",EDGE,"E647"),sQuery(id+"F0.wireOp",EDGE,"E648"),sQuery(id+"F0.wireOp",EDGE,"E649"),sQuery(id+"F0.wireOp",EDGE,"E650"),sQuery(id+"F0.wireOp",EDGE,"E651"),sQuery(id+"F0.wireOp",EDGE,"E652"),sQuery(id+"F0.wireOp",EDGE,"E653"),sQuery(id+"F0.wireOp",EDGE,"E654"),sQuery(id+"F0.wireOp",EDGE,"E655"),sQuery(id+"F0.wireOp",EDGE,"E656"),sQuery(id+"F0.wireOp",EDGE,"E657"),sQuery(id+"F0.wireOp",EDGE,"E658"),sQuery(id+"F0.wireOp",EDGE,"E659"),sQuery(id+"F0.wireOp",EDGE,"E660"),sQuery(id+"F0.wireOp",EDGE,"E661"),sQuery(id+"F0.wireOp",EDGE,"E662"),sQuery(id+"F0.wireOp",EDGE,"E663"),sQuery(id+"F0.wireOp",EDGE,"E664"),sQuery(id+"F0.wireOp",EDGE,"E665"),sQuery(id+"F0.wireOp",EDGE,"E666"),sQuery(id+"F0.wireOp",EDGE,"E667"),sQuery(id+"F0.wireOp",EDGE,"E668"),sQuery(id+"F0.wireOp",EDGE,"E669"),sQuery(id+"F0.wireOp",EDGE,"E670"),sQuery(id+"F0.wireOp",EDGE,"E671"),sQuery(id+"F0.wireOp",EDGE,"E672"),sQuery(id+"F0.wireOp",EDGE,"E673"),sQuery(id+"F0.wireOp",EDGE,"E674"),sQuery(id+"F0.wireOp",EDGE,"E675"),sQuery(id+"F0.wireOp",EDGE,"E676"),sQuery(id+"F0.wireOp",EDGE,"E677"),sQuery(id+"F0.wireOp",EDGE,"E678"),sQuery(id+"F0.wireOp",EDGE,"E679"),sQuery(id+"F0.wireOp",EDGE,"E680"),sQuery(id+"F0.wireOp",EDGE,"E681"),sQuery(id+"F0.wireOp",EDGE,"E682"),sQuery(id+"F0.wireOp",EDGE,"E683"),sQuery(id+"F0.wireOp",EDGE,"E684"),sQuery(id+"F0.wireOp",EDGE,"E685"),sQuery(id+"F0.wireOp",EDGE,"E686"),sQuery(id+"F0.wireOp",EDGE,"E687"),sQuery(id+"F0.wireOp",EDGE,"E688"),sQuery(id+"F0.wireOp",EDGE,"E689"),sQuery(id+"F0.wireOp",EDGE,"E690"),sQuery(id+"F0.wireOp",EDGE,"E691"),sQuery(id+"F0.wireOp",EDGE,"E692"),sQuery(id+"F0.wireOp",EDGE,"E693"),sQuery(id+"F0.wireOp",EDGE,"E694"),sQuery(id+"F0.wireOp",EDGE,"E695"),sQuery(id+"F0.wireOp",EDGE,"E696"),sQuery(id+"F0.wireOp",EDGE,"E697"),sQuery(id+"F0.wireOp",EDGE,"E698"),sQuery(id+"F0.wireOp",EDGE,"E699"),sQuery(id+"F0.wireOp",EDGE,"E700"),sQuery(id+"F0.wireOp",EDGE,"E701"),sQuery(id+"F0.wireOp",EDGE,"E702"),sQuery(id+"F0.wireOp",EDGE,"E703"),sQuery(id+"F0.wireOp",EDGE,"E704"),sQuery(id+"F0.wireOp",EDGE,"E705"),sQuery(id+"F0.wireOp",EDGE,"E706"),sQuery(id+"F0.wireOp",EDGE,"E707"),sQuery(id+"F0.wireOp",EDGE,"E708"),sQuery(id+"F0.wireOp",EDGE,"E709"),sQuery(id+"F0.wireOp",EDGE,"E710"),sQuery(id+"F0.wireOp",EDGE,"E711"),sQuery(id+"F0.wireOp",EDGE,"E712"),sQuery(id+"F0.wireOp",EDGE,"E713"),sQuery(id+"F0.wireOp",EDGE,"E714"),sQuery(id+"F0.wireOp",EDGE,"E715"),sQuery(id+"F0.wireOp",EDGE,"E716"),sQuery(id+"F0.wireOp",EDGE,"E717"),sQuery(id+"F0.wireOp",EDGE,"E718"),sQuery(id+"F0.wireOp",EDGE,"E719"),sQuery(id+"F0.wireOp",EDGE,"E720"),sQuery(id+"F0.wireOp",EDGE,"E721"),sQuery(id+"F0.wireOp",EDGE,"E722"),sQuery(id+"F0.wireOp",EDGE,"E723"),sQuery(id+"F0.wireOp",EDGE,"E724"),sQuery(id+"F0.wireOp",EDGE,"E725"),sQuery(id+"F0.wireOp",EDGE,"E726"),sQuery(id+"F0.wireOp",EDGE,"E727"),sQuery(id+"F0.wireOp",EDGE,"E728"),sQuery(id+"F0.wireOp",EDGE,"E729"),sQuery(id+"F0.wireOp",EDGE,"E730"),sQuery(id+"F0.wireOp",EDGE,"E731"),sQuery(id+"F0.wireOp",EDGE,"E732"),sQuery(id+"F0.wireOp",EDGE,"E733"),sQuery(id+"F0.wireOp",EDGE,"E734"),sQuery(id+"F0.wireOp",EDGE,"E735"),sQuery(id+"F0.wireOp",EDGE,"E736"),sQuery(id+"F0.wireOp",EDGE,"E737"),sQuery(id+"F0.wireOp",EDGE,"E738"),sQuery(id+"F0.wireOp",EDGE,"E739"),sQuery(id+"F0.wireOp",EDGE,"E740"),sQuery(id+"F0.wireOp",EDGE,"E741"),sQuery(id+"F0.wireOp",EDGE,"E742"),sQuery(id+"F0.wireOp",EDGE,"E743"),sQuery(id+"F0.wireOp",EDGE,"E744"),sQuery(id+"F0.wireOp",EDGE,"E745"),sQuery(id+"F0.wireOp",EDGE,"E746"),sQuery(id+"F0.wireOp",EDGE,"E747"),sQuery(id+"F0.wireOp",EDGE,"E748"),sQuery(id+"F0.wireOp",EDGE,"E749"),sQuery(id+"F0.wireOp",EDGE,"E750"),sQuery(id+"F0.wireOp",EDGE,"E751"),sQuery(id+"F0.wireOp",EDGE,"E752"),sQuery(id+"F0.wireOp",EDGE,"E753"),sQuery(id+"F0.wireOp",EDGE,"E754"),sQuery(id+"F0.wireOp",EDGE,"E755"),sQuery(id+"F0.wireOp",EDGE,"E756"),sQuery(id+"F0.wireOp",EDGE,"E757"),sQuery(id+"F0.wireOp",EDGE,"E758"),sQuery(id+"F0.wireOp",EDGE,"E759"),sQuery(id+"F0.wireOp",EDGE,"E760"),sQuery(id+"F0.wireOp",EDGE,"E761"),sQuery(id+"F0.wireOp",EDGE,"E762"),sQuery(id+"F0.wireOp",EDGE,"E763"),sQuery(id+"F0.wireOp",EDGE,"E764"),sQuery(id+"F0.wireOp",EDGE,"E765"),sQuery(id+"F0.wireOp",EDGE,"E766"),sQuery(id+"F0.wireOp",EDGE,"E767"),sQuery(id+"F0.wireOp",EDGE,"E768"),sQuery(id+"F0.wireOp",EDGE,"E769"),sQuery(id+"F0.wireOp",EDGE,"E770"),sQuery(id+"F0.wireOp",EDGE,"E771"),sQuery(id+"F0.wireOp",EDGE,"E772"),sQuery(id+"F0.wireOp",EDGE,"E773"),sQuery(id+"F0.wireOp",EDGE,"E774"),sQuery(id+"F0.wireOp",EDGE,"E775"),sQuery(id+"F0.wireOp",EDGE,"E776"),sQuery(id+"F0.wireOp",EDGE,"E777"),sQuery(id+"F0.wireOp",EDGE,"E778"),sQuery(id+"F0.wireOp",EDGE,"E779"),sQuery(id+"F0.wireOp",EDGE,"E780"),sQuery(id+"F0.wireOp",EDGE,"E781"),sQuery(id+"F0.wireOp",EDGE,"E782"),sQuery(id+"F0.wireOp",EDGE,"E783"),sQuery(id+"F0.wireOp",EDGE,"E784"),sQuery(id+"F0.wireOp",EDGE,"E785"),sQuery(id+"F0.wireOp",EDGE,"E786"),sQuery(id+"F0.wireOp",EDGE,"E787"),sQuery(id+"F0.wireOp",EDGE,"E788"),sQuery(id+"F0.wireOp",EDGE,"E789"),sQuery(id+"F0.wireOp",EDGE,"E790"),sQuery(id+"F0.wireOp",EDGE,"E791"),sQuery(id+"F0.wireOp",EDGE,"E792"),sQuery(id+"F0.wireOp",EDGE,"E793"),sQuery(id+"F0.wireOp",EDGE,"E794"),sQuery(id+"F0.wireOp",EDGE,"E795"),sQuery(id+"F0.wireOp",EDGE,"E796"),sQuery(id+"F0.wireOp",EDGE,"E797"),sQuery(id+"F0.wireOp",EDGE,"E798"),sQuery(id+"F0.wireOp",EDGE,"E799"),sQuery(id+"F0.wireOp",EDGE,"E800"),sQuery(id+"F0.wireOp",EDGE,"E801"),sQuery(id+"F0.wireOp",EDGE,"E802"),sQuery(id+"F0.wireOp",EDGE,"E803"),sQuery(id+"F0.wireOp",EDGE,"E804"),sQuery(id+"F0.wireOp",EDGE,"E805"),sQuery(id+"F0.wireOp",EDGE,"E806"),sQuery(id+"F0.wireOp",EDGE,"E807"),sQuery(id+"F0.wireOp",EDGE,"E808"),sQuery(id+"F0.wireOp",EDGE,"E809"),sQuery(id+"F0.wireOp",EDGE,"E810"),sQuery(id+"F0.wireOp",EDGE,"E811"),sQuery(id+"F0.wireOp",EDGE,"E812"),sQuery(id+"F0.wireOp",EDGE,"E813"),sQuery(id+"F0.wireOp",EDGE,"E814"),sQuery(id+"F0.wireOp",EDGE,"E815"),sQuery(id+"F0.wireOp",EDGE,"E816"),sQuery(id+"F0.wireOp",EDGE,"E817"),sQuery(id+"F0.wireOp",EDGE,"E818"),sQuery(id+"F0.wireOp",EDGE,"E819"),sQuery(id+"F0.wireOp",EDGE,"E820"),sQuery(id+"F0.wireOp",EDGE,"E821"),sQuery(id+"F0.wireOp",EDGE,"E822"),sQuery(id+"F0.wireOp",EDGE,"E823"),sQuery(id+"F0.wireOp",EDGE,"E824"),sQuery(id+"F0.wireOp",EDGE,"E825"),sQuery(id+"F0.wireOp",EDGE,"E826"),sQuery(id+"F0.wireOp",EDGE,"E827"),sQuery(id+"F0.wireOp",EDGE,"E828"),sQuery(id+"F0.wireOp",EDGE,"E829"),sQuery(id+"F0.wireOp",EDGE,"E830"),sQuery(id+"F0.wireOp",EDGE,"E831"),sQuery(id+"F0.wireOp",EDGE,"E832"),sQuery(id+"F0.wireOp",EDGE,"E833"),sQuery(id+"F0.wireOp",EDGE,"E834"),sQuery(id+"F0.wireOp",EDGE,"E835"),sQuery(id+"F0.wireOp",EDGE,"E836"),sQuery(id+"F0.wireOp",EDGE,"E837"),sQuery(id+"F0.wireOp",EDGE,"E838"),sQuery(id+"F0.wireOp",EDGE,"E839"),sQuery(id+"F0.wireOp",EDGE,"E840"),sQuery(id+"F0.wireOp",EDGE,"E841"),sQuery(id+"F0.wireOp",EDGE,"E842"),sQuery(id+"F0.wireOp",EDGE,"E843"),sQuery(id+"F0.wireOp",EDGE,"E844"),sQuery(id+"F0.wireOp",EDGE,"E845"),sQuery(id+"F0.wireOp",EDGE,"E846"),sQuery(id+"F0.wireOp",EDGE,"E847"),sQuery(id+"F0.wireOp",EDGE,"E848"),sQuery(id+"F0.wireOp",EDGE,"E849"),sQuery(id+"F0.wireOp",EDGE,"E850"),sQuery(id+"F0.wireOp",EDGE,"E851"),sQuery(id+"F0.wireOp",EDGE,"E852"),sQuery(id+"F0.wireOp",EDGE,"E853"),sQuery(id+"F0.wireOp",EDGE,"E854"),sQuery(id+"F0.wireOp",EDGE,"E855"),sQuery(id+"F0.wireOp",EDGE,"E856"),sQuery(id+"F0.wireOp",EDGE,"E857"),sQuery(id+"F0.wireOp",EDGE,"E858"),sQuery(id+"F0.wireOp",EDGE,"E859"),sQuery(id+"F0.wireOp",EDGE,"E860"),sQuery(id+"F0.wireOp",EDGE,"E861"),sQuery(id+"F0.wireOp",EDGE,"E862"),sQuery(id+"F0.wireOp",EDGE,"E863"),sQuery(id+"F0.wireOp",EDGE,"E864"),sQuery(id+"F0.wireOp",EDGE,"E865"),sQuery(id+"F0.wireOp",EDGE,"E866"),sQuery(id+"F0.wireOp",EDGE,"E867"),sQuery(id+"F0.wireOp",EDGE,"E868"),sQuery(id+"F0.wireOp",EDGE,"E869"),sQuery(id+"F0.wireOp",EDGE,"E870"),sQuery(id+"F0.wireOp",EDGE,"E871"),sQuery(id+"F0.wireOp",EDGE,"E872"),sQuery(id+"F0.wireOp",EDGE,"E873"),sQuery(id+"F0.wireOp",EDGE,"E874"),sQuery(id+"F0.wireOp",EDGE,"E875"),sQuery(id+"F0.wireOp",EDGE,"E876"),sQuery(id+"F0.wireOp",EDGE,"E877"),sQuery(id+"F0.wireOp",EDGE,"E878"),sQuery(id+"F0.wireOp",EDGE,"E879"),sQuery(id+"F0.wireOp",EDGE,"E880"),sQuery(id+"F0.wireOp",EDGE,"E881"),sQuery(id+"F0.wireOp",EDGE,"E882"),sQuery(id+"F0.wireOp",EDGE,"E883"),sQuery(id+"F0.wireOp",EDGE,"E884"),sQuery(id+"F0.wireOp",EDGE,"E885"),sQuery(id+"F0.wireOp",EDGE,"E886"),sQuery(id+"F0.wireOp",EDGE,"E887"),sQuery(id+"F0.wireOp",EDGE,"E888"),sQuery(id+"F0.wireOp",EDGE,"E889"),sQuery(id+"F0.wireOp",EDGE,"E890"),sQuery(id+"F0.wireOp",EDGE,"E891"),sQuery(id+"F0.wireOp",EDGE,"E892"),sQuery(id+"F0.wireOp",EDGE,"E893"),sQuery(id+"F0.wireOp",EDGE,"E894"),sQuery(id+"F0.wireOp",EDGE,"E895"),sQuery(id+"F0.wireOp",EDGE,"E896"),sQuery(id+"F0.wireOp",EDGE,"E897"),sQuery(id+"F0.wireOp",EDGE,"E898"),sQuery(id+"F0.wireOp",EDGE,"E899"),sQuery(id+"F0.wireOp",EDGE,"E900"),sQuery(id+"F0.wireOp",EDGE,"E901"),sQuery(id+"F0.wireOp",EDGE,"E902"),sQuery(id+"F0.wireOp",EDGE,"E903"),sQuery(id+"F0.wireOp",EDGE,"E904"),sQuery(id+"F0.wireOp",EDGE,"E905"),sQuery(id+"F0.wireOp",EDGE,"E906"),sQuery(id+"F0.wireOp",EDGE,"E907"),sQuery(id+"F0.wireOp",EDGE,"E908"),sQuery(id+"F0.wireOp",EDGE,"E909"),sQuery(id+"F0.wireOp",EDGE,"E910"),sQuery(id+"F0.wireOp",EDGE,"E911"),sQuery(id+"F0.wireOp",EDGE,"E912"),sQuery(id+"F0.wireOp",EDGE,"E913"),sQuery(id+"F0.wireOp",EDGE,"E914"),sQuery(id+"F0.wireOp",EDGE,"E915"),sQuery(id+"F0.wireOp",EDGE,"E916"),sQuery(id+"F0.wireOp",EDGE,"E917"),sQuery(id+"F0.wireOp",EDGE,"E918"),sQuery(id+"F0.wireOp",EDGE,"E919"),sQuery(id+"F0.wireOp",EDGE,"E920"),sQuery(id+"F0.wireOp",EDGE,"E921"),sQuery(id+"F0.wireOp",EDGE,"E922"),sQuery(id+"F0.wireOp",EDGE,"E923"),sQuery(id+"F0.wireOp",EDGE,"E924"),sQuery(id+"F0.wireOp",EDGE,"E925"),sQuery(id+"F0.wireOp",EDGE,"E926"),sQuery(id+"F0.wireOp",EDGE,"E927"),sQuery(id+"F0.wireOp",EDGE,"E928"),sQuery(id+"F0.wireOp",EDGE,"E929"),sQuery(id+"F0.wireOp",EDGE,"E930"),sQuery(id+"F0.wireOp",EDGE,"E931"),sQuery(id+"F0.wireOp",EDGE,"E932"),sQuery(id+"F0.wireOp",EDGE,"E933"),sQuery(id+"F0.wireOp",EDGE,"E934"),sQuery(id+"F0.wireOp",EDGE,"E935"),sQuery(id+"F0.wireOp",EDGE,"E936"),sQuery(id+"F0.wireOp",EDGE,"E937"),sQuery(id+"F0.wireOp",EDGE,"E938"),sQuery(id+"F0.wireOp",EDGE,"E939"),sQuery(id+"F0.wireOp",EDGE,"E940"),sQuery(id+"F0.wireOp",EDGE,"E941"),sQuery(id+"F0.wireOp",EDGE,"E942"),sQuery(id+"F0.wireOp",EDGE,"E943"),sQuery(id+"F0.wireOp",EDGE,"E944"),sQuery(id+"F0.wireOp",EDGE,"E945"),sQuery(id+"F0.wireOp",EDGE,"E946"),sQuery(id+"F0.wireOp",EDGE,"E947"),sQuery(id+"F0.wireOp",EDGE,"E948"),sQuery(id+"F0.wireOp",EDGE,"E949"),sQuery(id+"F0.wireOp",EDGE,"E950"),sQuery(id+"F0.wireOp",EDGE,"E951"),sQuery(id+"F0.wireOp",EDGE,"E952"),sQuery(id+"F0.wireOp",EDGE,"E953"),sQuery(id+"F0.wireOp",EDGE,"E954"),sQuery(id+"F0.wireOp",EDGE,"E955"),sQuery(id+"F0.wireOp",EDGE,"E956"),sQuery(id+"F0.wireOp",EDGE,"E957"),sQuery(id+"F0.wireOp",EDGE,"E958"),sQuery(id+"F0.wireOp",EDGE,"E959"),sQuery(id+"F0.wireOp",EDGE,"E960"),sQuery(id+"F0.wireOp",EDGE,"E961"),sQuery(id+"F0.wireOp",EDGE,"E962"),sQuery(id+"F0.wireOp",EDGE,"E963"),sQuery(id+"F0.wireOp",EDGE,"E964"),sQuery(id+"F0.wireOp",EDGE,"E965"),sQuery(id+"F0.wireOp",EDGE,"E966"),sQuery(id+"F0.wireOp",EDGE,"E967"),sQuery(id+"F0.wireOp",EDGE,"E968"),sQuery(id+"F0.wireOp",EDGE,"E969"),sQuery(id+"F0.wireOp",EDGE,"E970"),sQuery(id+"F0.wireOp",EDGE,"E971"),sQuery(id+"F0.wireOp",EDGE,"E972"),sQuery(id+"F0.wireOp",EDGE,"E973"),sQuery(id+"F0.wireOp",EDGE,"E974"),sQuery(id+"F0.wireOp",EDGE,"E975"),sQuery(id+"F0.wireOp",EDGE,"E976"),sQuery(id+"F0.wireOp",EDGE,"E977"),sQuery(id+"F0.wireOp",EDGE,"E978"),sQuery(id+"F0.wireOp",EDGE,"E979"),sQuery(id+"F0.wireOp",EDGE,"E980"),sQuery(id+"F0.wireOp",EDGE,"E981"),sQuery(id+"F0.wireOp",EDGE,"E982"),sQuery(id+"F0.wireOp",EDGE,"E983"),sQuery(id+"F0.wireOp",EDGE,"E984"),sQuery(id+"F0.wireOp",EDGE,"E985"),sQuery(id+"F0.wireOp",EDGE,"E986"),sQuery(id+"F0.wireOp",EDGE,"E987"),sQuery(id+"F0.wireOp",EDGE,"E988"),sQuery(id+"F0.wireOp",EDGE,"E989"),sQuery(id+"F0.wireOp",EDGE,"E990"),sQuery(id+"F0.wireOp",EDGE,"E991"),sQuery(id+"F0.wireOp",EDGE,"E992"),sQuery(id+"F0.wireOp",EDGE,"E993"),sQuery(id+"F0.wireOp",EDGE,"E994"),sQuery(id+"F0.wireOp",EDGE,"E995"),sQuery(id+"F0.wireOp",EDGE,"E996"),sQuery(id+"F0.wireOp",EDGE,"E997"),sQuery(id+"F0.wireOp",EDGE,"E998"),sQuery(id+"F0.wireOp",EDGE,"E999"),sQuery(id+"F0.wireOp",EDGE,"E1000"),sQuery(id+"F0.wireOp",EDGE,"E1001"),sQuery(id+"F0.wireOp",EDGE,"E1002"),sQuery(id+"F0.wireOp",EDGE,"E1003"),sQuery(id+"F0.wireOp",EDGE,"E1004"),sQuery(id+"F0.wireOp",EDGE,"E1005"),sQuery(id+"F0.wireOp",EDGE,"E1006"),sQuery(id+"F0.wireOp",EDGE,"E1007"),sQuery(id+"F0.wireOp",EDGE,"E1008"),sQuery(id+"F0.wireOp",EDGE,"E1009"),sQuery(id+"F0.wireOp",EDGE,"E1010"),sQuery(id+"F0.wireOp",EDGE,"E1011"),sQuery(id+"F0.wireOp",EDGE,"E1012"),sQuery(id+"F0.wireOp",EDGE,"E1013"),sQuery(id+"F0.wireOp",EDGE,"E1014"),sQuery(id+"F0.wireOp",EDGE,"E1015"),sQuery(id+"F0.wireOp",EDGE,"E1016"),sQuery(id+"F0.wireOp",EDGE,"E1017"),sQuery(id+"F0.wireOp",EDGE,"E1018"),sQuery(id+"F0.wireOp",EDGE,"E1019"),sQuery(id+"F0.wireOp",EDGE,"E1020"),sQuery(id+"F0.wireOp",EDGE,"E1021"),sQuery(id+"F0.wireOp",EDGE,"E1022"),sQuery(id+"F0.wireOp",EDGE,"E1023"),sQuery(id+"F0.wireOp",EDGE,"E1024"),sQuery(id+"F0.wireOp",EDGE,"E1025"),sQuery(id+"F0.wireOp",EDGE,"E1026"),sQuery(id+"F0.wireOp",EDGE,"E1027"),sQuery(id+"F0.wireOp",EDGE,"E1028"),sQuery(id+"F0.wireOp",EDGE,"E1029"),sQuery(id+"F0.wireOp",EDGE,"E1030"),sQuery(id+"F0.wireOp",EDGE,"E1031"),sQuery(id+"F0.wireOp",EDGE,"E1032"),sQuery(id+"F0.wireOp",EDGE,"E1033"),sQuery(id+"F0.wireOp",EDGE,"E1034"),sQuery(id+"F0.wireOp",EDGE,"E1035"),sQuery(id+"F0.wireOp",EDGE,"E1036"),sQuery(id+"F0.wireOp",EDGE,"E1037"),sQuery(id+"F0.wireOp",EDGE,"E1038"),sQuery(id+"F0.wireOp",EDGE,"E1039"),sQuery(id+"F0.wireOp",EDGE,"E1040")])],"isStart":false});
            extrude(context, id + "F2", {"entities" : qUnion([Q0]), "operationType" : NewBodyOperationType.REMOVE, "oppositeDirection" : true, "depth" : 15 * mm});
        }
        {
            var Q0;
            Q0=makeQuery(id+"F2.boolean.opBoolean","COPY",FACE,{"derivedFrom":makeQuery(id+"F2.opExtrude","CAP_FACE",FACE,{"disambiguationData":[OSD([sQuery(id+"F0.wireOp",EDGE,"E0"),sQuery(id+"F0.wireOp",EDGE,"E1"),sQuery(id+"F0.wireOp",EDGE,"E2"),sQuery(id+"F0.wireOp",EDGE,"E3"),sQuery(id+"F0.wireOp",EDGE,"E4"),sQuery(id+"F0.wireOp",EDGE,"E5"),sQuery(id+"F0.wireOp",EDGE,"E6"),sQuery(id+"F0.wireOp",EDGE,"E7"),sQuery(id+"F0.wireOp",EDGE,"E8"),sQuery(id+"F0.wireOp",EDGE,"E9"),sQuery(id+"F0.wireOp",EDGE,"E10"),sQuery(id+"F0.wireOp",EDGE,"E11"),sQuery(id+"F0.wireOp",EDGE,"E12"),sQuery(id+"F0.wireOp",EDGE,"E13"),sQuery(id+"F0.wireOp",EDGE,"E14"),sQuery(id+"F0.wireOp",EDGE,"E15"),sQuery(id+"F0.wireOp",EDGE,"E16"),sQuery(id+"F0.wireOp",EDGE,"E17"),sQuery(id+"F0.wireOp",EDGE,"E18"),sQuery(id+"F0.wireOp",EDGE,"E19"),sQuery(id+"F0.wireOp",EDGE,"E20"),sQuery(id+"F0.wireOp",EDGE,"E21"),sQuery(id+"F0.wireOp",EDGE,"E22"),sQuery(id+"F0.wireOp",EDGE,"E23"),sQuery(id+"F0.wireOp",EDGE,"E24"),sQuery(id+"F0.wireOp",EDGE,"E25"),sQuery(id+"F0.wireOp",EDGE,"E26"),sQuery(id+"F0.wireOp",EDGE,"E27"),sQuery(id+"F0.wireOp",EDGE,"E28"),sQuery(id+"F0.wireOp",EDGE,"E29"),sQuery(id+"F0.wireOp",EDGE,"E30"),sQuery(id+"F0.wireOp",EDGE,"E31"),sQuery(id+"F0.wireOp",EDGE,"E32"),sQuery(id+"F0.wireOp",EDGE,"E33"),sQuery(id+"F0.wireOp",EDGE,"E34"),sQuery(id+"F0.wireOp",EDGE,"E35"),sQuery(id+"F0.wireOp",EDGE,"E36"),sQuery(id+"F0.wireOp",EDGE,"E37"),sQuery(id+"F0.wireOp",EDGE,"E38"),sQuery(id+"F0.wireOp",EDGE,"E39"),sQuery(id+"F0.wireOp",EDGE,"E40"),sQuery(id+"F0.wireOp",EDGE,"E41"),sQuery(id+"F0.wireOp",EDGE,"E42"),sQuery(id+"F0.wireOp",EDGE,"E43"),sQuery(id+"F0.wireOp",EDGE,"E44"),sQuery(id+"F0.wireOp",EDGE,"E45"),sQuery(id+"F0.wireOp",EDGE,"E46"),sQuery(id+"F0.wireOp",EDGE,"E47"),sQuery(id+"F0.wireOp",EDGE,"E48"),sQuery(id+"F0.wireOp",EDGE,"E49"),sQuery(id+"F0.wireOp",EDGE,"E50"),sQuery(id+"F0.wireOp",EDGE,"E51"),sQuery(id+"F0.wireOp",EDGE,"E52"),sQuery(id+"F0.wireOp",EDGE,"E53"),sQuery(id+"F0.wireOp",EDGE,"E54"),sQuery(id+"F0.wireOp",EDGE,"E55"),sQuery(id+"F0.wireOp",EDGE,"E56"),sQuery(id+"F0.wireOp",EDGE,"E57"),sQuery(id+"F0.wireOp",EDGE,"E58"),sQuery(id+"F0.wireOp",EDGE,"E59"),sQuery(id+"F0.wireOp",EDGE,"E60"),sQuery(id+"F0.wireOp",EDGE,"E61"),sQuery(id+"F0.wireOp",EDGE,"E62"),sQuery(id+"F0.wireOp",EDGE,"E63"),sQuery(id+"F0.wireOp",EDGE,"E64"),sQuery(id+"F0.wireOp",EDGE,"E65"),sQuery(id+"F0.wireOp",EDGE,"E66"),sQuery(id+"F0.wireOp",EDGE,"E67"),sQuery(id+"F0.wireOp",EDGE,"E68"),sQuery(id+"F0.wireOp",EDGE,"E69"),sQuery(id+"F0.wireOp",EDGE,"E70"),sQuery(id+"F0.wireOp",EDGE,"E71"),sQuery(id+"F0.wireOp",EDGE,"E72"),sQuery(id+"F0.wireOp",EDGE,"E73"),sQuery(id+"F0.wireOp",EDGE,"E74"),sQuery(id+"F0.wireOp",EDGE,"E75"),sQuery(id+"F0.wireOp",EDGE,"E76"),sQuery(id+"F0.wireOp",EDGE,"E77"),sQuery(id+"F0.wireOp",EDGE,"E78"),sQuery(id+"F0.wireOp",EDGE,"E79"),sQuery(id+"F0.wireOp",EDGE,"E80"),sQuery(id+"F0.wireOp",EDGE,"E81"),sQuery(id+"F0.wireOp",EDGE,"E82"),sQuery(id+"F0.wireOp",EDGE,"E83"),sQuery(id+"F0.wireOp",EDGE,"E84"),sQuery(id+"F0.wireOp",EDGE,"E85"),sQuery(id+"F0.wireOp",EDGE,"E86"),sQuery(id+"F0.wireOp",EDGE,"E87"),sQuery(id+"F0.wireOp",EDGE,"E88"),sQuery(id+"F0.wireOp",EDGE,"E89"),sQuery(id+"F0.wireOp",EDGE,"E90"),sQuery(id+"F0.wireOp",EDGE,"E91"),sQuery(id+"F0.wireOp",EDGE,"E92"),sQuery(id+"F0.wireOp",EDGE,"E93"),sQuery(id+"F0.wireOp",EDGE,"E94"),sQuery(id+"F0.wireOp",EDGE,"E95"),sQuery(id+"F0.wireOp",EDGE,"E96"),sQuery(id+"F0.wireOp",EDGE,"E97"),sQuery(id+"F0.wireOp",EDGE,"E98"),sQuery(id+"F0.wireOp",EDGE,"E99"),sQuery(id+"F0.wireOp",EDGE,"E100"),sQuery(id+"F0.wireOp",EDGE,"E101"),sQuery(id+"F0.wireOp",EDGE,"E102"),sQuery(id+"F0.wireOp",EDGE,"E103"),sQuery(id+"F0.wireOp",EDGE,"E104"),sQuery(id+"F0.wireOp",EDGE,"E105"),sQuery(id+"F0.wireOp",EDGE,"E106"),sQuery(id+"F0.wireOp",EDGE,"E107"),sQuery(id+"F0.wireOp",EDGE,"E108"),sQuery(id+"F0.wireOp",EDGE,"E109"),sQuery(id+"F0.wireOp",EDGE,"E110"),sQuery(id+"F0.wireOp",EDGE,"E111"),sQuery(id+"F0.wireOp",EDGE,"E112"),sQuery(id+"F0.wireOp",EDGE,"E113"),sQuery(id+"F0.wireOp",EDGE,"E114"),sQuery(id+"F0.wireOp",EDGE,"E115"),sQuery(id+"F0.wireOp",EDGE,"E116"),sQuery(id+"F0.wireOp",EDGE,"E117"),sQuery(id+"F0.wireOp",EDGE,"E118"),sQuery(id+"F0.wireOp",EDGE,"E119"),sQuery(id+"F0.wireOp",EDGE,"E120"),sQuery(id+"F0.wireOp",EDGE,"E121"),sQuery(id+"F0.wireOp",EDGE,"E122"),sQuery(id+"F0.wireOp",EDGE,"E123"),sQuery(id+"F0.wireOp",EDGE,"E124"),sQuery(id+"F0.wireOp",EDGE,"E125"),sQuery(id+"F0.wireOp",EDGE,"E126"),sQuery(id+"F0.wireOp",EDGE,"E127"),sQuery(id+"F0.wireOp",EDGE,"E128"),sQuery(id+"F0.wireOp",EDGE,"E129"),sQuery(id+"F0.wireOp",EDGE,"E130"),sQuery(id+"F0.wireOp",EDGE,"E131"),sQuery(id+"F0.wireOp",EDGE,"E132"),sQuery(id+"F0.wireOp",EDGE,"E133"),sQuery(id+"F0.wireOp",EDGE,"E134"),sQuery(id+"F0.wireOp",EDGE,"E135"),sQuery(id+"F0.wireOp",EDGE,"E136"),sQuery(id+"F0.wireOp",EDGE,"E137"),sQuery(id+"F0.wireOp",EDGE,"E138"),sQuery(id+"F0.wireOp",EDGE,"E139"),sQuery(id+"F0.wireOp",EDGE,"E140"),sQuery(id+"F0.wireOp",EDGE,"E141"),sQuery(id+"F0.wireOp",EDGE,"E142"),sQuery(id+"F0.wireOp",EDGE,"E143"),sQuery(id+"F0.wireOp",EDGE,"E144"),sQuery(id+"F0.wireOp",EDGE,"E145"),sQuery(id+"F0.wireOp",EDGE,"E146"),sQuery(id+"F0.wireOp",EDGE,"E147"),sQuery(id+"F0.wireOp",EDGE,"E148"),sQuery(id+"F0.wireOp",EDGE,"E149"),sQuery(id+"F0.wireOp",EDGE,"E150"),sQuery(id+"F0.wireOp",EDGE,"E151"),sQuery(id+"F0.wireOp",EDGE,"E152"),sQuery(id+"F0.wireOp",EDGE,"E153"),sQuery(id+"F0.wireOp",EDGE,"E154"),sQuery(id+"F0.wireOp",EDGE,"E155"),sQuery(id+"F0.wireOp",EDGE,"E156"),sQuery(id+"F0.wireOp",EDGE,"E157"),sQuery(id+"F0.wireOp",EDGE,"E158"),sQuery(id+"F0.wireOp",EDGE,"E159"),sQuery(id+"F0.wireOp",EDGE,"E160"),sQuery(id+"F0.wireOp",EDGE,"E161"),sQuery(id+"F0.wireOp",EDGE,"E162"),sQuery(id+"F0.wireOp",EDGE,"E163"),sQuery(id+"F0.wireOp",EDGE,"E164"),sQuery(id+"F0.wireOp",EDGE,"E165"),sQuery(id+"F0.wireOp",EDGE,"E166"),sQuery(id+"F0.wireOp",EDGE,"E167"),sQuery(id+"F0.wireOp",EDGE,"E168"),sQuery(id+"F0.wireOp",EDGE,"E169"),sQuery(id+"F0.wireOp",EDGE,"E170"),sQuery(id+"F0.wireOp",EDGE,"E171"),sQuery(id+"F0.wireOp",EDGE,"E172"),sQuery(id+"F0.wireOp",EDGE,"E173"),sQuery(id+"F0.wireOp",EDGE,"E174"),sQuery(id+"F0.wireOp",EDGE,"E175"),sQuery(id+"F0.wireOp",EDGE,"E176"),sQuery(id+"F0.wireOp",EDGE,"E177"),sQuery(id+"F0.wireOp",EDGE,"E178"),sQuery(id+"F0.wireOp",EDGE,"E179"),sQuery(id+"F0.wireOp",EDGE,"E180"),sQuery(id+"F0.wireOp",EDGE,"E181"),sQuery(id+"F0.wireOp",EDGE,"E182"),sQuery(id+"F0.wireOp",EDGE,"E183"),sQuery(id+"F0.wireOp",EDGE,"E184"),sQuery(id+"F0.wireOp",EDGE,"E185"),sQuery(id+"F0.wireOp",EDGE,"E186"),sQuery(id+"F0.wireOp",EDGE,"E187"),sQuery(id+"F0.wireOp",EDGE,"E188"),sQuery(id+"F0.wireOp",EDGE,"E189"),sQuery(id+"F0.wireOp",EDGE,"E190"),sQuery(id+"F0.wireOp",EDGE,"E191"),sQuery(id+"F0.wireOp",EDGE,"E192"),sQuery(id+"F0.wireOp",EDGE,"E193"),sQuery(id+"F0.wireOp",EDGE,"E194"),sQuery(id+"F0.wireOp",EDGE,"E195"),sQuery(id+"F0.wireOp",EDGE,"E196"),sQuery(id+"F0.wireOp",EDGE,"E197"),sQuery(id+"F0.wireOp",EDGE,"E198"),sQuery(id+"F0.wireOp",EDGE,"E199"),sQuery(id+"F0.wireOp",EDGE,"E200"),sQuery(id+"F0.wireOp",EDGE,"E201"),sQuery(id+"F0.wireOp",EDGE,"E202"),sQuery(id+"F0.wireOp",EDGE,"E203"),sQuery(id+"F0.wireOp",EDGE,"E204"),sQuery(id+"F0.wireOp",EDGE,"E205"),sQuery(id+"F0.wireOp",EDGE,"E206"),sQuery(id+"F0.wireOp",EDGE,"E207"),sQuery(id+"F0.wireOp",EDGE,"E208"),sQuery(id+"F0.wireOp",EDGE,"E209"),sQuery(id+"F0.wireOp",EDGE,"E210"),sQuery(id+"F0.wireOp",EDGE,"E211"),sQuery(id+"F0.wireOp",EDGE,"E212"),sQuery(id+"F0.wireOp",EDGE,"E213"),sQuery(id+"F0.wireOp",EDGE,"E214"),sQuery(id+"F0.wireOp",EDGE,"E215"),sQuery(id+"F0.wireOp",EDGE,"E216"),sQuery(id+"F0.wireOp",EDGE,"E217"),sQuery(id+"F0.wireOp",EDGE,"E218"),sQuery(id+"F0.wireOp",EDGE,"E219"),sQuery(id+"F0.wireOp",EDGE,"E220"),sQuery(id+"F0.wireOp",EDGE,"E221"),sQuery(id+"F0.wireOp",EDGE,"E222"),sQuery(id+"F0.wireOp",EDGE,"E223"),sQuery(id+"F0.wireOp",EDGE,"E224"),sQuery(id+"F0.wireOp",EDGE,"E225"),sQuery(id+"F0.wireOp",EDGE,"E226"),sQuery(id+"F0.wireOp",EDGE,"E227"),sQuery(id+"F0.wireOp",EDGE,"E228"),sQuery(id+"F0.wireOp",EDGE,"E229"),sQuery(id+"F0.wireOp",EDGE,"E230"),sQuery(id+"F0.wireOp",EDGE,"E231"),sQuery(id+"F0.wireOp",EDGE,"E232"),sQuery(id+"F0.wireOp",EDGE,"E233"),sQuery(id+"F0.wireOp",EDGE,"E234"),sQuery(id+"F0.wireOp",EDGE,"E235"),sQuery(id+"F0.wireOp",EDGE,"E236"),sQuery(id+"F0.wireOp",EDGE,"E237"),sQuery(id+"F0.wireOp",EDGE,"E238"),sQuery(id+"F0.wireOp",EDGE,"E239"),sQuery(id+"F0.wireOp",EDGE,"E240"),sQuery(id+"F0.wireOp",EDGE,"E241"),sQuery(id+"F0.wireOp",EDGE,"E242"),sQuery(id+"F0.wireOp",EDGE,"E243"),sQuery(id+"F0.wireOp",EDGE,"E244"),sQuery(id+"F0.wireOp",EDGE,"E245"),sQuery(id+"F0.wireOp",EDGE,"E246"),sQuery(id+"F0.wireOp",EDGE,"E247"),sQuery(id+"F0.wireOp",EDGE,"E248"),sQuery(id+"F0.wireOp",EDGE,"E249"),sQuery(id+"F0.wireOp",EDGE,"E250"),sQuery(id+"F0.wireOp",EDGE,"E251"),sQuery(id+"F0.wireOp",EDGE,"E252"),sQuery(id+"F0.wireOp",EDGE,"E253"),sQuery(id+"F0.wireOp",EDGE,"E254"),sQuery(id+"F0.wireOp",EDGE,"E255"),sQuery(id+"F0.wireOp",EDGE,"E256"),sQuery(id+"F0.wireOp",EDGE,"E257"),sQuery(id+"F0.wireOp",EDGE,"E258"),sQuery(id+"F0.wireOp",EDGE,"E259"),sQuery(id+"F0.wireOp",EDGE,"E260"),sQuery(id+"F0.wireOp",EDGE,"E261"),sQuery(id+"F0.wireOp",EDGE,"E262"),sQuery(id+"F0.wireOp",EDGE,"E263"),sQuery(id+"F0.wireOp",EDGE,"E264"),sQuery(id+"F0.wireOp",EDGE,"E265"),sQuery(id+"F0.wireOp",EDGE,"E266"),sQuery(id+"F0.wireOp",EDGE,"E267"),sQuery(id+"F0.wireOp",EDGE,"E268"),sQuery(id+"F0.wireOp",EDGE,"E269"),sQuery(id+"F0.wireOp",EDGE,"E270"),sQuery(id+"F0.wireOp",EDGE,"E271"),sQuery(id+"F0.wireOp",EDGE,"E272"),sQuery(id+"F0.wireOp",EDGE,"E273"),sQuery(id+"F0.wireOp",EDGE,"E274"),sQuery(id+"F0.wireOp",EDGE,"E275"),sQuery(id+"F0.wireOp",EDGE,"E276"),sQuery(id+"F0.wireOp",EDGE,"E277"),sQuery(id+"F0.wireOp",EDGE,"E278"),sQuery(id+"F0.wireOp",EDGE,"E279"),sQuery(id+"F0.wireOp",EDGE,"E280"),sQuery(id+"F0.wireOp",EDGE,"E281"),sQuery(id+"F0.wireOp",EDGE,"E282"),sQuery(id+"F0.wireOp",EDGE,"E283"),sQuery(id+"F0.wireOp",EDGE,"E284"),sQuery(id+"F0.wireOp",EDGE,"E285"),sQuery(id+"F0.wireOp",EDGE,"E286"),sQuery(id+"F0.wireOp",EDGE,"E287"),sQuery(id+"F0.wireOp",EDGE,"E288"),sQuery(id+"F0.wireOp",EDGE,"E289"),sQuery(id+"F0.wireOp",EDGE,"E290"),sQuery(id+"F0.wireOp",EDGE,"E291"),sQuery(id+"F0.wireOp",EDGE,"E292"),sQuery(id+"F0.wireOp",EDGE,"E293"),sQuery(id+"F0.wireOp",EDGE,"E294"),sQuery(id+"F0.wireOp",EDGE,"E295"),sQuery(id+"F0.wireOp",EDGE,"E296"),sQuery(id+"F0.wireOp",EDGE,"E297"),sQuery(id+"F0.wireOp",EDGE,"E298"),sQuery(id+"F0.wireOp",EDGE,"E299"),sQuery(id+"F0.wireOp",EDGE,"E300"),sQuery(id+"F0.wireOp",EDGE,"E301"),sQuery(id+"F0.wireOp",EDGE,"E302"),sQuery(id+"F0.wireOp",EDGE,"E303"),sQuery(id+"F0.wireOp",EDGE,"E304"),sQuery(id+"F0.wireOp",EDGE,"E305"),sQuery(id+"F0.wireOp",EDGE,"E306"),sQuery(id+"F0.wireOp",EDGE,"E307"),sQuery(id+"F0.wireOp",EDGE,"E308"),sQuery(id+"F0.wireOp",EDGE,"E309"),sQuery(id+"F0.wireOp",EDGE,"E310"),sQuery(id+"F0.wireOp",EDGE,"E311"),sQuery(id+"F0.wireOp",EDGE,"E312"),sQuery(id+"F0.wireOp",EDGE,"E313"),sQuery(id+"F0.wireOp",EDGE,"E314"),sQuery(id+"F0.wireOp",EDGE,"E315"),sQuery(id+"F0.wireOp",EDGE,"E316"),sQuery(id+"F0.wireOp",EDGE,"E317"),sQuery(id+"F0.wireOp",EDGE,"E318"),sQuery(id+"F0.wireOp",EDGE,"E319"),sQuery(id+"F0.wireOp",EDGE,"E320"),sQuery(id+"F0.wireOp",EDGE,"E321"),sQuery(id+"F0.wireOp",EDGE,"E322"),sQuery(id+"F0.wireOp",EDGE,"E323"),sQuery(id+"F0.wireOp",EDGE,"E324"),sQuery(id+"F0.wireOp",EDGE,"E325"),sQuery(id+"F0.wireOp",EDGE,"E326"),sQuery(id+"F0.wireOp",EDGE,"E327"),sQuery(id+"F0.wireOp",EDGE,"E328"),sQuery(id+"F0.wireOp",EDGE,"E329"),sQuery(id+"F0.wireOp",EDGE,"E330"),sQuery(id+"F0.wireOp",EDGE,"E331"),sQuery(id+"F0.wireOp",EDGE,"E332"),sQuery(id+"F0.wireOp",EDGE,"E333"),sQuery(id+"F0.wireOp",EDGE,"E334"),sQuery(id+"F0.wireOp",EDGE,"E335"),sQuery(id+"F0.wireOp",EDGE,"E336"),sQuery(id+"F0.wireOp",EDGE,"E337"),sQuery(id+"F0.wireOp",EDGE,"E338"),sQuery(id+"F0.wireOp",EDGE,"E339"),sQuery(id+"F0.wireOp",EDGE,"E340"),sQuery(id+"F0.wireOp",EDGE,"E341"),sQuery(id+"F0.wireOp",EDGE,"E342"),sQuery(id+"F0.wireOp",EDGE,"E343"),sQuery(id+"F0.wireOp",EDGE,"E344"),sQuery(id+"F0.wireOp",EDGE,"E345"),sQuery(id+"F0.wireOp",EDGE,"E346"),sQuery(id+"F0.wireOp",EDGE,"E347"),sQuery(id+"F0.wireOp",EDGE,"E348"),sQuery(id+"F0.wireOp",EDGE,"E349"),sQuery(id+"F0.wireOp",EDGE,"E350"),sQuery(id+"F0.wireOp",EDGE,"E351"),sQuery(id+"F0.wireOp",EDGE,"E352"),sQuery(id+"F0.wireOp",EDGE,"E353"),sQuery(id+"F0.wireOp",EDGE,"E354"),sQuery(id+"F0.wireOp",EDGE,"E355"),sQuery(id+"F0.wireOp",EDGE,"E356"),sQuery(id+"F0.wireOp",EDGE,"E357"),sQuery(id+"F0.wireOp",EDGE,"E358"),sQuery(id+"F0.wireOp",EDGE,"E359"),sQuery(id+"F0.wireOp",EDGE,"E360"),sQuery(id+"F0.wireOp",EDGE,"E361"),sQuery(id+"F0.wireOp",EDGE,"E362"),sQuery(id+"F0.wireOp",EDGE,"E363"),sQuery(id+"F0.wireOp",EDGE,"E364"),sQuery(id+"F0.wireOp",EDGE,"E365"),sQuery(id+"F0.wireOp",EDGE,"E366"),sQuery(id+"F0.wireOp",EDGE,"E367"),sQuery(id+"F0.wireOp",EDGE,"E368"),sQuery(id+"F0.wireOp",EDGE,"E369"),sQuery(id+"F0.wireOp",EDGE,"E370"),sQuery(id+"F0.wireOp",EDGE,"E371"),sQuery(id+"F0.wireOp",EDGE,"E372"),sQuery(id+"F0.wireOp",EDGE,"E373"),sQuery(id+"F0.wireOp",EDGE,"E374"),sQuery(id+"F0.wireOp",EDGE,"E375"),sQuery(id+"F0.wireOp",EDGE,"E376"),sQuery(id+"F0.wireOp",EDGE,"E377"),sQuery(id+"F0.wireOp",EDGE,"E378"),sQuery(id+"F0.wireOp",EDGE,"E379"),sQuery(id+"F0.wireOp",EDGE,"E380"),sQuery(id+"F0.wireOp",EDGE,"E381"),sQuery(id+"F0.wireOp",EDGE,"E382"),sQuery(id+"F0.wireOp",EDGE,"E383"),sQuery(id+"F0.wireOp",EDGE,"E384"),sQuery(id+"F0.wireOp",EDGE,"E385"),sQuery(id+"F0.wireOp",EDGE,"E386"),sQuery(id+"F0.wireOp",EDGE,"E387"),sQuery(id+"F0.wireOp",EDGE,"E388"),sQuery(id+"F0.wireOp",EDGE,"E389"),sQuery(id+"F0.wireOp",EDGE,"E390"),sQuery(id+"F0.wireOp",EDGE,"E391"),sQuery(id+"F0.wireOp",EDGE,"E392"),sQuery(id+"F0.wireOp",EDGE,"E393"),sQuery(id+"F0.wireOp",EDGE,"E394"),sQuery(id+"F0.wireOp",EDGE,"E395"),sQuery(id+"F0.wireOp",EDGE,"E396"),sQuery(id+"F0.wireOp",EDGE,"E397"),sQuery(id+"F0.wireOp",EDGE,"E398"),sQuery(id+"F0.wireOp",EDGE,"E399"),sQuery(id+"F0.wireOp",EDGE,"E400"),sQuery(id+"F0.wireOp",EDGE,"E401"),sQuery(id+"F0.wireOp",EDGE,"E402"),sQuery(id+"F0.wireOp",EDGE,"E403"),sQuery(id+"F0.wireOp",EDGE,"E404"),sQuery(id+"F0.wireOp",EDGE,"E405"),sQuery(id+"F0.wireOp",EDGE,"E406"),sQuery(id+"F0.wireOp",EDGE,"E407"),sQuery(id+"F0.wireOp",EDGE,"E408"),sQuery(id+"F0.wireOp",EDGE,"E409"),sQuery(id+"F0.wireOp",EDGE,"E410"),sQuery(id+"F0.wireOp",EDGE,"E411"),sQuery(id+"F0.wireOp",EDGE,"E412"),sQuery(id+"F0.wireOp",EDGE,"E413"),sQuery(id+"F0.wireOp",EDGE,"E414"),sQuery(id+"F0.wireOp",EDGE,"E415"),sQuery(id+"F0.wireOp",EDGE,"E416"),sQuery(id+"F0.wireOp",EDGE,"E417"),sQuery(id+"F0.wireOp",EDGE,"E418"),sQuery(id+"F0.wireOp",EDGE,"E419"),sQuery(id+"F0.wireOp",EDGE,"E420"),sQuery(id+"F0.wireOp",EDGE,"E421"),sQuery(id+"F0.wireOp",EDGE,"E422"),sQuery(id+"F0.wireOp",EDGE,"E423"),sQuery(id+"F0.wireOp",EDGE,"E424"),sQuery(id+"F0.wireOp",EDGE,"E425"),sQuery(id+"F0.wireOp",EDGE,"E426"),sQuery(id+"F0.wireOp",EDGE,"E427"),sQuery(id+"F0.wireOp",EDGE,"E428"),sQuery(id+"F0.wireOp",EDGE,"E429"),sQuery(id+"F0.wireOp",EDGE,"E430"),sQuery(id+"F0.wireOp",EDGE,"E431"),sQuery(id+"F0.wireOp",EDGE,"E432"),sQuery(id+"F0.wireOp",EDGE,"E433"),sQuery(id+"F0.wireOp",EDGE,"E434"),sQuery(id+"F0.wireOp",EDGE,"E435"),sQuery(id+"F0.wireOp",EDGE,"E436"),sQuery(id+"F0.wireOp",EDGE,"E437"),sQuery(id+"F0.wireOp",EDGE,"E438"),sQuery(id+"F0.wireOp",EDGE,"E439"),sQuery(id+"F0.wireOp",EDGE,"E440"),sQuery(id+"F0.wireOp",EDGE,"E441"),sQuery(id+"F0.wireOp",EDGE,"E442"),sQuery(id+"F0.wireOp",EDGE,"E443"),sQuery(id+"F0.wireOp",EDGE,"E444"),sQuery(id+"F0.wireOp",EDGE,"E445"),sQuery(id+"F0.wireOp",EDGE,"E446"),sQuery(id+"F0.wireOp",EDGE,"E447"),sQuery(id+"F0.wireOp",EDGE,"E448"),sQuery(id+"F0.wireOp",EDGE,"E449"),sQuery(id+"F0.wireOp",EDGE,"E450"),sQuery(id+"F0.wireOp",EDGE,"E451"),sQuery(id+"F0.wireOp",EDGE,"E452"),sQuery(id+"F0.wireOp",EDGE,"E453"),sQuery(id+"F0.wireOp",EDGE,"E454"),sQuery(id+"F0.wireOp",EDGE,"E455"),sQuery(id+"F0.wireOp",EDGE,"E456"),sQuery(id+"F0.wireOp",EDGE,"E457"),sQuery(id+"F0.wireOp",EDGE,"E458"),sQuery(id+"F0.wireOp",EDGE,"E459"),sQuery(id+"F0.wireOp",EDGE,"E460"),sQuery(id+"F0.wireOp",EDGE,"E461"),sQuery(id+"F0.wireOp",EDGE,"E462"),sQuery(id+"F0.wireOp",EDGE,"E463"),sQuery(id+"F0.wireOp",EDGE,"E464"),sQuery(id+"F0.wireOp",EDGE,"E465"),sQuery(id+"F0.wireOp",EDGE,"E466"),sQuery(id+"F0.wireOp",EDGE,"E467"),sQuery(id+"F0.wireOp",EDGE,"E468"),sQuery(id+"F0.wireOp",EDGE,"E469"),sQuery(id+"F0.wireOp",EDGE,"E470"),sQuery(id+"F0.wireOp",EDGE,"E471"),sQuery(id+"F0.wireOp",EDGE,"E472"),sQuery(id+"F0.wireOp",EDGE,"E473"),sQuery(id+"F0.wireOp",EDGE,"E474"),sQuery(id+"F0.wireOp",EDGE,"E475"),sQuery(id+"F0.wireOp",EDGE,"E476"),sQuery(id+"F0.wireOp",EDGE,"E477"),sQuery(id+"F0.wireOp",EDGE,"E478"),sQuery(id+"F0.wireOp",EDGE,"E479"),sQuery(id+"F0.wireOp",EDGE,"E480"),sQuery(id+"F0.wireOp",EDGE,"E481"),sQuery(id+"F0.wireOp",EDGE,"E482"),sQuery(id+"F0.wireOp",EDGE,"E483"),sQuery(id+"F0.wireOp",EDGE,"E484"),sQuery(id+"F0.wireOp",EDGE,"E485"),sQuery(id+"F0.wireOp",EDGE,"E486"),sQuery(id+"F0.wireOp",EDGE,"E487"),sQuery(id+"F0.wireOp",EDGE,"E488"),sQuery(id+"F0.wireOp",EDGE,"E489"),sQuery(id+"F0.wireOp",EDGE,"E490"),sQuery(id+"F0.wireOp",EDGE,"E491"),sQuery(id+"F0.wireOp",EDGE,"E492"),sQuery(id+"F0.wireOp",EDGE,"E493"),sQuery(id+"F0.wireOp",EDGE,"E494"),sQuery(id+"F0.wireOp",EDGE,"E495"),sQuery(id+"F0.wireOp",EDGE,"E496"),sQuery(id+"F0.wireOp",EDGE,"E497"),sQuery(id+"F0.wireOp",EDGE,"E498"),sQuery(id+"F0.wireOp",EDGE,"E499"),sQuery(id+"F0.wireOp",EDGE,"E500"),sQuery(id+"F0.wireOp",EDGE,"E501"),sQuery(id+"F0.wireOp",EDGE,"E502"),sQuery(id+"F0.wireOp",EDGE,"E503"),sQuery(id+"F0.wireOp",EDGE,"E504"),sQuery(id+"F0.wireOp",EDGE,"E505"),sQuery(id+"F0.wireOp",EDGE,"E506"),sQuery(id+"F0.wireOp",EDGE,"E507"),sQuery(id+"F0.wireOp",EDGE,"E508"),sQuery(id+"F0.wireOp",EDGE,"E509"),sQuery(id+"F0.wireOp",EDGE,"E510"),sQuery(id+"F0.wireOp",EDGE,"E511"),sQuery(id+"F0.wireOp",EDGE,"E512"),sQuery(id+"F0.wireOp",EDGE,"E513"),sQuery(id+"F0.wireOp",EDGE,"E514"),sQuery(id+"F0.wireOp",EDGE,"E515"),sQuery(id+"F0.wireOp",EDGE,"E516"),sQuery(id+"F0.wireOp",EDGE,"E517"),sQuery(id+"F0.wireOp",EDGE,"E518"),sQuery(id+"F0.wireOp",EDGE,"E519"),sQuery(id+"F0.wireOp",EDGE,"E520"),sQuery(id+"F0.wireOp",EDGE,"E521"),sQuery(id+"F0.wireOp",EDGE,"E522"),sQuery(id+"F0.wireOp",EDGE,"E523"),sQuery(id+"F0.wireOp",EDGE,"E524"),sQuery(id+"F0.wireOp",EDGE,"E525"),sQuery(id+"F0.wireOp",EDGE,"E526"),sQuery(id+"F0.wireOp",EDGE,"E527"),sQuery(id+"F0.wireOp",EDGE,"E528"),sQuery(id+"F0.wireOp",EDGE,"E529"),sQuery(id+"F0.wireOp",EDGE,"E530"),sQuery(id+"F0.wireOp",EDGE,"E531"),sQuery(id+"F0.wireOp",EDGE,"E532"),sQuery(id+"F0.wireOp",EDGE,"E533"),sQuery(id+"F0.wireOp",EDGE,"E534"),sQuery(id+"F0.wireOp",EDGE,"E535"),sQuery(id+"F0.wireOp",EDGE,"E536"),sQuery(id+"F0.wireOp",EDGE,"E537"),sQuery(id+"F0.wireOp",EDGE,"E538"),sQuery(id+"F0.wireOp",EDGE,"E539"),sQuery(id+"F0.wireOp",EDGE,"E540"),sQuery(id+"F0.wireOp",EDGE,"E541"),sQuery(id+"F0.wireOp",EDGE,"E542"),sQuery(id+"F0.wireOp",EDGE,"E543"),sQuery(id+"F0.wireOp",EDGE,"E544"),sQuery(id+"F0.wireOp",EDGE,"E545"),sQuery(id+"F0.wireOp",EDGE,"E546"),sQuery(id+"F0.wireOp",EDGE,"E547"),sQuery(id+"F0.wireOp",EDGE,"E548"),sQuery(id+"F0.wireOp",EDGE,"E549"),sQuery(id+"F0.wireOp",EDGE,"E550"),sQuery(id+"F0.wireOp",EDGE,"E551"),sQuery(id+"F0.wireOp",EDGE,"E552"),sQuery(id+"F0.wireOp",EDGE,"E553"),sQuery(id+"F0.wireOp",EDGE,"E554"),sQuery(id+"F0.wireOp",EDGE,"E555"),sQuery(id+"F0.wireOp",EDGE,"E556"),sQuery(id+"F0.wireOp",EDGE,"E557"),sQuery(id+"F0.wireOp",EDGE,"E558"),sQuery(id+"F0.wireOp",EDGE,"E559"),sQuery(id+"F0.wireOp",EDGE,"E560"),sQuery(id+"F0.wireOp",EDGE,"E561"),sQuery(id+"F0.wireOp",EDGE,"E562"),sQuery(id+"F0.wireOp",EDGE,"E563"),sQuery(id+"F0.wireOp",EDGE,"E564"),sQuery(id+"F0.wireOp",EDGE,"E565"),sQuery(id+"F0.wireOp",EDGE,"E566"),sQuery(id+"F0.wireOp",EDGE,"E567"),sQuery(id+"F0.wireOp",EDGE,"E568"),sQuery(id+"F0.wireOp",EDGE,"E569"),sQuery(id+"F0.wireOp",EDGE,"E570"),sQuery(id+"F0.wireOp",EDGE,"E571"),sQuery(id+"F0.wireOp",EDGE,"E572"),sQuery(id+"F0.wireOp",EDGE,"E573"),sQuery(id+"F0.wireOp",EDGE,"E574"),sQuery(id+"F0.wireOp",EDGE,"E575"),sQuery(id+"F0.wireOp",EDGE,"E576"),sQuery(id+"F0.wireOp",EDGE,"E577"),sQuery(id+"F0.wireOp",EDGE,"E578"),sQuery(id+"F0.wireOp",EDGE,"E579"),sQuery(id+"F0.wireOp",EDGE,"E580"),sQuery(id+"F0.wireOp",EDGE,"E581"),sQuery(id+"F0.wireOp",EDGE,"E582"),sQuery(id+"F0.wireOp",EDGE,"E583"),sQuery(id+"F0.wireOp",EDGE,"E584"),sQuery(id+"F0.wireOp",EDGE,"E585"),sQuery(id+"F0.wireOp",EDGE,"E586"),sQuery(id+"F0.wireOp",EDGE,"E587"),sQuery(id+"F0.wireOp",EDGE,"E588"),sQuery(id+"F0.wireOp",EDGE,"E589"),sQuery(id+"F0.wireOp",EDGE,"E590"),sQuery(id+"F0.wireOp",EDGE,"E591"),sQuery(id+"F0.wireOp",EDGE,"E592"),sQuery(id+"F0.wireOp",EDGE,"E593"),sQuery(id+"F0.wireOp",EDGE,"E594"),sQuery(id+"F0.wireOp",EDGE,"E595"),sQuery(id+"F0.wireOp",EDGE,"E596"),sQuery(id+"F0.wireOp",EDGE,"E597"),sQuery(id+"F0.wireOp",EDGE,"E598"),sQuery(id+"F0.wireOp",EDGE,"E599"),sQuery(id+"F0.wireOp",EDGE,"E600"),sQuery(id+"F0.wireOp",EDGE,"E601"),sQuery(id+"F0.wireOp",EDGE,"E602"),sQuery(id+"F0.wireOp",EDGE,"E603"),sQuery(id+"F0.wireOp",EDGE,"E604"),sQuery(id+"F0.wireOp",EDGE,"E605"),sQuery(id+"F0.wireOp",EDGE,"E606"),sQuery(id+"F0.wireOp",EDGE,"E607"),sQuery(id+"F0.wireOp",EDGE,"E608"),sQuery(id+"F0.wireOp",EDGE,"E609"),sQuery(id+"F0.wireOp",EDGE,"E610"),sQuery(id+"F0.wireOp",EDGE,"E611"),sQuery(id+"F0.wireOp",EDGE,"E612"),sQuery(id+"F0.wireOp",EDGE,"E613"),sQuery(id+"F0.wireOp",EDGE,"E614"),sQuery(id+"F0.wireOp",EDGE,"E615"),sQuery(id+"F0.wireOp",EDGE,"E616"),sQuery(id+"F0.wireOp",EDGE,"E617"),sQuery(id+"F0.wireOp",EDGE,"E618"),sQuery(id+"F0.wireOp",EDGE,"E619"),sQuery(id+"F0.wireOp",EDGE,"E620"),sQuery(id+"F0.wireOp",EDGE,"E621"),sQuery(id+"F0.wireOp",EDGE,"E622"),sQuery(id+"F0.wireOp",EDGE,"E623"),sQuery(id+"F0.wireOp",EDGE,"E624"),sQuery(id+"F0.wireOp",EDGE,"E625"),sQuery(id+"F0.wireOp",EDGE,"E626"),sQuery(id+"F0.wireOp",EDGE,"E627"),sQuery(id+"F0.wireOp",EDGE,"E628"),sQuery(id+"F0.wireOp",EDGE,"E629"),sQuery(id+"F0.wireOp",EDGE,"E630"),sQuery(id+"F0.wireOp",EDGE,"E631"),sQuery(id+"F0.wireOp",EDGE,"E632"),sQuery(id+"F0.wireOp",EDGE,"E633"),sQuery(id+"F0.wireOp",EDGE,"E634"),sQuery(id+"F0.wireOp",EDGE,"E635"),sQuery(id+"F0.wireOp",EDGE,"E636"),sQuery(id+"F0.wireOp",EDGE,"E637"),sQuery(id+"F0.wireOp",EDGE,"E638"),sQuery(id+"F0.wireOp",EDGE,"E639"),sQuery(id+"F0.wireOp",EDGE,"E640"),sQuery(id+"F0.wireOp",EDGE,"E641"),sQuery(id+"F0.wireOp",EDGE,"E642"),sQuery(id+"F0.wireOp",EDGE,"E643"),sQuery(id+"F0.wireOp",EDGE,"E644"),sQuery(id+"F0.wireOp",EDGE,"E645"),sQuery(id+"F0.wireOp",EDGE,"E646"),sQuery(id+"F0.wireOp",EDGE,"E647"),sQuery(id+"F0.wireOp",EDGE,"E648"),sQuery(id+"F0.wireOp",EDGE,"E649"),sQuery(id+"F0.wireOp",EDGE,"E650"),sQuery(id+"F0.wireOp",EDGE,"E651"),sQuery(id+"F0.wireOp",EDGE,"E652"),sQuery(id+"F0.wireOp",EDGE,"E653"),sQuery(id+"F0.wireOp",EDGE,"E654"),sQuery(id+"F0.wireOp",EDGE,"E655"),sQuery(id+"F0.wireOp",EDGE,"E656"),sQuery(id+"F0.wireOp",EDGE,"E657"),sQuery(id+"F0.wireOp",EDGE,"E658"),sQuery(id+"F0.wireOp",EDGE,"E659"),sQuery(id+"F0.wireOp",EDGE,"E660"),sQuery(id+"F0.wireOp",EDGE,"E661"),sQuery(id+"F0.wireOp",EDGE,"E662"),sQuery(id+"F0.wireOp",EDGE,"E663"),sQuery(id+"F0.wireOp",EDGE,"E664"),sQuery(id+"F0.wireOp",EDGE,"E665"),sQuery(id+"F0.wireOp",EDGE,"E666"),sQuery(id+"F0.wireOp",EDGE,"E667"),sQuery(id+"F0.wireOp",EDGE,"E668"),sQuery(id+"F0.wireOp",EDGE,"E669"),sQuery(id+"F0.wireOp",EDGE,"E670"),sQuery(id+"F0.wireOp",EDGE,"E671"),sQuery(id+"F0.wireOp",EDGE,"E672"),sQuery(id+"F0.wireOp",EDGE,"E673"),sQuery(id+"F0.wireOp",EDGE,"E674"),sQuery(id+"F0.wireOp",EDGE,"E675"),sQuery(id+"F0.wireOp",EDGE,"E676"),sQuery(id+"F0.wireOp",EDGE,"E677"),sQuery(id+"F0.wireOp",EDGE,"E678"),sQuery(id+"F0.wireOp",EDGE,"E679"),sQuery(id+"F0.wireOp",EDGE,"E680"),sQuery(id+"F0.wireOp",EDGE,"E681"),sQuery(id+"F0.wireOp",EDGE,"E682"),sQuery(id+"F0.wireOp",EDGE,"E683"),sQuery(id+"F0.wireOp",EDGE,"E684"),sQuery(id+"F0.wireOp",EDGE,"E685"),sQuery(id+"F0.wireOp",EDGE,"E686"),sQuery(id+"F0.wireOp",EDGE,"E687"),sQuery(id+"F0.wireOp",EDGE,"E688"),sQuery(id+"F0.wireOp",EDGE,"E689"),sQuery(id+"F0.wireOp",EDGE,"E690"),sQuery(id+"F0.wireOp",EDGE,"E691"),sQuery(id+"F0.wireOp",EDGE,"E692"),sQuery(id+"F0.wireOp",EDGE,"E693"),sQuery(id+"F0.wireOp",EDGE,"E694"),sQuery(id+"F0.wireOp",EDGE,"E695"),sQuery(id+"F0.wireOp",EDGE,"E696"),sQuery(id+"F0.wireOp",EDGE,"E697"),sQuery(id+"F0.wireOp",EDGE,"E698"),sQuery(id+"F0.wireOp",EDGE,"E699"),sQuery(id+"F0.wireOp",EDGE,"E700"),sQuery(id+"F0.wireOp",EDGE,"E701"),sQuery(id+"F0.wireOp",EDGE,"E702"),sQuery(id+"F0.wireOp",EDGE,"E703"),sQuery(id+"F0.wireOp",EDGE,"E704"),sQuery(id+"F0.wireOp",EDGE,"E705"),sQuery(id+"F0.wireOp",EDGE,"E706"),sQuery(id+"F0.wireOp",EDGE,"E707"),sQuery(id+"F0.wireOp",EDGE,"E708"),sQuery(id+"F0.wireOp",EDGE,"E709"),sQuery(id+"F0.wireOp",EDGE,"E710"),sQuery(id+"F0.wireOp",EDGE,"E711"),sQuery(id+"F0.wireOp",EDGE,"E712"),sQuery(id+"F0.wireOp",EDGE,"E713"),sQuery(id+"F0.wireOp",EDGE,"E714"),sQuery(id+"F0.wireOp",EDGE,"E715"),sQuery(id+"F0.wireOp",EDGE,"E716"),sQuery(id+"F0.wireOp",EDGE,"E717"),sQuery(id+"F0.wireOp",EDGE,"E718"),sQuery(id+"F0.wireOp",EDGE,"E719"),sQuery(id+"F0.wireOp",EDGE,"E720"),sQuery(id+"F0.wireOp",EDGE,"E721"),sQuery(id+"F0.wireOp",EDGE,"E722"),sQuery(id+"F0.wireOp",EDGE,"E723"),sQuery(id+"F0.wireOp",EDGE,"E724"),sQuery(id+"F0.wireOp",EDGE,"E725"),sQuery(id+"F0.wireOp",EDGE,"E726"),sQuery(id+"F0.wireOp",EDGE,"E727"),sQuery(id+"F0.wireOp",EDGE,"E728"),sQuery(id+"F0.wireOp",EDGE,"E729"),sQuery(id+"F0.wireOp",EDGE,"E730"),sQuery(id+"F0.wireOp",EDGE,"E731"),sQuery(id+"F0.wireOp",EDGE,"E732"),sQuery(id+"F0.wireOp",EDGE,"E733"),sQuery(id+"F0.wireOp",EDGE,"E734"),sQuery(id+"F0.wireOp",EDGE,"E735"),sQuery(id+"F0.wireOp",EDGE,"E736"),sQuery(id+"F0.wireOp",EDGE,"E737"),sQuery(id+"F0.wireOp",EDGE,"E738"),sQuery(id+"F0.wireOp",EDGE,"E739"),sQuery(id+"F0.wireOp",EDGE,"E740"),sQuery(id+"F0.wireOp",EDGE,"E741"),sQuery(id+"F0.wireOp",EDGE,"E742"),sQuery(id+"F0.wireOp",EDGE,"E743"),sQuery(id+"F0.wireOp",EDGE,"E744"),sQuery(id+"F0.wireOp",EDGE,"E745"),sQuery(id+"F0.wireOp",EDGE,"E746"),sQuery(id+"F0.wireOp",EDGE,"E747"),sQuery(id+"F0.wireOp",EDGE,"E748"),sQuery(id+"F0.wireOp",EDGE,"E749"),sQuery(id+"F0.wireOp",EDGE,"E750"),sQuery(id+"F0.wireOp",EDGE,"E751"),sQuery(id+"F0.wireOp",EDGE,"E752"),sQuery(id+"F0.wireOp",EDGE,"E753"),sQuery(id+"F0.wireOp",EDGE,"E754"),sQuery(id+"F0.wireOp",EDGE,"E755"),sQuery(id+"F0.wireOp",EDGE,"E756"),sQuery(id+"F0.wireOp",EDGE,"E757"),sQuery(id+"F0.wireOp",EDGE,"E758"),sQuery(id+"F0.wireOp",EDGE,"E759"),sQuery(id+"F0.wireOp",EDGE,"E760"),sQuery(id+"F0.wireOp",EDGE,"E761"),sQuery(id+"F0.wireOp",EDGE,"E762"),sQuery(id+"F0.wireOp",EDGE,"E763"),sQuery(id+"F0.wireOp",EDGE,"E764"),sQuery(id+"F0.wireOp",EDGE,"E765"),sQuery(id+"F0.wireOp",EDGE,"E766"),sQuery(id+"F0.wireOp",EDGE,"E767"),sQuery(id+"F0.wireOp",EDGE,"E768"),sQuery(id+"F0.wireOp",EDGE,"E769"),sQuery(id+"F0.wireOp",EDGE,"E770"),sQuery(id+"F0.wireOp",EDGE,"E771"),sQuery(id+"F0.wireOp",EDGE,"E772"),sQuery(id+"F0.wireOp",EDGE,"E773"),sQuery(id+"F0.wireOp",EDGE,"E774"),sQuery(id+"F0.wireOp",EDGE,"E775"),sQuery(id+"F0.wireOp",EDGE,"E776"),sQuery(id+"F0.wireOp",EDGE,"E777"),sQuery(id+"F0.wireOp",EDGE,"E778"),sQuery(id+"F0.wireOp",EDGE,"E779"),sQuery(id+"F0.wireOp",EDGE,"E780"),sQuery(id+"F0.wireOp",EDGE,"E781"),sQuery(id+"F0.wireOp",EDGE,"E782"),sQuery(id+"F0.wireOp",EDGE,"E783"),sQuery(id+"F0.wireOp",EDGE,"E784"),sQuery(id+"F0.wireOp",EDGE,"E785"),sQuery(id+"F0.wireOp",EDGE,"E786"),sQuery(id+"F0.wireOp",EDGE,"E787"),sQuery(id+"F0.wireOp",EDGE,"E788"),sQuery(id+"F0.wireOp",EDGE,"E789"),sQuery(id+"F0.wireOp",EDGE,"E790"),sQuery(id+"F0.wireOp",EDGE,"E791"),sQuery(id+"F0.wireOp",EDGE,"E792"),sQuery(id+"F0.wireOp",EDGE,"E793"),sQuery(id+"F0.wireOp",EDGE,"E794"),sQuery(id+"F0.wireOp",EDGE,"E795"),sQuery(id+"F0.wireOp",EDGE,"E796"),sQuery(id+"F0.wireOp",EDGE,"E797"),sQuery(id+"F0.wireOp",EDGE,"E798"),sQuery(id+"F0.wireOp",EDGE,"E799"),sQuery(id+"F0.wireOp",EDGE,"E800"),sQuery(id+"F0.wireOp",EDGE,"E801"),sQuery(id+"F0.wireOp",EDGE,"E802"),sQuery(id+"F0.wireOp",EDGE,"E803"),sQuery(id+"F0.wireOp",EDGE,"E804"),sQuery(id+"F0.wireOp",EDGE,"E805"),sQuery(id+"F0.wireOp",EDGE,"E806"),sQuery(id+"F0.wireOp",EDGE,"E807"),sQuery(id+"F0.wireOp",EDGE,"E808"),sQuery(id+"F0.wireOp",EDGE,"E809"),sQuery(id+"F0.wireOp",EDGE,"E810"),sQuery(id+"F0.wireOp",EDGE,"E811"),sQuery(id+"F0.wireOp",EDGE,"E812"),sQuery(id+"F0.wireOp",EDGE,"E813"),sQuery(id+"F0.wireOp",EDGE,"E814"),sQuery(id+"F0.wireOp",EDGE,"E815"),sQuery(id+"F0.wireOp",EDGE,"E816"),sQuery(id+"F0.wireOp",EDGE,"E817"),sQuery(id+"F0.wireOp",EDGE,"E818"),sQuery(id+"F0.wireOp",EDGE,"E819"),sQuery(id+"F0.wireOp",EDGE,"E820"),sQuery(id+"F0.wireOp",EDGE,"E821"),sQuery(id+"F0.wireOp",EDGE,"E822"),sQuery(id+"F0.wireOp",EDGE,"E823"),sQuery(id+"F0.wireOp",EDGE,"E824"),sQuery(id+"F0.wireOp",EDGE,"E825"),sQuery(id+"F0.wireOp",EDGE,"E826"),sQuery(id+"F0.wireOp",EDGE,"E827"),sQuery(id+"F0.wireOp",EDGE,"E828"),sQuery(id+"F0.wireOp",EDGE,"E829"),sQuery(id+"F0.wireOp",EDGE,"E830"),sQuery(id+"F0.wireOp",EDGE,"E831"),sQuery(id+"F0.wireOp",EDGE,"E832"),sQuery(id+"F0.wireOp",EDGE,"E833"),sQuery(id+"F0.wireOp",EDGE,"E834"),sQuery(id+"F0.wireOp",EDGE,"E835"),sQuery(id+"F0.wireOp",EDGE,"E836"),sQuery(id+"F0.wireOp",EDGE,"E837"),sQuery(id+"F0.wireOp",EDGE,"E838"),sQuery(id+"F0.wireOp",EDGE,"E839"),sQuery(id+"F0.wireOp",EDGE,"E840"),sQuery(id+"F0.wireOp",EDGE,"E841"),sQuery(id+"F0.wireOp",EDGE,"E842"),sQuery(id+"F0.wireOp",EDGE,"E843"),sQuery(id+"F0.wireOp",EDGE,"E844"),sQuery(id+"F0.wireOp",EDGE,"E845"),sQuery(id+"F0.wireOp",EDGE,"E846"),sQuery(id+"F0.wireOp",EDGE,"E847"),sQuery(id+"F0.wireOp",EDGE,"E848"),sQuery(id+"F0.wireOp",EDGE,"E849"),sQuery(id+"F0.wireOp",EDGE,"E850"),sQuery(id+"F0.wireOp",EDGE,"E851"),sQuery(id+"F0.wireOp",EDGE,"E852"),sQuery(id+"F0.wireOp",EDGE,"E853"),sQuery(id+"F0.wireOp",EDGE,"E854"),sQuery(id+"F0.wireOp",EDGE,"E855"),sQuery(id+"F0.wireOp",EDGE,"E856"),sQuery(id+"F0.wireOp",EDGE,"E857"),sQuery(id+"F0.wireOp",EDGE,"E858"),sQuery(id+"F0.wireOp",EDGE,"E859"),sQuery(id+"F0.wireOp",EDGE,"E860"),sQuery(id+"F0.wireOp",EDGE,"E861"),sQuery(id+"F0.wireOp",EDGE,"E862"),sQuery(id+"F0.wireOp",EDGE,"E863"),sQuery(id+"F0.wireOp",EDGE,"E864"),sQuery(id+"F0.wireOp",EDGE,"E865"),sQuery(id+"F0.wireOp",EDGE,"E866"),sQuery(id+"F0.wireOp",EDGE,"E867"),sQuery(id+"F0.wireOp",EDGE,"E868"),sQuery(id+"F0.wireOp",EDGE,"E869"),sQuery(id+"F0.wireOp",EDGE,"E870"),sQuery(id+"F0.wireOp",EDGE,"E871"),sQuery(id+"F0.wireOp",EDGE,"E872"),sQuery(id+"F0.wireOp",EDGE,"E873"),sQuery(id+"F0.wireOp",EDGE,"E874"),sQuery(id+"F0.wireOp",EDGE,"E875"),sQuery(id+"F0.wireOp",EDGE,"E876"),sQuery(id+"F0.wireOp",EDGE,"E877"),sQuery(id+"F0.wireOp",EDGE,"E878"),sQuery(id+"F0.wireOp",EDGE,"E879"),sQuery(id+"F0.wireOp",EDGE,"E880"),sQuery(id+"F0.wireOp",EDGE,"E881"),sQuery(id+"F0.wireOp",EDGE,"E882"),sQuery(id+"F0.wireOp",EDGE,"E883"),sQuery(id+"F0.wireOp",EDGE,"E884"),sQuery(id+"F0.wireOp",EDGE,"E885"),sQuery(id+"F0.wireOp",EDGE,"E886"),sQuery(id+"F0.wireOp",EDGE,"E887"),sQuery(id+"F0.wireOp",EDGE,"E888"),sQuery(id+"F0.wireOp",EDGE,"E889"),sQuery(id+"F0.wireOp",EDGE,"E890"),sQuery(id+"F0.wireOp",EDGE,"E891"),sQuery(id+"F0.wireOp",EDGE,"E892"),sQuery(id+"F0.wireOp",EDGE,"E893"),sQuery(id+"F0.wireOp",EDGE,"E894"),sQuery(id+"F0.wireOp",EDGE,"E895"),sQuery(id+"F0.wireOp",EDGE,"E896"),sQuery(id+"F0.wireOp",EDGE,"E897"),sQuery(id+"F0.wireOp",EDGE,"E898"),sQuery(id+"F0.wireOp",EDGE,"E899"),sQuery(id+"F0.wireOp",EDGE,"E900"),sQuery(id+"F0.wireOp",EDGE,"E901"),sQuery(id+"F0.wireOp",EDGE,"E902"),sQuery(id+"F0.wireOp",EDGE,"E903"),sQuery(id+"F0.wireOp",EDGE,"E904"),sQuery(id+"F0.wireOp",EDGE,"E905"),sQuery(id+"F0.wireOp",EDGE,"E906"),sQuery(id+"F0.wireOp",EDGE,"E907"),sQuery(id+"F0.wireOp",EDGE,"E908"),sQuery(id+"F0.wireOp",EDGE,"E909"),sQuery(id+"F0.wireOp",EDGE,"E910"),sQuery(id+"F0.wireOp",EDGE,"E911"),sQuery(id+"F0.wireOp",EDGE,"E912"),sQuery(id+"F0.wireOp",EDGE,"E913"),sQuery(id+"F0.wireOp",EDGE,"E914"),sQuery(id+"F0.wireOp",EDGE,"E915"),sQuery(id+"F0.wireOp",EDGE,"E916"),sQuery(id+"F0.wireOp",EDGE,"E917"),sQuery(id+"F0.wireOp",EDGE,"E918"),sQuery(id+"F0.wireOp",EDGE,"E919"),sQuery(id+"F0.wireOp",EDGE,"E920"),sQuery(id+"F0.wireOp",EDGE,"E921"),sQuery(id+"F0.wireOp",EDGE,"E922"),sQuery(id+"F0.wireOp",EDGE,"E923"),sQuery(id+"F0.wireOp",EDGE,"E924"),sQuery(id+"F0.wireOp",EDGE,"E925"),sQuery(id+"F0.wireOp",EDGE,"E926"),sQuery(id+"F0.wireOp",EDGE,"E927"),sQuery(id+"F0.wireOp",EDGE,"E928"),sQuery(id+"F0.wireOp",EDGE,"E929"),sQuery(id+"F0.wireOp",EDGE,"E930"),sQuery(id+"F0.wireOp",EDGE,"E931"),sQuery(id+"F0.wireOp",EDGE,"E932"),sQuery(id+"F0.wireOp",EDGE,"E933"),sQuery(id+"F0.wireOp",EDGE,"E934"),sQuery(id+"F0.wireOp",EDGE,"E935"),sQuery(id+"F0.wireOp",EDGE,"E936"),sQuery(id+"F0.wireOp",EDGE,"E937"),sQuery(id+"F0.wireOp",EDGE,"E938"),sQuery(id+"F0.wireOp",EDGE,"E939"),sQuery(id+"F0.wireOp",EDGE,"E940"),sQuery(id+"F0.wireOp",EDGE,"E941"),sQuery(id+"F0.wireOp",EDGE,"E942"),sQuery(id+"F0.wireOp",EDGE,"E943"),sQuery(id+"F0.wireOp",EDGE,"E944"),sQuery(id+"F0.wireOp",EDGE,"E945"),sQuery(id+"F0.wireOp",EDGE,"E946"),sQuery(id+"F0.wireOp",EDGE,"E947"),sQuery(id+"F0.wireOp",EDGE,"E948"),sQuery(id+"F0.wireOp",EDGE,"E949"),sQuery(id+"F0.wireOp",EDGE,"E950"),sQuery(id+"F0.wireOp",EDGE,"E951"),sQuery(id+"F0.wireOp",EDGE,"E952"),sQuery(id+"F0.wireOp",EDGE,"E953"),sQuery(id+"F0.wireOp",EDGE,"E954"),sQuery(id+"F0.wireOp",EDGE,"E955"),sQuery(id+"F0.wireOp",EDGE,"E956"),sQuery(id+"F0.wireOp",EDGE,"E957"),sQuery(id+"F0.wireOp",EDGE,"E958"),sQuery(id+"F0.wireOp",EDGE,"E959"),sQuery(id+"F0.wireOp",EDGE,"E960"),sQuery(id+"F0.wireOp",EDGE,"E961"),sQuery(id+"F0.wireOp",EDGE,"E962"),sQuery(id+"F0.wireOp",EDGE,"E963"),sQuery(id+"F0.wireOp",EDGE,"E964"),sQuery(id+"F0.wireOp",EDGE,"E965"),sQuery(id+"F0.wireOp",EDGE,"E966"),sQuery(id+"F0.wireOp",EDGE,"E967"),sQuery(id+"F0.wireOp",EDGE,"E968"),sQuery(id+"F0.wireOp",EDGE,"E969"),sQuery(id+"F0.wireOp",EDGE,"E970"),sQuery(id+"F0.wireOp",EDGE,"E971"),sQuery(id+"F0.wireOp",EDGE,"E972"),sQuery(id+"F0.wireOp",EDGE,"E973"),sQuery(id+"F0.wireOp",EDGE,"E974"),sQuery(id+"F0.wireOp",EDGE,"E975"),sQuery(id+"F0.wireOp",EDGE,"E976"),sQuery(id+"F0.wireOp",EDGE,"E977"),sQuery(id+"F0.wireOp",EDGE,"E978"),sQuery(id+"F0.wireOp",EDGE,"E979"),sQuery(id+"F0.wireOp",EDGE,"E980"),sQuery(id+"F0.wireOp",EDGE,"E981"),sQuery(id+"F0.wireOp",EDGE,"E982"),sQuery(id+"F0.wireOp",EDGE,"E983"),sQuery(id+"F0.wireOp",EDGE,"E984"),sQuery(id+"F0.wireOp",EDGE,"E985"),sQuery(id+"F0.wireOp",EDGE,"E986"),sQuery(id+"F0.wireOp",EDGE,"E987"),sQuery(id+"F0.wireOp",EDGE,"E988"),sQuery(id+"F0.wireOp",EDGE,"E989"),sQuery(id+"F0.wireOp",EDGE,"E990"),sQuery(id+"F0.wireOp",EDGE,"E991"),sQuery(id+"F0.wireOp",EDGE,"E992"),sQuery(id+"F0.wireOp",EDGE,"E993"),sQuery(id+"F0.wireOp",EDGE,"E994"),sQuery(id+"F0.wireOp",EDGE,"E995"),sQuery(id+"F0.wireOp",EDGE,"E996"),sQuery(id+"F0.wireOp",EDGE,"E997"),sQuery(id+"F0.wireOp",EDGE,"E998"),sQuery(id+"F0.wireOp",EDGE,"E999"),sQuery(id+"F0.wireOp",EDGE,"E1000"),sQuery(id+"F0.wireOp",EDGE,"E1001"),sQuery(id+"F0.wireOp",EDGE,"E1002"),sQuery(id+"F0.wireOp",EDGE,"E1003"),sQuery(id+"F0.wireOp",EDGE,"E1004"),sQuery(id+"F0.wireOp",EDGE,"E1005"),sQuery(id+"F0.wireOp",EDGE,"E1006"),sQuery(id+"F0.wireOp",EDGE,"E1007"),sQuery(id+"F0.wireOp",EDGE,"E1008"),sQuery(id+"F0.wireOp",EDGE,"E1009"),sQuery(id+"F0.wireOp",EDGE,"E1010"),sQuery(id+"F0.wireOp",EDGE,"E1011"),sQuery(id+"F0.wireOp",EDGE,"E1012"),sQuery(id+"F0.wireOp",EDGE,"E1013"),sQuery(id+"F0.wireOp",EDGE,"E1014"),sQuery(id+"F0.wireOp",EDGE,"E1015"),sQuery(id+"F0.wireOp",EDGE,"E1016"),sQuery(id+"F0.wireOp",EDGE,"E1017"),sQuery(id+"F0.wireOp",EDGE,"E1018"),sQuery(id+"F0.wireOp",EDGE,"E1019"),sQuery(id+"F0.wireOp",EDGE,"E1020"),sQuery(id+"F0.wireOp",EDGE,"E1021"),sQuery(id+"F0.wireOp",EDGE,"E1022"),sQuery(id+"F0.wireOp",EDGE,"E1023"),sQuery(id+"F0.wireOp",EDGE,"E1024"),sQuery(id+"F0.wireOp",EDGE,"E1025"),sQuery(id+"F0.wireOp",EDGE,"E1026"),sQuery(id+"F0.wireOp",EDGE,"E1027"),sQuery(id+"F0.wireOp",EDGE,"E1028"),sQuery(id+"F0.wireOp",EDGE,"E1029"),sQuery(id+"F0.wireOp",EDGE,"E1030"),sQuery(id+"F0.wireOp",EDGE,"E1031"),sQuery(id+"F0.wireOp",EDGE,"E1032"),sQuery(id+"F0.wireOp",EDGE,"E1033"),sQuery(id+"F0.wireOp",EDGE,"E1034"),sQuery(id+"F0.wireOp",EDGE,"E1035"),sQuery(id+"F0.wireOp",EDGE,"E1036"),sQuery(id+"F0.wireOp",EDGE,"E1037"),sQuery(id+"F0.wireOp",EDGE,"E1038"),sQuery(id+"F0.wireOp",EDGE,"E1039"),sQuery(id+"F0.wireOp",EDGE,"E1040")])],"isStart":false})});
            var sketch = newSketch(context, id + "F3", { "sketchPlane" : qUnion([Q0])});
            skArc(sketch, "E1041", {"start": v(1, 1.12) * mm, "mid": v(-1.5, 0) * mm, "end": v(1, -1.12) * mm});
            skLineSegment(sketch, "E1042.0", {"start": v(1.25, 0.83) * mm, "end": v(1.25, 0.83) * mm});
            skPoint(sketch, "E1043.orphan", {"position": v(1.25, 1.65) * mm});
            skLineSegment(sketch, "E1044.0", {"start": v(1, 0) * mm, "end": v(1, -1.12) * mm});
            skLineSegment(sketch, "E1045", {"start": v(1, 0) * mm, "end": v(1, 1.12) * mm});
            skPoint(sketch, "E1046.start.orphan", {"position": v(1.25, 0.83) * mm});
            skPoint(sketch, "E1047.orphan", {"position": v(1.25, 0) * mm});
            skSolve(sketch);
        }
        {
            var Q0;
            Q0 = qSketchRegion(id + "F3", true);
            extrude(context, id + "F4", {"entities" : qUnion([Q0]), "operationType" : NewBodyOperationType.REMOVE, "oppositeDirection" : true, "depth" : 25 * mm});
        }
        {
            var Q0;
            Q0=makeQuery(id+"F2.boolean.opBoolean","COPY",FACE,{"derivedFrom":makeQuery(id+"F2.opExtrude","CAP_FACE",FACE,{"disambiguationData":[OSD([sQuery(id+"F0.wireOp",EDGE,"E0"),sQuery(id+"F0.wireOp",EDGE,"E1"),sQuery(id+"F0.wireOp",EDGE,"E2"),sQuery(id+"F0.wireOp",EDGE,"E3"),sQuery(id+"F0.wireOp",EDGE,"E4"),sQuery(id+"F0.wireOp",EDGE,"E5"),sQuery(id+"F0.wireOp",EDGE,"E6"),sQuery(id+"F0.wireOp",EDGE,"E7"),sQuery(id+"F0.wireOp",EDGE,"E8"),sQuery(id+"F0.wireOp",EDGE,"E9"),sQuery(id+"F0.wireOp",EDGE,"E10"),sQuery(id+"F0.wireOp",EDGE,"E11"),sQuery(id+"F0.wireOp",EDGE,"E12"),sQuery(id+"F0.wireOp",EDGE,"E13"),sQuery(id+"F0.wireOp",EDGE,"E14"),sQuery(id+"F0.wireOp",EDGE,"E15"),sQuery(id+"F0.wireOp",EDGE,"E16"),sQuery(id+"F0.wireOp",EDGE,"E17"),sQuery(id+"F0.wireOp",EDGE,"E18"),sQuery(id+"F0.wireOp",EDGE,"E19"),sQuery(id+"F0.wireOp",EDGE,"E20"),sQuery(id+"F0.wireOp",EDGE,"E21"),sQuery(id+"F0.wireOp",EDGE,"E22"),sQuery(id+"F0.wireOp",EDGE,"E23"),sQuery(id+"F0.wireOp",EDGE,"E24"),sQuery(id+"F0.wireOp",EDGE,"E25"),sQuery(id+"F0.wireOp",EDGE,"E26"),sQuery(id+"F0.wireOp",EDGE,"E27"),sQuery(id+"F0.wireOp",EDGE,"E28"),sQuery(id+"F0.wireOp",EDGE,"E29"),sQuery(id+"F0.wireOp",EDGE,"E30"),sQuery(id+"F0.wireOp",EDGE,"E31"),sQuery(id+"F0.wireOp",EDGE,"E32"),sQuery(id+"F0.wireOp",EDGE,"E33"),sQuery(id+"F0.wireOp",EDGE,"E34"),sQuery(id+"F0.wireOp",EDGE,"E35"),sQuery(id+"F0.wireOp",EDGE,"E36"),sQuery(id+"F0.wireOp",EDGE,"E37"),sQuery(id+"F0.wireOp",EDGE,"E38"),sQuery(id+"F0.wireOp",EDGE,"E39"),sQuery(id+"F0.wireOp",EDGE,"E40"),sQuery(id+"F0.wireOp",EDGE,"E41"),sQuery(id+"F0.wireOp",EDGE,"E42"),sQuery(id+"F0.wireOp",EDGE,"E43"),sQuery(id+"F0.wireOp",EDGE,"E44"),sQuery(id+"F0.wireOp",EDGE,"E45"),sQuery(id+"F0.wireOp",EDGE,"E46"),sQuery(id+"F0.wireOp",EDGE,"E47"),sQuery(id+"F0.wireOp",EDGE,"E48"),sQuery(id+"F0.wireOp",EDGE,"E49"),sQuery(id+"F0.wireOp",EDGE,"E50"),sQuery(id+"F0.wireOp",EDGE,"E51"),sQuery(id+"F0.wireOp",EDGE,"E52"),sQuery(id+"F0.wireOp",EDGE,"E53"),sQuery(id+"F0.wireOp",EDGE,"E54"),sQuery(id+"F0.wireOp",EDGE,"E55"),sQuery(id+"F0.wireOp",EDGE,"E56"),sQuery(id+"F0.wireOp",EDGE,"E57"),sQuery(id+"F0.wireOp",EDGE,"E58"),sQuery(id+"F0.wireOp",EDGE,"E59"),sQuery(id+"F0.wireOp",EDGE,"E60"),sQuery(id+"F0.wireOp",EDGE,"E61"),sQuery(id+"F0.wireOp",EDGE,"E62"),sQuery(id+"F0.wireOp",EDGE,"E63"),sQuery(id+"F0.wireOp",EDGE,"E64"),sQuery(id+"F0.wireOp",EDGE,"E65"),sQuery(id+"F0.wireOp",EDGE,"E66"),sQuery(id+"F0.wireOp",EDGE,"E67"),sQuery(id+"F0.wireOp",EDGE,"E68"),sQuery(id+"F0.wireOp",EDGE,"E69"),sQuery(id+"F0.wireOp",EDGE,"E70"),sQuery(id+"F0.wireOp",EDGE,"E71"),sQuery(id+"F0.wireOp",EDGE,"E72"),sQuery(id+"F0.wireOp",EDGE,"E73"),sQuery(id+"F0.wireOp",EDGE,"E74"),sQuery(id+"F0.wireOp",EDGE,"E75"),sQuery(id+"F0.wireOp",EDGE,"E76"),sQuery(id+"F0.wireOp",EDGE,"E77"),sQuery(id+"F0.wireOp",EDGE,"E78"),sQuery(id+"F0.wireOp",EDGE,"E79"),sQuery(id+"F0.wireOp",EDGE,"E80"),sQuery(id+"F0.wireOp",EDGE,"E81"),sQuery(id+"F0.wireOp",EDGE,"E82"),sQuery(id+"F0.wireOp",EDGE,"E83"),sQuery(id+"F0.wireOp",EDGE,"E84"),sQuery(id+"F0.wireOp",EDGE,"E85"),sQuery(id+"F0.wireOp",EDGE,"E86"),sQuery(id+"F0.wireOp",EDGE,"E87"),sQuery(id+"F0.wireOp",EDGE,"E88"),sQuery(id+"F0.wireOp",EDGE,"E89"),sQuery(id+"F0.wireOp",EDGE,"E90"),sQuery(id+"F0.wireOp",EDGE,"E91"),sQuery(id+"F0.wireOp",EDGE,"E92"),sQuery(id+"F0.wireOp",EDGE,"E93"),sQuery(id+"F0.wireOp",EDGE,"E94"),sQuery(id+"F0.wireOp",EDGE,"E95"),sQuery(id+"F0.wireOp",EDGE,"E96"),sQuery(id+"F0.wireOp",EDGE,"E97"),sQuery(id+"F0.wireOp",EDGE,"E98"),sQuery(id+"F0.wireOp",EDGE,"E99"),sQuery(id+"F0.wireOp",EDGE,"E100"),sQuery(id+"F0.wireOp",EDGE,"E101"),sQuery(id+"F0.wireOp",EDGE,"E102"),sQuery(id+"F0.wireOp",EDGE,"E103"),sQuery(id+"F0.wireOp",EDGE,"E104"),sQuery(id+"F0.wireOp",EDGE,"E105"),sQuery(id+"F0.wireOp",EDGE,"E106"),sQuery(id+"F0.wireOp",EDGE,"E107"),sQuery(id+"F0.wireOp",EDGE,"E108"),sQuery(id+"F0.wireOp",EDGE,"E109"),sQuery(id+"F0.wireOp",EDGE,"E110"),sQuery(id+"F0.wireOp",EDGE,"E111"),sQuery(id+"F0.wireOp",EDGE,"E112"),sQuery(id+"F0.wireOp",EDGE,"E113"),sQuery(id+"F0.wireOp",EDGE,"E114"),sQuery(id+"F0.wireOp",EDGE,"E115"),sQuery(id+"F0.wireOp",EDGE,"E116"),sQuery(id+"F0.wireOp",EDGE,"E117"),sQuery(id+"F0.wireOp",EDGE,"E118"),sQuery(id+"F0.wireOp",EDGE,"E119"),sQuery(id+"F0.wireOp",EDGE,"E120"),sQuery(id+"F0.wireOp",EDGE,"E121"),sQuery(id+"F0.wireOp",EDGE,"E122"),sQuery(id+"F0.wireOp",EDGE,"E123"),sQuery(id+"F0.wireOp",EDGE,"E124"),sQuery(id+"F0.wireOp",EDGE,"E125"),sQuery(id+"F0.wireOp",EDGE,"E126"),sQuery(id+"F0.wireOp",EDGE,"E127"),sQuery(id+"F0.wireOp",EDGE,"E128"),sQuery(id+"F0.wireOp",EDGE,"E129"),sQuery(id+"F0.wireOp",EDGE,"E130"),sQuery(id+"F0.wireOp",EDGE,"E131"),sQuery(id+"F0.wireOp",EDGE,"E132"),sQuery(id+"F0.wireOp",EDGE,"E133"),sQuery(id+"F0.wireOp",EDGE,"E134"),sQuery(id+"F0.wireOp",EDGE,"E135"),sQuery(id+"F0.wireOp",EDGE,"E136"),sQuery(id+"F0.wireOp",EDGE,"E137"),sQuery(id+"F0.wireOp",EDGE,"E138"),sQuery(id+"F0.wireOp",EDGE,"E139"),sQuery(id+"F0.wireOp",EDGE,"E140"),sQuery(id+"F0.wireOp",EDGE,"E141"),sQuery(id+"F0.wireOp",EDGE,"E142"),sQuery(id+"F0.wireOp",EDGE,"E143"),sQuery(id+"F0.wireOp",EDGE,"E144"),sQuery(id+"F0.wireOp",EDGE,"E145"),sQuery(id+"F0.wireOp",EDGE,"E146"),sQuery(id+"F0.wireOp",EDGE,"E147"),sQuery(id+"F0.wireOp",EDGE,"E148"),sQuery(id+"F0.wireOp",EDGE,"E149"),sQuery(id+"F0.wireOp",EDGE,"E150"),sQuery(id+"F0.wireOp",EDGE,"E151"),sQuery(id+"F0.wireOp",EDGE,"E152"),sQuery(id+"F0.wireOp",EDGE,"E153"),sQuery(id+"F0.wireOp",EDGE,"E154"),sQuery(id+"F0.wireOp",EDGE,"E155"),sQuery(id+"F0.wireOp",EDGE,"E156"),sQuery(id+"F0.wireOp",EDGE,"E157"),sQuery(id+"F0.wireOp",EDGE,"E158"),sQuery(id+"F0.wireOp",EDGE,"E159"),sQuery(id+"F0.wireOp",EDGE,"E160"),sQuery(id+"F0.wireOp",EDGE,"E161"),sQuery(id+"F0.wireOp",EDGE,"E162"),sQuery(id+"F0.wireOp",EDGE,"E163"),sQuery(id+"F0.wireOp",EDGE,"E164"),sQuery(id+"F0.wireOp",EDGE,"E165"),sQuery(id+"F0.wireOp",EDGE,"E166"),sQuery(id+"F0.wireOp",EDGE,"E167"),sQuery(id+"F0.wireOp",EDGE,"E168"),sQuery(id+"F0.wireOp",EDGE,"E169"),sQuery(id+"F0.wireOp",EDGE,"E170"),sQuery(id+"F0.wireOp",EDGE,"E171"),sQuery(id+"F0.wireOp",EDGE,"E172"),sQuery(id+"F0.wireOp",EDGE,"E173"),sQuery(id+"F0.wireOp",EDGE,"E174"),sQuery(id+"F0.wireOp",EDGE,"E175"),sQuery(id+"F0.wireOp",EDGE,"E176"),sQuery(id+"F0.wireOp",EDGE,"E177"),sQuery(id+"F0.wireOp",EDGE,"E178"),sQuery(id+"F0.wireOp",EDGE,"E179"),sQuery(id+"F0.wireOp",EDGE,"E180"),sQuery(id+"F0.wireOp",EDGE,"E181"),sQuery(id+"F0.wireOp",EDGE,"E182"),sQuery(id+"F0.wireOp",EDGE,"E183"),sQuery(id+"F0.wireOp",EDGE,"E184"),sQuery(id+"F0.wireOp",EDGE,"E185"),sQuery(id+"F0.wireOp",EDGE,"E186"),sQuery(id+"F0.wireOp",EDGE,"E187"),sQuery(id+"F0.wireOp",EDGE,"E188"),sQuery(id+"F0.wireOp",EDGE,"E189"),sQuery(id+"F0.wireOp",EDGE,"E190"),sQuery(id+"F0.wireOp",EDGE,"E191"),sQuery(id+"F0.wireOp",EDGE,"E192"),sQuery(id+"F0.wireOp",EDGE,"E193"),sQuery(id+"F0.wireOp",EDGE,"E194"),sQuery(id+"F0.wireOp",EDGE,"E195"),sQuery(id+"F0.wireOp",EDGE,"E196"),sQuery(id+"F0.wireOp",EDGE,"E197"),sQuery(id+"F0.wireOp",EDGE,"E198"),sQuery(id+"F0.wireOp",EDGE,"E199"),sQuery(id+"F0.wireOp",EDGE,"E200"),sQuery(id+"F0.wireOp",EDGE,"E201"),sQuery(id+"F0.wireOp",EDGE,"E202"),sQuery(id+"F0.wireOp",EDGE,"E203"),sQuery(id+"F0.wireOp",EDGE,"E204"),sQuery(id+"F0.wireOp",EDGE,"E205"),sQuery(id+"F0.wireOp",EDGE,"E206"),sQuery(id+"F0.wireOp",EDGE,"E207"),sQuery(id+"F0.wireOp",EDGE,"E208"),sQuery(id+"F0.wireOp",EDGE,"E209"),sQuery(id+"F0.wireOp",EDGE,"E210"),sQuery(id+"F0.wireOp",EDGE,"E211"),sQuery(id+"F0.wireOp",EDGE,"E212"),sQuery(id+"F0.wireOp",EDGE,"E213"),sQuery(id+"F0.wireOp",EDGE,"E214"),sQuery(id+"F0.wireOp",EDGE,"E215"),sQuery(id+"F0.wireOp",EDGE,"E216"),sQuery(id+"F0.wireOp",EDGE,"E217"),sQuery(id+"F0.wireOp",EDGE,"E218"),sQuery(id+"F0.wireOp",EDGE,"E219"),sQuery(id+"F0.wireOp",EDGE,"E220"),sQuery(id+"F0.wireOp",EDGE,"E221"),sQuery(id+"F0.wireOp",EDGE,"E222"),sQuery(id+"F0.wireOp",EDGE,"E223"),sQuery(id+"F0.wireOp",EDGE,"E224"),sQuery(id+"F0.wireOp",EDGE,"E225"),sQuery(id+"F0.wireOp",EDGE,"E226"),sQuery(id+"F0.wireOp",EDGE,"E227"),sQuery(id+"F0.wireOp",EDGE,"E228"),sQuery(id+"F0.wireOp",EDGE,"E229"),sQuery(id+"F0.wireOp",EDGE,"E230"),sQuery(id+"F0.wireOp",EDGE,"E231"),sQuery(id+"F0.wireOp",EDGE,"E232"),sQuery(id+"F0.wireOp",EDGE,"E233"),sQuery(id+"F0.wireOp",EDGE,"E234"),sQuery(id+"F0.wireOp",EDGE,"E235"),sQuery(id+"F0.wireOp",EDGE,"E236"),sQuery(id+"F0.wireOp",EDGE,"E237"),sQuery(id+"F0.wireOp",EDGE,"E238"),sQuery(id+"F0.wireOp",EDGE,"E239"),sQuery(id+"F0.wireOp",EDGE,"E240"),sQuery(id+"F0.wireOp",EDGE,"E241"),sQuery(id+"F0.wireOp",EDGE,"E242"),sQuery(id+"F0.wireOp",EDGE,"E243"),sQuery(id+"F0.wireOp",EDGE,"E244"),sQuery(id+"F0.wireOp",EDGE,"E245"),sQuery(id+"F0.wireOp",EDGE,"E246"),sQuery(id+"F0.wireOp",EDGE,"E247"),sQuery(id+"F0.wireOp",EDGE,"E248"),sQuery(id+"F0.wireOp",EDGE,"E249"),sQuery(id+"F0.wireOp",EDGE,"E250"),sQuery(id+"F0.wireOp",EDGE,"E251"),sQuery(id+"F0.wireOp",EDGE,"E252"),sQuery(id+"F0.wireOp",EDGE,"E253"),sQuery(id+"F0.wireOp",EDGE,"E254"),sQuery(id+"F0.wireOp",EDGE,"E255"),sQuery(id+"F0.wireOp",EDGE,"E256"),sQuery(id+"F0.wireOp",EDGE,"E257"),sQuery(id+"F0.wireOp",EDGE,"E258"),sQuery(id+"F0.wireOp",EDGE,"E259"),sQuery(id+"F0.wireOp",EDGE,"E260"),sQuery(id+"F0.wireOp",EDGE,"E261"),sQuery(id+"F0.wireOp",EDGE,"E262"),sQuery(id+"F0.wireOp",EDGE,"E263"),sQuery(id+"F0.wireOp",EDGE,"E264"),sQuery(id+"F0.wireOp",EDGE,"E265"),sQuery(id+"F0.wireOp",EDGE,"E266"),sQuery(id+"F0.wireOp",EDGE,"E267"),sQuery(id+"F0.wireOp",EDGE,"E268"),sQuery(id+"F0.wireOp",EDGE,"E269"),sQuery(id+"F0.wireOp",EDGE,"E270"),sQuery(id+"F0.wireOp",EDGE,"E271"),sQuery(id+"F0.wireOp",EDGE,"E272"),sQuery(id+"F0.wireOp",EDGE,"E273"),sQuery(id+"F0.wireOp",EDGE,"E274"),sQuery(id+"F0.wireOp",EDGE,"E275"),sQuery(id+"F0.wireOp",EDGE,"E276"),sQuery(id+"F0.wireOp",EDGE,"E277"),sQuery(id+"F0.wireOp",EDGE,"E278"),sQuery(id+"F0.wireOp",EDGE,"E279"),sQuery(id+"F0.wireOp",EDGE,"E280"),sQuery(id+"F0.wireOp",EDGE,"E281"),sQuery(id+"F0.wireOp",EDGE,"E282"),sQuery(id+"F0.wireOp",EDGE,"E283"),sQuery(id+"F0.wireOp",EDGE,"E284"),sQuery(id+"F0.wireOp",EDGE,"E285"),sQuery(id+"F0.wireOp",EDGE,"E286"),sQuery(id+"F0.wireOp",EDGE,"E287"),sQuery(id+"F0.wireOp",EDGE,"E288"),sQuery(id+"F0.wireOp",EDGE,"E289"),sQuery(id+"F0.wireOp",EDGE,"E290"),sQuery(id+"F0.wireOp",EDGE,"E291"),sQuery(id+"F0.wireOp",EDGE,"E292"),sQuery(id+"F0.wireOp",EDGE,"E293"),sQuery(id+"F0.wireOp",EDGE,"E294"),sQuery(id+"F0.wireOp",EDGE,"E295"),sQuery(id+"F0.wireOp",EDGE,"E296"),sQuery(id+"F0.wireOp",EDGE,"E297"),sQuery(id+"F0.wireOp",EDGE,"E298"),sQuery(id+"F0.wireOp",EDGE,"E299"),sQuery(id+"F0.wireOp",EDGE,"E300"),sQuery(id+"F0.wireOp",EDGE,"E301"),sQuery(id+"F0.wireOp",EDGE,"E302"),sQuery(id+"F0.wireOp",EDGE,"E303"),sQuery(id+"F0.wireOp",EDGE,"E304"),sQuery(id+"F0.wireOp",EDGE,"E305"),sQuery(id+"F0.wireOp",EDGE,"E306"),sQuery(id+"F0.wireOp",EDGE,"E307"),sQuery(id+"F0.wireOp",EDGE,"E308"),sQuery(id+"F0.wireOp",EDGE,"E309"),sQuery(id+"F0.wireOp",EDGE,"E310"),sQuery(id+"F0.wireOp",EDGE,"E311"),sQuery(id+"F0.wireOp",EDGE,"E312"),sQuery(id+"F0.wireOp",EDGE,"E313"),sQuery(id+"F0.wireOp",EDGE,"E314"),sQuery(id+"F0.wireOp",EDGE,"E315"),sQuery(id+"F0.wireOp",EDGE,"E316"),sQuery(id+"F0.wireOp",EDGE,"E317"),sQuery(id+"F0.wireOp",EDGE,"E318"),sQuery(id+"F0.wireOp",EDGE,"E319"),sQuery(id+"F0.wireOp",EDGE,"E320"),sQuery(id+"F0.wireOp",EDGE,"E321"),sQuery(id+"F0.wireOp",EDGE,"E322"),sQuery(id+"F0.wireOp",EDGE,"E323"),sQuery(id+"F0.wireOp",EDGE,"E324"),sQuery(id+"F0.wireOp",EDGE,"E325"),sQuery(id+"F0.wireOp",EDGE,"E326"),sQuery(id+"F0.wireOp",EDGE,"E327"),sQuery(id+"F0.wireOp",EDGE,"E328"),sQuery(id+"F0.wireOp",EDGE,"E329"),sQuery(id+"F0.wireOp",EDGE,"E330"),sQuery(id+"F0.wireOp",EDGE,"E331"),sQuery(id+"F0.wireOp",EDGE,"E332"),sQuery(id+"F0.wireOp",EDGE,"E333"),sQuery(id+"F0.wireOp",EDGE,"E334"),sQuery(id+"F0.wireOp",EDGE,"E335"),sQuery(id+"F0.wireOp",EDGE,"E336"),sQuery(id+"F0.wireOp",EDGE,"E337"),sQuery(id+"F0.wireOp",EDGE,"E338"),sQuery(id+"F0.wireOp",EDGE,"E339"),sQuery(id+"F0.wireOp",EDGE,"E340"),sQuery(id+"F0.wireOp",EDGE,"E341"),sQuery(id+"F0.wireOp",EDGE,"E342"),sQuery(id+"F0.wireOp",EDGE,"E343"),sQuery(id+"F0.wireOp",EDGE,"E344"),sQuery(id+"F0.wireOp",EDGE,"E345"),sQuery(id+"F0.wireOp",EDGE,"E346"),sQuery(id+"F0.wireOp",EDGE,"E347"),sQuery(id+"F0.wireOp",EDGE,"E348"),sQuery(id+"F0.wireOp",EDGE,"E349"),sQuery(id+"F0.wireOp",EDGE,"E350"),sQuery(id+"F0.wireOp",EDGE,"E351"),sQuery(id+"F0.wireOp",EDGE,"E352"),sQuery(id+"F0.wireOp",EDGE,"E353"),sQuery(id+"F0.wireOp",EDGE,"E354"),sQuery(id+"F0.wireOp",EDGE,"E355"),sQuery(id+"F0.wireOp",EDGE,"E356"),sQuery(id+"F0.wireOp",EDGE,"E357"),sQuery(id+"F0.wireOp",EDGE,"E358"),sQuery(id+"F0.wireOp",EDGE,"E359"),sQuery(id+"F0.wireOp",EDGE,"E360"),sQuery(id+"F0.wireOp",EDGE,"E361"),sQuery(id+"F0.wireOp",EDGE,"E362"),sQuery(id+"F0.wireOp",EDGE,"E363"),sQuery(id+"F0.wireOp",EDGE,"E364"),sQuery(id+"F0.wireOp",EDGE,"E365"),sQuery(id+"F0.wireOp",EDGE,"E366"),sQuery(id+"F0.wireOp",EDGE,"E367"),sQuery(id+"F0.wireOp",EDGE,"E368"),sQuery(id+"F0.wireOp",EDGE,"E369"),sQuery(id+"F0.wireOp",EDGE,"E370"),sQuery(id+"F0.wireOp",EDGE,"E371"),sQuery(id+"F0.wireOp",EDGE,"E372"),sQuery(id+"F0.wireOp",EDGE,"E373"),sQuery(id+"F0.wireOp",EDGE,"E374"),sQuery(id+"F0.wireOp",EDGE,"E375"),sQuery(id+"F0.wireOp",EDGE,"E376"),sQuery(id+"F0.wireOp",EDGE,"E377"),sQuery(id+"F0.wireOp",EDGE,"E378"),sQuery(id+"F0.wireOp",EDGE,"E379"),sQuery(id+"F0.wireOp",EDGE,"E380"),sQuery(id+"F0.wireOp",EDGE,"E381"),sQuery(id+"F0.wireOp",EDGE,"E382"),sQuery(id+"F0.wireOp",EDGE,"E383"),sQuery(id+"F0.wireOp",EDGE,"E384"),sQuery(id+"F0.wireOp",EDGE,"E385"),sQuery(id+"F0.wireOp",EDGE,"E386"),sQuery(id+"F0.wireOp",EDGE,"E387"),sQuery(id+"F0.wireOp",EDGE,"E388"),sQuery(id+"F0.wireOp",EDGE,"E389"),sQuery(id+"F0.wireOp",EDGE,"E390"),sQuery(id+"F0.wireOp",EDGE,"E391"),sQuery(id+"F0.wireOp",EDGE,"E392"),sQuery(id+"F0.wireOp",EDGE,"E393"),sQuery(id+"F0.wireOp",EDGE,"E394"),sQuery(id+"F0.wireOp",EDGE,"E395"),sQuery(id+"F0.wireOp",EDGE,"E396"),sQuery(id+"F0.wireOp",EDGE,"E397"),sQuery(id+"F0.wireOp",EDGE,"E398"),sQuery(id+"F0.wireOp",EDGE,"E399"),sQuery(id+"F0.wireOp",EDGE,"E400"),sQuery(id+"F0.wireOp",EDGE,"E401"),sQuery(id+"F0.wireOp",EDGE,"E402"),sQuery(id+"F0.wireOp",EDGE,"E403"),sQuery(id+"F0.wireOp",EDGE,"E404"),sQuery(id+"F0.wireOp",EDGE,"E405"),sQuery(id+"F0.wireOp",EDGE,"E406"),sQuery(id+"F0.wireOp",EDGE,"E407"),sQuery(id+"F0.wireOp",EDGE,"E408"),sQuery(id+"F0.wireOp",EDGE,"E409"),sQuery(id+"F0.wireOp",EDGE,"E410"),sQuery(id+"F0.wireOp",EDGE,"E411"),sQuery(id+"F0.wireOp",EDGE,"E412"),sQuery(id+"F0.wireOp",EDGE,"E413"),sQuery(id+"F0.wireOp",EDGE,"E414"),sQuery(id+"F0.wireOp",EDGE,"E415"),sQuery(id+"F0.wireOp",EDGE,"E416"),sQuery(id+"F0.wireOp",EDGE,"E417"),sQuery(id+"F0.wireOp",EDGE,"E418"),sQuery(id+"F0.wireOp",EDGE,"E419"),sQuery(id+"F0.wireOp",EDGE,"E420"),sQuery(id+"F0.wireOp",EDGE,"E421"),sQuery(id+"F0.wireOp",EDGE,"E422"),sQuery(id+"F0.wireOp",EDGE,"E423"),sQuery(id+"F0.wireOp",EDGE,"E424"),sQuery(id+"F0.wireOp",EDGE,"E425"),sQuery(id+"F0.wireOp",EDGE,"E426"),sQuery(id+"F0.wireOp",EDGE,"E427"),sQuery(id+"F0.wireOp",EDGE,"E428"),sQuery(id+"F0.wireOp",EDGE,"E429"),sQuery(id+"F0.wireOp",EDGE,"E430"),sQuery(id+"F0.wireOp",EDGE,"E431"),sQuery(id+"F0.wireOp",EDGE,"E432"),sQuery(id+"F0.wireOp",EDGE,"E433"),sQuery(id+"F0.wireOp",EDGE,"E434"),sQuery(id+"F0.wireOp",EDGE,"E435"),sQuery(id+"F0.wireOp",EDGE,"E436"),sQuery(id+"F0.wireOp",EDGE,"E437"),sQuery(id+"F0.wireOp",EDGE,"E438"),sQuery(id+"F0.wireOp",EDGE,"E439"),sQuery(id+"F0.wireOp",EDGE,"E440"),sQuery(id+"F0.wireOp",EDGE,"E441"),sQuery(id+"F0.wireOp",EDGE,"E442"),sQuery(id+"F0.wireOp",EDGE,"E443"),sQuery(id+"F0.wireOp",EDGE,"E444"),sQuery(id+"F0.wireOp",EDGE,"E445"),sQuery(id+"F0.wireOp",EDGE,"E446"),sQuery(id+"F0.wireOp",EDGE,"E447"),sQuery(id+"F0.wireOp",EDGE,"E448"),sQuery(id+"F0.wireOp",EDGE,"E449"),sQuery(id+"F0.wireOp",EDGE,"E450"),sQuery(id+"F0.wireOp",EDGE,"E451"),sQuery(id+"F0.wireOp",EDGE,"E452"),sQuery(id+"F0.wireOp",EDGE,"E453"),sQuery(id+"F0.wireOp",EDGE,"E454"),sQuery(id+"F0.wireOp",EDGE,"E455"),sQuery(id+"F0.wireOp",EDGE,"E456"),sQuery(id+"F0.wireOp",EDGE,"E457"),sQuery(id+"F0.wireOp",EDGE,"E458"),sQuery(id+"F0.wireOp",EDGE,"E459"),sQuery(id+"F0.wireOp",EDGE,"E460"),sQuery(id+"F0.wireOp",EDGE,"E461"),sQuery(id+"F0.wireOp",EDGE,"E462"),sQuery(id+"F0.wireOp",EDGE,"E463"),sQuery(id+"F0.wireOp",EDGE,"E464"),sQuery(id+"F0.wireOp",EDGE,"E465"),sQuery(id+"F0.wireOp",EDGE,"E466"),sQuery(id+"F0.wireOp",EDGE,"E467"),sQuery(id+"F0.wireOp",EDGE,"E468"),sQuery(id+"F0.wireOp",EDGE,"E469"),sQuery(id+"F0.wireOp",EDGE,"E470"),sQuery(id+"F0.wireOp",EDGE,"E471"),sQuery(id+"F0.wireOp",EDGE,"E472"),sQuery(id+"F0.wireOp",EDGE,"E473"),sQuery(id+"F0.wireOp",EDGE,"E474"),sQuery(id+"F0.wireOp",EDGE,"E475"),sQuery(id+"F0.wireOp",EDGE,"E476"),sQuery(id+"F0.wireOp",EDGE,"E477"),sQuery(id+"F0.wireOp",EDGE,"E478"),sQuery(id+"F0.wireOp",EDGE,"E479"),sQuery(id+"F0.wireOp",EDGE,"E480"),sQuery(id+"F0.wireOp",EDGE,"E481"),sQuery(id+"F0.wireOp",EDGE,"E482"),sQuery(id+"F0.wireOp",EDGE,"E483"),sQuery(id+"F0.wireOp",EDGE,"E484"),sQuery(id+"F0.wireOp",EDGE,"E485"),sQuery(id+"F0.wireOp",EDGE,"E486"),sQuery(id+"F0.wireOp",EDGE,"E487"),sQuery(id+"F0.wireOp",EDGE,"E488"),sQuery(id+"F0.wireOp",EDGE,"E489"),sQuery(id+"F0.wireOp",EDGE,"E490"),sQuery(id+"F0.wireOp",EDGE,"E491"),sQuery(id+"F0.wireOp",EDGE,"E492"),sQuery(id+"F0.wireOp",EDGE,"E493"),sQuery(id+"F0.wireOp",EDGE,"E494"),sQuery(id+"F0.wireOp",EDGE,"E495"),sQuery(id+"F0.wireOp",EDGE,"E496"),sQuery(id+"F0.wireOp",EDGE,"E497"),sQuery(id+"F0.wireOp",EDGE,"E498"),sQuery(id+"F0.wireOp",EDGE,"E499"),sQuery(id+"F0.wireOp",EDGE,"E500"),sQuery(id+"F0.wireOp",EDGE,"E501"),sQuery(id+"F0.wireOp",EDGE,"E502"),sQuery(id+"F0.wireOp",EDGE,"E503"),sQuery(id+"F0.wireOp",EDGE,"E504"),sQuery(id+"F0.wireOp",EDGE,"E505"),sQuery(id+"F0.wireOp",EDGE,"E506"),sQuery(id+"F0.wireOp",EDGE,"E507"),sQuery(id+"F0.wireOp",EDGE,"E508"),sQuery(id+"F0.wireOp",EDGE,"E509"),sQuery(id+"F0.wireOp",EDGE,"E510"),sQuery(id+"F0.wireOp",EDGE,"E511"),sQuery(id+"F0.wireOp",EDGE,"E512"),sQuery(id+"F0.wireOp",EDGE,"E513"),sQuery(id+"F0.wireOp",EDGE,"E514"),sQuery(id+"F0.wireOp",EDGE,"E515"),sQuery(id+"F0.wireOp",EDGE,"E516"),sQuery(id+"F0.wireOp",EDGE,"E517"),sQuery(id+"F0.wireOp",EDGE,"E518"),sQuery(id+"F0.wireOp",EDGE,"E519"),sQuery(id+"F0.wireOp",EDGE,"E520"),sQuery(id+"F0.wireOp",EDGE,"E521"),sQuery(id+"F0.wireOp",EDGE,"E522"),sQuery(id+"F0.wireOp",EDGE,"E523"),sQuery(id+"F0.wireOp",EDGE,"E524"),sQuery(id+"F0.wireOp",EDGE,"E525"),sQuery(id+"F0.wireOp",EDGE,"E526"),sQuery(id+"F0.wireOp",EDGE,"E527"),sQuery(id+"F0.wireOp",EDGE,"E528"),sQuery(id+"F0.wireOp",EDGE,"E529"),sQuery(id+"F0.wireOp",EDGE,"E530"),sQuery(id+"F0.wireOp",EDGE,"E531"),sQuery(id+"F0.wireOp",EDGE,"E532"),sQuery(id+"F0.wireOp",EDGE,"E533"),sQuery(id+"F0.wireOp",EDGE,"E534"),sQuery(id+"F0.wireOp",EDGE,"E535"),sQuery(id+"F0.wireOp",EDGE,"E536"),sQuery(id+"F0.wireOp",EDGE,"E537"),sQuery(id+"F0.wireOp",EDGE,"E538"),sQuery(id+"F0.wireOp",EDGE,"E539"),sQuery(id+"F0.wireOp",EDGE,"E540"),sQuery(id+"F0.wireOp",EDGE,"E541"),sQuery(id+"F0.wireOp",EDGE,"E542"),sQuery(id+"F0.wireOp",EDGE,"E543"),sQuery(id+"F0.wireOp",EDGE,"E544"),sQuery(id+"F0.wireOp",EDGE,"E545"),sQuery(id+"F0.wireOp",EDGE,"E546"),sQuery(id+"F0.wireOp",EDGE,"E547"),sQuery(id+"F0.wireOp",EDGE,"E548"),sQuery(id+"F0.wireOp",EDGE,"E549"),sQuery(id+"F0.wireOp",EDGE,"E550"),sQuery(id+"F0.wireOp",EDGE,"E551"),sQuery(id+"F0.wireOp",EDGE,"E552"),sQuery(id+"F0.wireOp",EDGE,"E553"),sQuery(id+"F0.wireOp",EDGE,"E554"),sQuery(id+"F0.wireOp",EDGE,"E555"),sQuery(id+"F0.wireOp",EDGE,"E556"),sQuery(id+"F0.wireOp",EDGE,"E557"),sQuery(id+"F0.wireOp",EDGE,"E558"),sQuery(id+"F0.wireOp",EDGE,"E559"),sQuery(id+"F0.wireOp",EDGE,"E560"),sQuery(id+"F0.wireOp",EDGE,"E561"),sQuery(id+"F0.wireOp",EDGE,"E562"),sQuery(id+"F0.wireOp",EDGE,"E563"),sQuery(id+"F0.wireOp",EDGE,"E564"),sQuery(id+"F0.wireOp",EDGE,"E565"),sQuery(id+"F0.wireOp",EDGE,"E566"),sQuery(id+"F0.wireOp",EDGE,"E567"),sQuery(id+"F0.wireOp",EDGE,"E568"),sQuery(id+"F0.wireOp",EDGE,"E569"),sQuery(id+"F0.wireOp",EDGE,"E570"),sQuery(id+"F0.wireOp",EDGE,"E571"),sQuery(id+"F0.wireOp",EDGE,"E572"),sQuery(id+"F0.wireOp",EDGE,"E573"),sQuery(id+"F0.wireOp",EDGE,"E574"),sQuery(id+"F0.wireOp",EDGE,"E575"),sQuery(id+"F0.wireOp",EDGE,"E576"),sQuery(id+"F0.wireOp",EDGE,"E577"),sQuery(id+"F0.wireOp",EDGE,"E578"),sQuery(id+"F0.wireOp",EDGE,"E579"),sQuery(id+"F0.wireOp",EDGE,"E580"),sQuery(id+"F0.wireOp",EDGE,"E581"),sQuery(id+"F0.wireOp",EDGE,"E582"),sQuery(id+"F0.wireOp",EDGE,"E583"),sQuery(id+"F0.wireOp",EDGE,"E584"),sQuery(id+"F0.wireOp",EDGE,"E585"),sQuery(id+"F0.wireOp",EDGE,"E586"),sQuery(id+"F0.wireOp",EDGE,"E587"),sQuery(id+"F0.wireOp",EDGE,"E588"),sQuery(id+"F0.wireOp",EDGE,"E589"),sQuery(id+"F0.wireOp",EDGE,"E590"),sQuery(id+"F0.wireOp",EDGE,"E591"),sQuery(id+"F0.wireOp",EDGE,"E592"),sQuery(id+"F0.wireOp",EDGE,"E593"),sQuery(id+"F0.wireOp",EDGE,"E594"),sQuery(id+"F0.wireOp",EDGE,"E595"),sQuery(id+"F0.wireOp",EDGE,"E596"),sQuery(id+"F0.wireOp",EDGE,"E597"),sQuery(id+"F0.wireOp",EDGE,"E598"),sQuery(id+"F0.wireOp",EDGE,"E599"),sQuery(id+"F0.wireOp",EDGE,"E600"),sQuery(id+"F0.wireOp",EDGE,"E601"),sQuery(id+"F0.wireOp",EDGE,"E602"),sQuery(id+"F0.wireOp",EDGE,"E603"),sQuery(id+"F0.wireOp",EDGE,"E604"),sQuery(id+"F0.wireOp",EDGE,"E605"),sQuery(id+"F0.wireOp",EDGE,"E606"),sQuery(id+"F0.wireOp",EDGE,"E607"),sQuery(id+"F0.wireOp",EDGE,"E608"),sQuery(id+"F0.wireOp",EDGE,"E609"),sQuery(id+"F0.wireOp",EDGE,"E610"),sQuery(id+"F0.wireOp",EDGE,"E611"),sQuery(id+"F0.wireOp",EDGE,"E612"),sQuery(id+"F0.wireOp",EDGE,"E613"),sQuery(id+"F0.wireOp",EDGE,"E614"),sQuery(id+"F0.wireOp",EDGE,"E615"),sQuery(id+"F0.wireOp",EDGE,"E616"),sQuery(id+"F0.wireOp",EDGE,"E617"),sQuery(id+"F0.wireOp",EDGE,"E618"),sQuery(id+"F0.wireOp",EDGE,"E619"),sQuery(id+"F0.wireOp",EDGE,"E620"),sQuery(id+"F0.wireOp",EDGE,"E621"),sQuery(id+"F0.wireOp",EDGE,"E622"),sQuery(id+"F0.wireOp",EDGE,"E623"),sQuery(id+"F0.wireOp",EDGE,"E624"),sQuery(id+"F0.wireOp",EDGE,"E625"),sQuery(id+"F0.wireOp",EDGE,"E626"),sQuery(id+"F0.wireOp",EDGE,"E627"),sQuery(id+"F0.wireOp",EDGE,"E628"),sQuery(id+"F0.wireOp",EDGE,"E629"),sQuery(id+"F0.wireOp",EDGE,"E630"),sQuery(id+"F0.wireOp",EDGE,"E631"),sQuery(id+"F0.wireOp",EDGE,"E632"),sQuery(id+"F0.wireOp",EDGE,"E633"),sQuery(id+"F0.wireOp",EDGE,"E634"),sQuery(id+"F0.wireOp",EDGE,"E635"),sQuery(id+"F0.wireOp",EDGE,"E636"),sQuery(id+"F0.wireOp",EDGE,"E637"),sQuery(id+"F0.wireOp",EDGE,"E638"),sQuery(id+"F0.wireOp",EDGE,"E639"),sQuery(id+"F0.wireOp",EDGE,"E640"),sQuery(id+"F0.wireOp",EDGE,"E641"),sQuery(id+"F0.wireOp",EDGE,"E642"),sQuery(id+"F0.wireOp",EDGE,"E643"),sQuery(id+"F0.wireOp",EDGE,"E644"),sQuery(id+"F0.wireOp",EDGE,"E645"),sQuery(id+"F0.wireOp",EDGE,"E646"),sQuery(id+"F0.wireOp",EDGE,"E647"),sQuery(id+"F0.wireOp",EDGE,"E648"),sQuery(id+"F0.wireOp",EDGE,"E649"),sQuery(id+"F0.wireOp",EDGE,"E650"),sQuery(id+"F0.wireOp",EDGE,"E651"),sQuery(id+"F0.wireOp",EDGE,"E652"),sQuery(id+"F0.wireOp",EDGE,"E653"),sQuery(id+"F0.wireOp",EDGE,"E654"),sQuery(id+"F0.wireOp",EDGE,"E655"),sQuery(id+"F0.wireOp",EDGE,"E656"),sQuery(id+"F0.wireOp",EDGE,"E657"),sQuery(id+"F0.wireOp",EDGE,"E658"),sQuery(id+"F0.wireOp",EDGE,"E659"),sQuery(id+"F0.wireOp",EDGE,"E660"),sQuery(id+"F0.wireOp",EDGE,"E661"),sQuery(id+"F0.wireOp",EDGE,"E662"),sQuery(id+"F0.wireOp",EDGE,"E663"),sQuery(id+"F0.wireOp",EDGE,"E664"),sQuery(id+"F0.wireOp",EDGE,"E665"),sQuery(id+"F0.wireOp",EDGE,"E666"),sQuery(id+"F0.wireOp",EDGE,"E667"),sQuery(id+"F0.wireOp",EDGE,"E668"),sQuery(id+"F0.wireOp",EDGE,"E669"),sQuery(id+"F0.wireOp",EDGE,"E670"),sQuery(id+"F0.wireOp",EDGE,"E671"),sQuery(id+"F0.wireOp",EDGE,"E672"),sQuery(id+"F0.wireOp",EDGE,"E673"),sQuery(id+"F0.wireOp",EDGE,"E674"),sQuery(id+"F0.wireOp",EDGE,"E675"),sQuery(id+"F0.wireOp",EDGE,"E676"),sQuery(id+"F0.wireOp",EDGE,"E677"),sQuery(id+"F0.wireOp",EDGE,"E678"),sQuery(id+"F0.wireOp",EDGE,"E679"),sQuery(id+"F0.wireOp",EDGE,"E680"),sQuery(id+"F0.wireOp",EDGE,"E681"),sQuery(id+"F0.wireOp",EDGE,"E682"),sQuery(id+"F0.wireOp",EDGE,"E683"),sQuery(id+"F0.wireOp",EDGE,"E684"),sQuery(id+"F0.wireOp",EDGE,"E685"),sQuery(id+"F0.wireOp",EDGE,"E686"),sQuery(id+"F0.wireOp",EDGE,"E687"),sQuery(id+"F0.wireOp",EDGE,"E688"),sQuery(id+"F0.wireOp",EDGE,"E689"),sQuery(id+"F0.wireOp",EDGE,"E690"),sQuery(id+"F0.wireOp",EDGE,"E691"),sQuery(id+"F0.wireOp",EDGE,"E692"),sQuery(id+"F0.wireOp",EDGE,"E693"),sQuery(id+"F0.wireOp",EDGE,"E694"),sQuery(id+"F0.wireOp",EDGE,"E695"),sQuery(id+"F0.wireOp",EDGE,"E696"),sQuery(id+"F0.wireOp",EDGE,"E697"),sQuery(id+"F0.wireOp",EDGE,"E698"),sQuery(id+"F0.wireOp",EDGE,"E699"),sQuery(id+"F0.wireOp",EDGE,"E700"),sQuery(id+"F0.wireOp",EDGE,"E701"),sQuery(id+"F0.wireOp",EDGE,"E702"),sQuery(id+"F0.wireOp",EDGE,"E703"),sQuery(id+"F0.wireOp",EDGE,"E704"),sQuery(id+"F0.wireOp",EDGE,"E705"),sQuery(id+"F0.wireOp",EDGE,"E706"),sQuery(id+"F0.wireOp",EDGE,"E707"),sQuery(id+"F0.wireOp",EDGE,"E708"),sQuery(id+"F0.wireOp",EDGE,"E709"),sQuery(id+"F0.wireOp",EDGE,"E710"),sQuery(id+"F0.wireOp",EDGE,"E711"),sQuery(id+"F0.wireOp",EDGE,"E712"),sQuery(id+"F0.wireOp",EDGE,"E713"),sQuery(id+"F0.wireOp",EDGE,"E714"),sQuery(id+"F0.wireOp",EDGE,"E715"),sQuery(id+"F0.wireOp",EDGE,"E716"),sQuery(id+"F0.wireOp",EDGE,"E717"),sQuery(id+"F0.wireOp",EDGE,"E718"),sQuery(id+"F0.wireOp",EDGE,"E719"),sQuery(id+"F0.wireOp",EDGE,"E720"),sQuery(id+"F0.wireOp",EDGE,"E721"),sQuery(id+"F0.wireOp",EDGE,"E722"),sQuery(id+"F0.wireOp",EDGE,"E723"),sQuery(id+"F0.wireOp",EDGE,"E724"),sQuery(id+"F0.wireOp",EDGE,"E725"),sQuery(id+"F0.wireOp",EDGE,"E726"),sQuery(id+"F0.wireOp",EDGE,"E727"),sQuery(id+"F0.wireOp",EDGE,"E728"),sQuery(id+"F0.wireOp",EDGE,"E729"),sQuery(id+"F0.wireOp",EDGE,"E730"),sQuery(id+"F0.wireOp",EDGE,"E731"),sQuery(id+"F0.wireOp",EDGE,"E732"),sQuery(id+"F0.wireOp",EDGE,"E733"),sQuery(id+"F0.wireOp",EDGE,"E734"),sQuery(id+"F0.wireOp",EDGE,"E735"),sQuery(id+"F0.wireOp",EDGE,"E736"),sQuery(id+"F0.wireOp",EDGE,"E737"),sQuery(id+"F0.wireOp",EDGE,"E738"),sQuery(id+"F0.wireOp",EDGE,"E739"),sQuery(id+"F0.wireOp",EDGE,"E740"),sQuery(id+"F0.wireOp",EDGE,"E741"),sQuery(id+"F0.wireOp",EDGE,"E742"),sQuery(id+"F0.wireOp",EDGE,"E743"),sQuery(id+"F0.wireOp",EDGE,"E744"),sQuery(id+"F0.wireOp",EDGE,"E745"),sQuery(id+"F0.wireOp",EDGE,"E746"),sQuery(id+"F0.wireOp",EDGE,"E747"),sQuery(id+"F0.wireOp",EDGE,"E748"),sQuery(id+"F0.wireOp",EDGE,"E749"),sQuery(id+"F0.wireOp",EDGE,"E750"),sQuery(id+"F0.wireOp",EDGE,"E751"),sQuery(id+"F0.wireOp",EDGE,"E752"),sQuery(id+"F0.wireOp",EDGE,"E753"),sQuery(id+"F0.wireOp",EDGE,"E754"),sQuery(id+"F0.wireOp",EDGE,"E755"),sQuery(id+"F0.wireOp",EDGE,"E756"),sQuery(id+"F0.wireOp",EDGE,"E757"),sQuery(id+"F0.wireOp",EDGE,"E758"),sQuery(id+"F0.wireOp",EDGE,"E759"),sQuery(id+"F0.wireOp",EDGE,"E760"),sQuery(id+"F0.wireOp",EDGE,"E761"),sQuery(id+"F0.wireOp",EDGE,"E762"),sQuery(id+"F0.wireOp",EDGE,"E763"),sQuery(id+"F0.wireOp",EDGE,"E764"),sQuery(id+"F0.wireOp",EDGE,"E765"),sQuery(id+"F0.wireOp",EDGE,"E766"),sQuery(id+"F0.wireOp",EDGE,"E767"),sQuery(id+"F0.wireOp",EDGE,"E768"),sQuery(id+"F0.wireOp",EDGE,"E769"),sQuery(id+"F0.wireOp",EDGE,"E770"),sQuery(id+"F0.wireOp",EDGE,"E771"),sQuery(id+"F0.wireOp",EDGE,"E772"),sQuery(id+"F0.wireOp",EDGE,"E773"),sQuery(id+"F0.wireOp",EDGE,"E774"),sQuery(id+"F0.wireOp",EDGE,"E775"),sQuery(id+"F0.wireOp",EDGE,"E776"),sQuery(id+"F0.wireOp",EDGE,"E777"),sQuery(id+"F0.wireOp",EDGE,"E778"),sQuery(id+"F0.wireOp",EDGE,"E779"),sQuery(id+"F0.wireOp",EDGE,"E780"),sQuery(id+"F0.wireOp",EDGE,"E781"),sQuery(id+"F0.wireOp",EDGE,"E782"),sQuery(id+"F0.wireOp",EDGE,"E783"),sQuery(id+"F0.wireOp",EDGE,"E784"),sQuery(id+"F0.wireOp",EDGE,"E785"),sQuery(id+"F0.wireOp",EDGE,"E786"),sQuery(id+"F0.wireOp",EDGE,"E787"),sQuery(id+"F0.wireOp",EDGE,"E788"),sQuery(id+"F0.wireOp",EDGE,"E789"),sQuery(id+"F0.wireOp",EDGE,"E790"),sQuery(id+"F0.wireOp",EDGE,"E791"),sQuery(id+"F0.wireOp",EDGE,"E792"),sQuery(id+"F0.wireOp",EDGE,"E793"),sQuery(id+"F0.wireOp",EDGE,"E794"),sQuery(id+"F0.wireOp",EDGE,"E795"),sQuery(id+"F0.wireOp",EDGE,"E796"),sQuery(id+"F0.wireOp",EDGE,"E797"),sQuery(id+"F0.wireOp",EDGE,"E798"),sQuery(id+"F0.wireOp",EDGE,"E799"),sQuery(id+"F0.wireOp",EDGE,"E800"),sQuery(id+"F0.wireOp",EDGE,"E801"),sQuery(id+"F0.wireOp",EDGE,"E802"),sQuery(id+"F0.wireOp",EDGE,"E803"),sQuery(id+"F0.wireOp",EDGE,"E804"),sQuery(id+"F0.wireOp",EDGE,"E805"),sQuery(id+"F0.wireOp",EDGE,"E806"),sQuery(id+"F0.wireOp",EDGE,"E807"),sQuery(id+"F0.wireOp",EDGE,"E808"),sQuery(id+"F0.wireOp",EDGE,"E809"),sQuery(id+"F0.wireOp",EDGE,"E810"),sQuery(id+"F0.wireOp",EDGE,"E811"),sQuery(id+"F0.wireOp",EDGE,"E812"),sQuery(id+"F0.wireOp",EDGE,"E813"),sQuery(id+"F0.wireOp",EDGE,"E814"),sQuery(id+"F0.wireOp",EDGE,"E815"),sQuery(id+"F0.wireOp",EDGE,"E816"),sQuery(id+"F0.wireOp",EDGE,"E817"),sQuery(id+"F0.wireOp",EDGE,"E818"),sQuery(id+"F0.wireOp",EDGE,"E819"),sQuery(id+"F0.wireOp",EDGE,"E820"),sQuery(id+"F0.wireOp",EDGE,"E821"),sQuery(id+"F0.wireOp",EDGE,"E822"),sQuery(id+"F0.wireOp",EDGE,"E823"),sQuery(id+"F0.wireOp",EDGE,"E824"),sQuery(id+"F0.wireOp",EDGE,"E825"),sQuery(id+"F0.wireOp",EDGE,"E826"),sQuery(id+"F0.wireOp",EDGE,"E827"),sQuery(id+"F0.wireOp",EDGE,"E828"),sQuery(id+"F0.wireOp",EDGE,"E829"),sQuery(id+"F0.wireOp",EDGE,"E830"),sQuery(id+"F0.wireOp",EDGE,"E831"),sQuery(id+"F0.wireOp",EDGE,"E832"),sQuery(id+"F0.wireOp",EDGE,"E833"),sQuery(id+"F0.wireOp",EDGE,"E834"),sQuery(id+"F0.wireOp",EDGE,"E835"),sQuery(id+"F0.wireOp",EDGE,"E836"),sQuery(id+"F0.wireOp",EDGE,"E837"),sQuery(id+"F0.wireOp",EDGE,"E838"),sQuery(id+"F0.wireOp",EDGE,"E839"),sQuery(id+"F0.wireOp",EDGE,"E840"),sQuery(id+"F0.wireOp",EDGE,"E841"),sQuery(id+"F0.wireOp",EDGE,"E842"),sQuery(id+"F0.wireOp",EDGE,"E843"),sQuery(id+"F0.wireOp",EDGE,"E844"),sQuery(id+"F0.wireOp",EDGE,"E845"),sQuery(id+"F0.wireOp",EDGE,"E846"),sQuery(id+"F0.wireOp",EDGE,"E847"),sQuery(id+"F0.wireOp",EDGE,"E848"),sQuery(id+"F0.wireOp",EDGE,"E849"),sQuery(id+"F0.wireOp",EDGE,"E850"),sQuery(id+"F0.wireOp",EDGE,"E851"),sQuery(id+"F0.wireOp",EDGE,"E852"),sQuery(id+"F0.wireOp",EDGE,"E853"),sQuery(id+"F0.wireOp",EDGE,"E854"),sQuery(id+"F0.wireOp",EDGE,"E855"),sQuery(id+"F0.wireOp",EDGE,"E856"),sQuery(id+"F0.wireOp",EDGE,"E857"),sQuery(id+"F0.wireOp",EDGE,"E858"),sQuery(id+"F0.wireOp",EDGE,"E859"),sQuery(id+"F0.wireOp",EDGE,"E860"),sQuery(id+"F0.wireOp",EDGE,"E861"),sQuery(id+"F0.wireOp",EDGE,"E862"),sQuery(id+"F0.wireOp",EDGE,"E863"),sQuery(id+"F0.wireOp",EDGE,"E864"),sQuery(id+"F0.wireOp",EDGE,"E865"),sQuery(id+"F0.wireOp",EDGE,"E866"),sQuery(id+"F0.wireOp",EDGE,"E867"),sQuery(id+"F0.wireOp",EDGE,"E868"),sQuery(id+"F0.wireOp",EDGE,"E869"),sQuery(id+"F0.wireOp",EDGE,"E870"),sQuery(id+"F0.wireOp",EDGE,"E871"),sQuery(id+"F0.wireOp",EDGE,"E872"),sQuery(id+"F0.wireOp",EDGE,"E873"),sQuery(id+"F0.wireOp",EDGE,"E874"),sQuery(id+"F0.wireOp",EDGE,"E875"),sQuery(id+"F0.wireOp",EDGE,"E876"),sQuery(id+"F0.wireOp",EDGE,"E877"),sQuery(id+"F0.wireOp",EDGE,"E878"),sQuery(id+"F0.wireOp",EDGE,"E879"),sQuery(id+"F0.wireOp",EDGE,"E880"),sQuery(id+"F0.wireOp",EDGE,"E881"),sQuery(id+"F0.wireOp",EDGE,"E882"),sQuery(id+"F0.wireOp",EDGE,"E883"),sQuery(id+"F0.wireOp",EDGE,"E884"),sQuery(id+"F0.wireOp",EDGE,"E885"),sQuery(id+"F0.wireOp",EDGE,"E886"),sQuery(id+"F0.wireOp",EDGE,"E887"),sQuery(id+"F0.wireOp",EDGE,"E888"),sQuery(id+"F0.wireOp",EDGE,"E889"),sQuery(id+"F0.wireOp",EDGE,"E890"),sQuery(id+"F0.wireOp",EDGE,"E891"),sQuery(id+"F0.wireOp",EDGE,"E892"),sQuery(id+"F0.wireOp",EDGE,"E893"),sQuery(id+"F0.wireOp",EDGE,"E894"),sQuery(id+"F0.wireOp",EDGE,"E895"),sQuery(id+"F0.wireOp",EDGE,"E896"),sQuery(id+"F0.wireOp",EDGE,"E897"),sQuery(id+"F0.wireOp",EDGE,"E898"),sQuery(id+"F0.wireOp",EDGE,"E899"),sQuery(id+"F0.wireOp",EDGE,"E900"),sQuery(id+"F0.wireOp",EDGE,"E901"),sQuery(id+"F0.wireOp",EDGE,"E902"),sQuery(id+"F0.wireOp",EDGE,"E903"),sQuery(id+"F0.wireOp",EDGE,"E904"),sQuery(id+"F0.wireOp",EDGE,"E905"),sQuery(id+"F0.wireOp",EDGE,"E906"),sQuery(id+"F0.wireOp",EDGE,"E907"),sQuery(id+"F0.wireOp",EDGE,"E908"),sQuery(id+"F0.wireOp",EDGE,"E909"),sQuery(id+"F0.wireOp",EDGE,"E910"),sQuery(id+"F0.wireOp",EDGE,"E911"),sQuery(id+"F0.wireOp",EDGE,"E912"),sQuery(id+"F0.wireOp",EDGE,"E913"),sQuery(id+"F0.wireOp",EDGE,"E914"),sQuery(id+"F0.wireOp",EDGE,"E915"),sQuery(id+"F0.wireOp",EDGE,"E916"),sQuery(id+"F0.wireOp",EDGE,"E917"),sQuery(id+"F0.wireOp",EDGE,"E918"),sQuery(id+"F0.wireOp",EDGE,"E919"),sQuery(id+"F0.wireOp",EDGE,"E920"),sQuery(id+"F0.wireOp",EDGE,"E921"),sQuery(id+"F0.wireOp",EDGE,"E922"),sQuery(id+"F0.wireOp",EDGE,"E923"),sQuery(id+"F0.wireOp",EDGE,"E924"),sQuery(id+"F0.wireOp",EDGE,"E925"),sQuery(id+"F0.wireOp",EDGE,"E926"),sQuery(id+"F0.wireOp",EDGE,"E927"),sQuery(id+"F0.wireOp",EDGE,"E928"),sQuery(id+"F0.wireOp",EDGE,"E929"),sQuery(id+"F0.wireOp",EDGE,"E930"),sQuery(id+"F0.wireOp",EDGE,"E931"),sQuery(id+"F0.wireOp",EDGE,"E932"),sQuery(id+"F0.wireOp",EDGE,"E933"),sQuery(id+"F0.wireOp",EDGE,"E934"),sQuery(id+"F0.wireOp",EDGE,"E935"),sQuery(id+"F0.wireOp",EDGE,"E936"),sQuery(id+"F0.wireOp",EDGE,"E937"),sQuery(id+"F0.wireOp",EDGE,"E938"),sQuery(id+"F0.wireOp",EDGE,"E939"),sQuery(id+"F0.wireOp",EDGE,"E940"),sQuery(id+"F0.wireOp",EDGE,"E941"),sQuery(id+"F0.wireOp",EDGE,"E942"),sQuery(id+"F0.wireOp",EDGE,"E943"),sQuery(id+"F0.wireOp",EDGE,"E944"),sQuery(id+"F0.wireOp",EDGE,"E945"),sQuery(id+"F0.wireOp",EDGE,"E946"),sQuery(id+"F0.wireOp",EDGE,"E947"),sQuery(id+"F0.wireOp",EDGE,"E948"),sQuery(id+"F0.wireOp",EDGE,"E949"),sQuery(id+"F0.wireOp",EDGE,"E950"),sQuery(id+"F0.wireOp",EDGE,"E951"),sQuery(id+"F0.wireOp",EDGE,"E952"),sQuery(id+"F0.wireOp",EDGE,"E953"),sQuery(id+"F0.wireOp",EDGE,"E954"),sQuery(id+"F0.wireOp",EDGE,"E955"),sQuery(id+"F0.wireOp",EDGE,"E956"),sQuery(id+"F0.wireOp",EDGE,"E957"),sQuery(id+"F0.wireOp",EDGE,"E958"),sQuery(id+"F0.wireOp",EDGE,"E959"),sQuery(id+"F0.wireOp",EDGE,"E960"),sQuery(id+"F0.wireOp",EDGE,"E961"),sQuery(id+"F0.wireOp",EDGE,"E962"),sQuery(id+"F0.wireOp",EDGE,"E963"),sQuery(id+"F0.wireOp",EDGE,"E964"),sQuery(id+"F0.wireOp",EDGE,"E965"),sQuery(id+"F0.wireOp",EDGE,"E966"),sQuery(id+"F0.wireOp",EDGE,"E967"),sQuery(id+"F0.wireOp",EDGE,"E968"),sQuery(id+"F0.wireOp",EDGE,"E969"),sQuery(id+"F0.wireOp",EDGE,"E970"),sQuery(id+"F0.wireOp",EDGE,"E971"),sQuery(id+"F0.wireOp",EDGE,"E972"),sQuery(id+"F0.wireOp",EDGE,"E973"),sQuery(id+"F0.wireOp",EDGE,"E974"),sQuery(id+"F0.wireOp",EDGE,"E975"),sQuery(id+"F0.wireOp",EDGE,"E976"),sQuery(id+"F0.wireOp",EDGE,"E977"),sQuery(id+"F0.wireOp",EDGE,"E978"),sQuery(id+"F0.wireOp",EDGE,"E979"),sQuery(id+"F0.wireOp",EDGE,"E980"),sQuery(id+"F0.wireOp",EDGE,"E981"),sQuery(id+"F0.wireOp",EDGE,"E982"),sQuery(id+"F0.wireOp",EDGE,"E983"),sQuery(id+"F0.wireOp",EDGE,"E984"),sQuery(id+"F0.wireOp",EDGE,"E985"),sQuery(id+"F0.wireOp",EDGE,"E986"),sQuery(id+"F0.wireOp",EDGE,"E987"),sQuery(id+"F0.wireOp",EDGE,"E988"),sQuery(id+"F0.wireOp",EDGE,"E989"),sQuery(id+"F0.wireOp",EDGE,"E990"),sQuery(id+"F0.wireOp",EDGE,"E991"),sQuery(id+"F0.wireOp",EDGE,"E992"),sQuery(id+"F0.wireOp",EDGE,"E993"),sQuery(id+"F0.wireOp",EDGE,"E994"),sQuery(id+"F0.wireOp",EDGE,"E995"),sQuery(id+"F0.wireOp",EDGE,"E996"),sQuery(id+"F0.wireOp",EDGE,"E997"),sQuery(id+"F0.wireOp",EDGE,"E998"),sQuery(id+"F0.wireOp",EDGE,"E999"),sQuery(id+"F0.wireOp",EDGE,"E1000"),sQuery(id+"F0.wireOp",EDGE,"E1001"),sQuery(id+"F0.wireOp",EDGE,"E1002"),sQuery(id+"F0.wireOp",EDGE,"E1003"),sQuery(id+"F0.wireOp",EDGE,"E1004"),sQuery(id+"F0.wireOp",EDGE,"E1005"),sQuery(id+"F0.wireOp",EDGE,"E1006"),sQuery(id+"F0.wireOp",EDGE,"E1007"),sQuery(id+"F0.wireOp",EDGE,"E1008"),sQuery(id+"F0.wireOp",EDGE,"E1009"),sQuery(id+"F0.wireOp",EDGE,"E1010"),sQuery(id+"F0.wireOp",EDGE,"E1011"),sQuery(id+"F0.wireOp",EDGE,"E1012"),sQuery(id+"F0.wireOp",EDGE,"E1013"),sQuery(id+"F0.wireOp",EDGE,"E1014"),sQuery(id+"F0.wireOp",EDGE,"E1015"),sQuery(id+"F0.wireOp",EDGE,"E1016"),sQuery(id+"F0.wireOp",EDGE,"E1017"),sQuery(id+"F0.wireOp",EDGE,"E1018"),sQuery(id+"F0.wireOp",EDGE,"E1019"),sQuery(id+"F0.wireOp",EDGE,"E1020"),sQuery(id+"F0.wireOp",EDGE,"E1021"),sQuery(id+"F0.wireOp",EDGE,"E1022"),sQuery(id+"F0.wireOp",EDGE,"E1023"),sQuery(id+"F0.wireOp",EDGE,"E1024"),sQuery(id+"F0.wireOp",EDGE,"E1025"),sQuery(id+"F0.wireOp",EDGE,"E1026"),sQuery(id+"F0.wireOp",EDGE,"E1027"),sQuery(id+"F0.wireOp",EDGE,"E1028"),sQuery(id+"F0.wireOp",EDGE,"E1029"),sQuery(id+"F0.wireOp",EDGE,"E1030"),sQuery(id+"F0.wireOp",EDGE,"E1031"),sQuery(id+"F0.wireOp",EDGE,"E1032"),sQuery(id+"F0.wireOp",EDGE,"E1033"),sQuery(id+"F0.wireOp",EDGE,"E1034"),sQuery(id+"F0.wireOp",EDGE,"E1035"),sQuery(id+"F0.wireOp",EDGE,"E1036"),sQuery(id+"F0.wireOp",EDGE,"E1037"),sQuery(id+"F0.wireOp",EDGE,"E1038"),sQuery(id+"F0.wireOp",EDGE,"E1039"),sQuery(id+"F0.wireOp",EDGE,"E1040")])],"isStart":false})});
            var sketch = newSketch(context, id + "F5", { "sketchPlane" : qUnion([Q0])});
            skCircle(sketch, "E1048", {"center": v(0, 0) * mm, "radius": 7 * mm});
            skCircle(sketch, "E1049", {"center": v(0, 0) * mm, "radius": 3.94 * mm});
            skSolve(sketch);
        }
        {
            var Q0;
            Q0=makeQuery(id+"F5.imprint","IMPRINT",FACE,{"disambiguationData":[TD([[makeQuery(id+"F5.imprint","IMPRINT",EDGE,{"derivedFrom":sQuery(id+"F5.wireOp",EDGE,"E1048")}),1.0]])]});
            extrude(context, id + "F6", {"entities" : qUnion([Q0]), "operationType" : NewBodyOperationType.REMOVE, "oppositeDirection" : true, "depth" : 4 * mm});
        }
        {
            var Q0;
            Q0=makeQuery(id+"F6.boolean.opBoolean","COPY",EDGE,{"derivedFrom":makeQuery(id+"F6.opExtrude","CAP_EDGE",EDGE,{"disambiguationData":[OSD([sQuery(id+"F5.wireOp",EDGE,"E1049")])],"isStart":false})});
            var Q1;
            Q1=makeQuery(id+"F6.boolean.opBoolean","COPY",EDGE,{"derivedFrom":makeQuery(id+"F6.opExtrude","CAP_EDGE",EDGE,{"disambiguationData":[OSD([sQuery(id+"F5.wireOp",EDGE,"E1048")])],"isStart":false})});
            fillet(context, id + "F7", {"entities" : qUnion([Q0, Q1]), "radius" : 1 * mm, "tangentPropagation" : true, "allowEdgeOverflow" : false});
        }
    });
